FCSTD DOCUMENT  (FreeCAD 0.17R13541 (Git))
Label: lorenz
License: All rights reserved
LicenseURL: http://en.wikipedia.org/wiki/All_rights_reserved
objects: Part::Cut×431, Part::Cylinder×310, Part::Box×272, Part::Feature×196, Part::Chamfer×123, Part::MultiFuse×121, Part::Fuse×114, Part::Fillet×96, Part::Mirroring×71, Part::Sphere×27, Part::Sweep×27, Part::Cone×25, App::DocumentObjectGroup×23, Part::MultiCommon×18, Part::Circle×5, Part::Extrusion×4, Part::Helix×4, Sketcher::SketchObject×2
note: 1846 computed .brp shape members not serialized (recipe doc carries the construction recipe); baked Part::Feature solids carry a one-line shape summary decoded from their .brp

FEATURE [Part::Sphere] Sphere
  Angle1 = -90
  Angle2 = 90
  Angle3 = 360
  AttacherType = Attacher::AttachEngine3D
  Placement = pos=(0,0,6) rot=(0,0,1;0rad)
  Radius = 3
FEATURE [Part::Box] Box112015002017004007003  label="Cube089"
  AttacherType = Attacher::AttachEngine3D
  Height = 8
  Length = 56
  Placement = pos=(-5,-5,0) rot=(0,0,1;0rad)
  Width = 46
FEATURE [Part::Feature] Sphere001 .. Sphere005  x5 (patterned run collapsed; names and placements below)
  shape: bbox 6 x 6 x 6 mm, 1 faces (baked)
  placements: 5 in arithmetic series — first pos=(9,0,6.3) rot=(0,0,1;0rad), step (9,0,0.3), last pos=(45,0,7.5) rot=(0,0,1;0rad)
FEATURE [Part::Sphere] Sphere006
  Angle1 = -90
  Angle2 = 90
  Angle3 = 360
  AttacherType = Attacher::AttachEngine3D
  Placement = pos=(0,9,6) rot=(0,0,1;0rad)
  Radius = 3.1
FEATURE [Part::Feature] Sphere006001 .. Sphere006005  x5 (patterned run collapsed; names and placements below)
  shape: bbox 6.2 x 6.2 x 6.2 mm, 1 faces (baked)
  placements: 5 in arithmetic series — first pos=(9,9,6.3) rot=(0,0,1;0rad), step (9,0,0.3), last pos=(45,9,7.5) rot=(0,0,1;0rad)
FEATURE [Part::Sphere] Sphere006006
  Angle1 = -90
  Angle2 = 90
  Angle3 = 360
  AttacherType = Attacher::AttachEngine3D
  Placement = pos=(0,18,6) rot=(0,0,1;0rad)
  Radius = 3.2
FEATURE [Part::Feature] Sphere006006001 .. Sphere006006005  x5 (patterned run collapsed; names and placements below)
  shape: bbox 6.4 x 6.4 x 6.4 mm, 1 faces (baked)
  placements: 5 in arithmetic series — first pos=(9,18,6.3) rot=(0,0,1;0rad), step (9,0,0.3), last pos=(45,18,7.5) rot=(0,0,1;0rad)
FEATURE [Part::Sphere] Sphere006006006
  Angle1 = -90
  Angle2 = 90
  Angle3 = 360
  AttacherType = Attacher::AttachEngine3D
  Placement = pos=(0,27,6) rot=(0,0,1;0rad)
  Radius = 3.3
FEATURE [Part::Feature] Sphere006006006001 .. Sphere006006006005  x5 (patterned run collapsed; names and placements below)
  shape: bbox 6.6 x 6.6 x 6.6 mm, 1 faces (baked)
  placements: 5 in arithmetic series — first pos=(9,27,6.3) rot=(0,0,1;0rad), step (9,0,0.3), last pos=(45,27,7.5) rot=(0,0,1;0rad)
FEATURE [Part::Sphere] Sphere006006006006
  Angle1 = -90
  Angle2 = 90
  Angle3 = 360
  AttacherType = Attacher::AttachEngine3D
  Placement = pos=(0,36,6) rot=(0,0,1;0rad)
  Radius = 3.4
FEATURE [Part::Feature] Sphere006006006006001 .. Sphere006006006006005  x5 (patterned run collapsed; names and placements below)
  shape: bbox 6.8 x 6.8 x 6.8 mm, 1 faces (baked)
  placements: 5 in arithmetic series — first pos=(9,36,6.3) rot=(0,0,1;0rad), step (9,0,0.3), last pos=(45,36,7.5) rot=(0,0,1;0rad)
FEATURE [Part::Cut] Cut175
  Base = -> Box112015002017004007003
  Tool = -> Sphere
FEATURE [Part::Cut] Cut176
  Base = -> Cut175
  Tool = -> Sphere006006006006005
FEATURE [Part::Cut] Cut177
  Base = -> Cut176
  Tool = -> Sphere006006006006004
FEATURE [Part::Cut] Cut178
  Base = -> Cut177
  Tool = -> Sphere006006006006003
FEATURE [Part::Cut] Cut179
  Base = -> Cut178
  Tool = -> Sphere006006006006002
FEATURE [Part::Cut] Cut180
  Base = -> Cut179
  Tool = -> Sphere006006006006001
FEATURE [Part::Cut] Cut181
  Base = -> Cut180
  Tool = -> Sphere006006006006
FEATURE [Part::Cut] Cut182
  Base = -> Cut181
  Tool = -> Sphere006006006005
FEATURE [Part::Cut] Cut183
  Base = -> Cut182
  Tool = -> Sphere006006006004
FEATURE [Part::Cut] Cut184
  Base = -> Cut183
  Tool = -> Sphere006006006003
FEATURE [Part::Cut] Cut185
  Base = -> Cut184
  Tool = -> Sphere006006006002
FEATURE [Part::Cut] Cut186
  Base = -> Cut185
  Tool = -> Sphere006006006001
FEATURE [Part::Cut] Cut187
  Base = -> Cut186
  Tool = -> Sphere006006006
FEATURE [Part::Cut] Cut188
  Base = -> Cut187
  Tool = -> Sphere006006005
FEATURE [Part::Cut] Cut189
  Base = -> Cut188
  Tool = -> Sphere006006004
FEATURE [Part::Cut] Cut190
  Base = -> Cut189
  Tool = -> Sphere006006003
FEATURE [Part::Cut] Cut191
  Base = -> Cut190
  Tool = -> Sphere006006002
FEATURE [Part::Cut] Cut192
  Base = -> Cut191
  Tool = -> Sphere006006001
FEATURE [Part::Cut] Cut193
  Base = -> Cut192
  Tool = -> Sphere006006
FEATURE [Part::Cut] Cut194
  Base = -> Cut193
  Tool = -> Sphere006005
FEATURE [Part::Cut] Cut195
  Base = -> Cut194
  Tool = -> Sphere006004
FEATURE [Part::Cut] Cut196
  Base = -> Cut195
  Tool = -> Sphere006003
FEATURE [Part::Cut] Cut197
  Base = -> Cut196
  Tool = -> Sphere006002
FEATURE [Part::Cut] Cut198
  Base = -> Cut197
  Tool = -> Sphere006001
FEATURE [Part::Cut] Cut199
  Base = -> Cut198
  Tool = -> Sphere006
FEATURE [Part::Cut] Cut200
  Base = -> Cut199
  Tool = -> Sphere005
FEATURE [Part::Cut] Cut201
  Base = -> Cut200
  Tool = -> Sphere004
FEATURE [Part::Cut] Cut202
  Base = -> Cut201
  Tool = -> Sphere003
FEATURE [Part::Cut] Cut203
  Base = -> Cut202
  Tool = -> Sphere002
FEATURE [Part::Cut] Cut204
  Base = -> Cut203
  Tool = -> Sphere001
FEATURE [Part::Chamfer] Chamfer006012003  label="ball-socket-test"
  Base = -> Cut204
  Edges = 1 edges r=2: [Edge1]
FEATURE [Part::Box] Box112015002017004007004016  label="Cube099"
  AttacherType = Attacher::AttachEngine3D
  Height = 14
  Length = 4.4
  Placement = pos=(-2.2,-2,-4) rot=(0,0,1;0rad)
  Width = 4
FEATURE [Part::Chamfer] Chamfer006012018
  Base = -> Box112015002017004007004016
  Edges = 1 edges r=2: [Edge6]
FEATURE [Part::Chamfer] Chamfer006012019
  Base = -> Chamfer006012018
  Edges = 1 edges r=2: [Edge15]
  Placement = pos=(0,0,2) rot=(0,0,1;0rad)
FEATURE [Part::Chamfer] Chamfer003
  Base = -> Chamfer006012019
  Edges = 1 edges r=2: [Edge14]
FEATURE [Part::Chamfer] Chamfer006012020  label="PTFE-slot-002"
  Base = -> Chamfer003
  Edges = 1 edges r=2: [Edge16]
  Placement = pos=(0,-6.25,0) rot=(0,0,1;0rad)
FEATURE [Part::Feature] Fusion051010010012015014001  label="reactor-slot-1"
  Placement = pos=(5.41266,3.125,0) rot=(0,0,1;2.0944rad)
  shape: bbox 5.997 x 5.887 x 14 mm, 14 faces (baked)
FEATURE [Part::Feature] Fusion051010010012015014002  label="reactor-slot-2"
  Placement = pos=(-5.41266,3.125,0) rot=(0,0,1;4.18879rad)
  shape: bbox 5.997 x 5.887 x 14 mm, 14 faces (baked)
FEATURE [Part::Cylinder] Cylinder054029  label="M4-adjuster"
  Angle = 360
  AttacherType = Attacher::AttachEngine3D
  Height = 20
  Placement = pos=(0,-5,5) rot=(1,0,0;1.5708rad)
  Radius = 1.7
FEATURE [Part::Fuse] Fusion051010010012015014003  label="adjuster-slot"
  Base = -> Chamfer006012020
  Tool = -> Cylinder054029
FEATURE [Part::Cylinder] Cylinder054031  label="steel002"
  Angle = 360
  AttacherType = Attacher::AttachEngine3D
  Height = 200
  Placement = pos=(0,0,-100) rot=(0,0,1;0rad)
  Radius = 5
FEATURE [Part::Box] Box112015002017004007004017  label="Cube100"
  AttacherType = Attacher::AttachEngine3D
  Height = 16
  Length = 16
  Placement = pos=(0,-30,0) rot=(0,0,1;0rad)
  Width = 60
FEATURE [Part::Box] Box112015002017004007004018  label="Cube101"
  AttacherType = Attacher::AttachEngine3D
  Height = 20
  Length = 100
  Placement = pos=(-50,-50,-28) rot=(0,0,1;0rad)
  Width = 100
FEATURE [Part::Sphere] Sphere006006006006008
  Angle1 = -90
  Angle2 = 90
  Angle3 = 360
  AttacherType = Attacher::AttachEngine3D
  Placement = pos=(8,25,1.2) rot=(0,0,1;0rad)
  Radius = 3.05
FEATURE [Part::Sphere] Sphere006006006006009
  Angle1 = -90
  Angle2 = 90
  Angle3 = 360
  AttacherType = Attacher::AttachEngine3D
  Placement = pos=(8,-25,1.2) rot=(0,0,1;0rad)
  Radius = 3.05
FEATURE [Part::Cut] Cut253
  Base = -> Box112015002017004007004017
  Tool = -> Sphere006006006006008
FEATURE [Part::Cut] Cut254
  Base = -> Cut253
  Placement = pos=(-22,0,3) rot=(0,1,0;2.35619rad)
  Tool = -> Sphere006006006006009
FEATURE [Part::Cut] Cut255  label="socket-bar001"
  Base = -> Cut254
  Placement = pos=(22,0,-8) rot=(1,0,0;3.14159rad)
  Tool = -> Box112015002017004007004018
FEATURE [Part::Fuse] Fusion051010010012015014004
  Base = -> Fusion051010010012015014001
  Tool = -> Fusion051010010012015014002
FEATURE [Part::Fuse] Fusion051010010012015014005
  Base = -> Fusion051010010012015014003
  Tool = -> Fusion051010010012015014004
FEATURE [Part::Fuse] Fusion051010010012015014006  label="bearing-cavity-3a"
  Base = -> Cylinder054031
  Placement = pos=(9,-20,-4) rot=(0,1,0;3.14159rad)
  Tool = -> Fusion051010010012015014005
FEATURE [Part::Box] Box112015002017004007004019  label="Cube102"
  AttacherType = Attacher::AttachEngine3D
  Height = 14
  Length = 4.4
  Placement = pos=(-2.2,-2,-4) rot=(0,0,1;0rad)
  Width = 4
FEATURE [Part::Chamfer] Chamfer006012021
  Base = -> Box112015002017004007004019
  Edges = 1 edges r=2: [Edge6]
FEATURE [Part::Chamfer] Chamfer006012022
  Base = -> Chamfer006012021
  Edges = 1 edges r=2: [Edge15]
  Placement = pos=(0,0,2) rot=(0,0,1;0rad)
FEATURE [Part::Chamfer] Chamfer006012023
  Base = -> Chamfer006012022
  Edges = 1 edges r=2: [Edge14]
FEATURE [Part::Chamfer] Chamfer006012024  label="PTFE-slot-003"
  Base = -> Chamfer006012023
  Edges = 1 edges r=2: [Edge16]
  Placement = pos=(0,-6.25,0) rot=(0,0,1;0rad)
FEATURE [Part::Cylinder] Cylinder054032  label="M4-adjuster001"
  Angle = 360
  AttacherType = Attacher::AttachEngine3D
  Height = 20
  Placement = pos=(0,-5,5) rot=(1,0,0;1.5708rad)
  Radius = 1.7
FEATURE [Part::Fuse] Fusion051010010012015014007  label="adjuster-slot001"
  Base = -> Chamfer006012024
  Placement = pos=(9,15,0) rot=(0.57735,-0.57735,-0.57735;4.18879rad)
  Tool = -> Cylinder054032
FEATURE [Part::Feature] Fusion051010010012015014008  label="reactor-slot-003"
  Placement = pos=(2.75,15,-6.13174e-07) rot=(0.57735,0.57735,0.57735;4.18879rad)
  shape: bbox 4.5 x 14 x 4.4 mm, 14 faces (baked)
FEATURE [Part::Box] Box112015002017004007004020  label="Cube103"
  AttacherType = Attacher::AttachEngine3D
  Height = 200
  Length = 16
  Placement = pos=(14,12,-9) rot=(0,0,1;1.5708rad)
  Width = 10
FEATURE [Part::Fuse] Fusion051010010012015014013  label="bearing-cavity-3a001"
  Base = -> Cylinder054031
  Placement = pos=(9,-20,-44) rot=(0,1,0;3.14159rad)
  Tool = -> Fusion051010010012015014005
FEATURE [Part::Box] Box112015002017004007004021  label="Cube104"
  AttacherType = Attacher::AttachEngine3D
  Height = 60
  Length = 22
  Placement = pos=(-1,-30,-60) rot=(0,0,1;0rad)
  Width = 60
FEATURE [Part::Box] Box112015002017004007004022  label="Cube105"
  AttacherType = Attacher::AttachEngine3D
  Height = 60
  Length = 24
  Placement = pos=(-2,-10,-75) rot=(0,0,1;0rad)
  Width = 20
FEATURE [Part::Box] Box112015002017004007004023  label="Cube106"
  AttacherType = Attacher::AttachEngine3D
  Height = 60
  Length = 10
  Placement = pos=(4,-34,-60) rot=(0,0,1;0rad)
  Width = 10
FEATURE [Part::Cylinder] Cylinder054033  label="centreline"
  Angle = 360
  AttacherType = Attacher::AttachEngine3D
  Height = 500
  Placement = pos=(0,0,-350) rot=(0,0,1;0rad)
  Radius = 0.1
FEATURE [Part::Box] Box112015002017004007004024  label="wire-clamp-slot001"
  AttacherType = Attacher::AttachEngine3D
  Height = 30
  Length = 1
  Placement = pos=(-0.5,-6,-19) rot=(0,0,1;0rad)
  Width = 2
FEATURE [Part::Cylinder] Cylinder054035  label="wire-clamp-screw-hole-1"
  Angle = 360
  AttacherType = Attacher::AttachEngine3D
  Height = 10
  Placement = pos=(-9.5,-5,-4) rot=(0,1,0;1.5708rad)
  Radius = 1.7
FEATURE [Part::Cylinder] Cylinder054036  label="wire-clamp-screw-hole-2"
  Angle = 360
  AttacherType = Attacher::AttachEngine3D
  Height = 10
  Placement = pos=(-9.5,-5,-12) rot=(0,1,0;1.5708rad)
  Radius = 1.7
FEATURE [Part::Box] Box112015002017004007004025  label="Cube108"
  AttacherType = Attacher::AttachEngine3D
  Height = 15
  Length = 6
  Placement = pos=(-6.5,-9,-15) rot=(0,0,1;0rad)
  Width = 18
FEATURE [Part::Box] Box112015002017004007004026  label="wire-slot"
  AttacherType = Attacher::AttachEngine3D
  Height = 30
  Length = 8
  Placement = pos=(-4,5,-19) rot=(0,0,1;0rad)
  Width = 2
FEATURE [Part::Cylinder] Cylinder054037  label="6146 8mm Stainless Tube x 400mm"
  Angle = 360
  AttacherType = Attacher::AttachEngine3D
  Height = 395
  Placement = pos=(9,-20,-275) rot=(0,0,1;0rad)
  Radius = 4
FEATURE [Part::Cylinder] Cylinder054038  label="6146 8mm Stainless Tube x 400mm001"
  Angle = 360
  AttacherType = Attacher::AttachEngine3D
  Height = 395
  Placement = pos=(9,20,-275) rot=(0,0,1;0rad)
  Radius = 4
FEATURE [Part::Box] Box112015002017004007004027  label="Cube110"
  AttacherType = Attacher::AttachEngine3D
  Height = 42
  Length = 32
  Placement = pos=(-11,-30,-1) rot=(0,0,1;0rad)
  Width = 60
FEATURE [Part::Box] Box112015002017004007004028  label="Cube111"
  AttacherType = Attacher::AttachEngine3D
  Height = 35
  Length = 35
  Placement = pos=(-11,17.5,-299) rot=(0,0,1;3.14159rad)
  Width = 35
FEATURE [Part::Cylinder] Cylinder054039  label="drive"
  Angle = 360
  AttacherType = Attacher::AttachEngine3D
  Height = 22
  Placement = pos=(-11,0,-281.5) rot=(0.707107,0,0.707107;3.14159rad)
  Radius = 5
FEATURE [Part::Cylinder] Cylinder054040  label="boss"
  Angle = 360
  AttacherType = Attacher::AttachEngine3D
  Height = 2
  Placement = pos=(-11,0,-281.5) rot=(0.707107,0,0.707107;3.14159rad)
  Radius = 11
FEATURE [Part::Cylinder] Cylinder054041  label="M3-1"
  Angle = 360
  AttacherType = Attacher::AttachEngine3D
  Height = 50
  Placement = pos=(-11,-13,-268.5) rot=(0.707107,0,0.707107;3.14159rad)
  Radius = 1.7
FEATURE [Part::Cylinder] Cylinder054042  label="M3-2"
  Angle = 360
  AttacherType = Attacher::AttachEngine3D
  Height = 50
  Placement = pos=(-11,-13,-294.5) rot=(0.707107,0,0.707107;3.14159rad)
  Radius = 1.7
FEATURE [Part::Cylinder] Cylinder054043  label="M3-3"
  Angle = 360
  AttacherType = Attacher::AttachEngine3D
  Height = 50
  Placement = pos=(-11,13,-268.5) rot=(0.707107,0,0.707107;3.14159rad)
  Radius = 1.7
FEATURE [Part::Cylinder] Cylinder054044  label="M3-4"
  Angle = 360
  AttacherType = Attacher::AttachEngine3D
  Height = 50
  Placement = pos=(-11,13,-294.5) rot=(0.707107,0,0.707107;3.14159rad)
  Radius = 1.7
FEATURE [App::DocumentObjectGroup] Group005  label="130 NEMA-14"
  Group = -> [Box112015002017004007004028,Cylinder054039,Cylinder054040,Cylinder054041,Cylinder054042,Cylinder054043,Cylinder054044]
FEATURE [Part::Cylinder] Cylinder054045  label="boss001"
  Angle = 360
  AttacherType = Attacher::AttachEngine3D
  Height = 3
  Placement = pos=(-11,0,17.5) rot=(0,1,0;1.5708rad)
  Radius = 12
FEATURE [Part::Cut] Cut264
  Base = -> Box112015002017004007004027
  Tool = -> Cylinder054045
FEATURE [Part::Cylinder] Cylinder054046  label="M3-005"
  Angle = 360
  AttacherType = Attacher::AttachEngine3D
  Height = 50
  Placement = pos=(-12,13,30.5) rot=(0,1,0;1.5708rad)
  Radius = 1.7
FEATURE [Part::Cylinder] Cylinder054047  label="M3-006"
  Angle = 360
  AttacherType = Attacher::AttachEngine3D
  Height = 50
  Placement = pos=(-12,-13,4.5) rot=(0,1,0;1.5708rad)
  Radius = 1.7
FEATURE [Part::Cylinder] Cylinder054048  label="M3-007"
  Angle = 360
  AttacherType = Attacher::AttachEngine3D
  Height = 50
  Placement = pos=(-12,13,4.5) rot=(0,1,0;1.5708rad)
  Radius = 1.7
FEATURE [Part::Cylinder] Cylinder054049  label="M3-008"
  Angle = 360
  AttacherType = Attacher::AttachEngine3D
  Height = 50
  Placement = pos=(-12,-13,30.5) rot=(0,1,0;1.5708rad)
  Radius = 1.7
FEATURE [Part::Cut] Cut265
  Base = -> Cut264
  Tool = -> Cylinder054046
FEATURE [Part::Cut] Cut266
  Base = -> Cut265
  Tool = -> Cylinder054049
FEATURE [Part::Cut] Cut267
  Base = -> Cut266
  Tool = -> Cylinder054048
FEATURE [Part::Cut] Cut268
  Base = -> Cut267
  Tool = -> Cylinder054047
FEATURE [Part::Cylinder] Cylinder054050  label="drive001"
  Angle = 360
  AttacherType = Attacher::AttachEngine3D
  Height = 40
  Placement = pos=(-9,0,17.5) rot=(0,1,0;1.5708rad)
  Radius = 8
FEATURE [Part::Cut] Cut269
  Base = -> Cut268
  Tool = -> Cylinder054050
FEATURE [Part::Box] Box112015002017004007004029  label="Cube112"
  AttacherType = Attacher::AttachEngine3D
  Height = 50
  Length = 18
  Placement = pos=(-8,-10,9) rot=(0,0,1;0rad)
  Width = 20
FEATURE [Part::Cut] Cut270
  Base = -> Cut269
  Tool = -> Box112015002017004007004029
FEATURE [Part::Cylinder] Cylinder054051  label="grub-003"
  Angle = 360
  AttacherType = Attacher::AttachEngine3D
  Height = 30
  Placement = pos=(-28,26,32) rot=(1,0,0;1.5708rad)
  Radius = 1.7
FEATURE [Part::Box] Box112015002017004007004030  label="Cube113"
  AttacherType = Attacher::AttachEngine3D
  Height = 33
  Length = 5.3
  Placement = pos=(-30.65,6,29) rot=(0,0,1;0rad)
  Width = 2.5
FEATURE [Part::Fuse] Fusion051010010012015014017  label="nut-trap"
  Base = -> Cylinder054051
  Placement = pos=(43,5,5) rot=(0,0,1;0rad)
  Tool = -> Box112015002017004007004030
FEATURE [Part::Box] Box112015002017004007004031  label="Cube114"
  AttacherType = Attacher::AttachEngine3D
  Height = 50
  Length = 15
  Placement = pos=(10,19.25,13) rot=(0,0,1;0rad)
  Width = 1.5
FEATURE [Part::Fuse] Fusion051010010012015014018  label="rod-clamp"
  Base = -> Fusion051010010012015014017
  Tool = -> Box112015002017004007004031
FEATURE [Part::Cylinder] Cylinder054052  label="steel-004"
  Angle = 360
  AttacherType = Attacher::AttachEngine3D
  Height = 395
  Placement = pos=(9,20,-300) rot=(0,0,1;0rad)
  Radius = 3.95
FEATURE [Part::Fuse] Fusion051010010012015014019  label="rod-and-clamp"
  Base = -> Fusion051010010012015014018
  Tool = -> Cylinder054052
FEATURE [Part::Fuse] Fusion051010010012015014020  label="rod-and-clamp001"
  Base = -> Fusion051010010012015014018
  Tool = -> Cylinder054052
FEATURE [Part::Mirroring] Part__Mirroring005006  label="rod-and-clamp (Mirror #7)"
  Base = (0,0,0)
  Normal = (0,1,0)
  Source = -> Fusion051010010012015014019
FEATURE [Part::Cut] Cut271
  Base = -> Cut270
  Tool = -> Fusion051010010012015014020
FEATURE [Part::Cut] Cut272  label="base-block-b"
  Base = -> Cut271
  Placement = pos=(0,0,-299) rot=(0,0,1;0rad)
  Tool = -> Part__Mirroring005006
FEATURE [Part::Box] Box112015002017004007004032  label="Cube115"
  AttacherType = Attacher::AttachEngine3D
  Height = 15
  Length = 32
  Placement = pos=(-11,-30,26) rot=(0,0,1;0rad)
  Width = 60
FEATURE [Part::Cylinder] Cylinder054053  label="grub-004"
  Angle = 360
  AttacherType = Attacher::AttachEngine3D
  Height = 30
  Placement = pos=(-28,31,32) rot=(1,0,0;1.5708rad)
  Radius = 1.7
FEATURE [Part::Box] Box112015002017004007004034  label="Cube117"
  AttacherType = Attacher::AttachEngine3D
  Height = 33
  Length = 5.3
  Placement = pos=(-30.65,6,29) rot=(0,0,1;0rad)
  Width = 2.5
FEATURE [Part::Fuse] Fusion051010010012015014021  label="nut-trap001"
  Base = -> Cylinder054053
  Placement = pos=(43,7,5) rot=(0,0,1;0rad)
  Tool = -> Box112015002017004007004034
FEATURE [Part::Box] Box112015002017004007004035  label="Cube118"
  AttacherType = Attacher::AttachEngine3D
  Height = 50
  Length = 15
  Placement = pos=(10,19.25,-4) rot=(0,0,1;0rad)
  Width = 1.5
FEATURE [Part::Fuse] Fusion051010010012015014022  label="rod-clamp001"
  Base = -> Fusion051010010012015014021
  Tool = -> Box112015002017004007004035
FEATURE [Part::Cylinder] Cylinder054054  label="steel-005"
  Angle = 360
  AttacherType = Attacher::AttachEngine3D
  Height = 395
  Placement = pos=(9,20,-300) rot=(0,0,1;0rad)
  Radius = 3.9
FEATURE [Part::Fuse] Fusion051010010012015014023  label="rod-and-clamp002"
  Base = -> Fusion051010010012015014022
  Tool = -> Cylinder054054
FEATURE [Part::Fuse] Fusion051010010012015014024  label="rod-and-clamp003"
  Base = -> Fusion051010010012015014022
  Tool = -> Cylinder054054
FEATURE [Part::Mirroring] Part__Mirroring005007  label="rod-and-clamp (Mirror #7)001"
  Base = (0,0,0)
  Normal = (0,1,0)
  Source = -> Fusion051010010012015014023
FEATURE [Part::Cylinder] Cylinder054055  label="6145 V Bearing"
  Angle = 360
  AttacherType = Attacher::AttachEngine3D
  Height = 4
  Placement = pos=(-2,0,117) rot=(0,1,0;1.5708rad)
  Radius = 6
FEATURE [Part::Cone] Cone011
  Angle = 360
  AttacherType = Attacher::AttachEngine3D
  Height = 3
  Placement = pos=(0,0,2) rot=(0,0,1;0rad)
  Radius1 = 2.5
  Radius2 = 5.5
FEATURE [Part::Mirroring] Part__Mirroring005008  label="Cone011 (Mirror #9)"
  Base = (0,0,0)
  Normal = (0,0,1)
  Placement = pos=(0.1,0,38) rot=(0,1,0;1.5708rad)
  Source = -> Cone011
FEATURE [Part::Cone] Cone012
  Angle = 360
  AttacherType = Attacher::AttachEngine3D
  Height = 3
  Placement = pos=(1.9,0,38) rot=(0,1,0;1.5708rad)
  Radius1 = 2.5
  Radius2 = 5.5
FEATURE [Part::Box] Box112015002017004007004036  label="Cube119"
  AttacherType = Attacher::AttachEngine3D
  Height = 8
  Length = 60
  Placement = pos=(-4,-7,68) rot=(0,1,0;1.5708rad)
  Width = 14
FEATURE [Part::Box] Box112015002017004007004037  label="Cube120"
  AttacherType = Attacher::AttachEngine3D
  Height = 16
  Length = 10
  Placement = pos=(-8,-14,43) rot=(0,1,0;1.5708rad)
  Width = 28
FEATURE [Part::Cylinder] Cylinder054056  label="bearing-M3"
  Angle = 360
  AttacherType = Attacher::AttachEngine3D
  Height = 40
  Placement = pos=(-20,0,38) rot=(0,1,0;1.5708rad)
  Radius = 1.4
FEATURE [Part::Cylinder] Cylinder054057  label="Cylinder054099009114"
  Angle = 360
  AttacherType = Attacher::AttachEngine3D
  Height = 10
  Radius = 5
FEATURE [Part::Box] Box112015002017004007004038  label="Cube121"
  AttacherType = Attacher::AttachEngine3D
  Height = 12
  Length = 10
  Placement = pos=(-5,2.75,-1) rot=(0,0,1;0rad)
  Width = 10
FEATURE [Part::Feature] Box112015002017004007004038001
  Placement = pos=(-4.88157,-2.95513,-1) rot=(0,0,1;1.0472rad)
  shape: bbox 13.66 x 13.66 x 12 mm, 6 faces (baked)
FEATURE [Part::Feature] Box112015002017004007004038002
  Placement = pos=(0.11843,-5.70513,-1) rot=(0,0,1;2.0944rad)
  shape: bbox 13.66 x 13.66 x 12 mm, 6 faces (baked)
FEATURE [Part::Feature] Box112015002017004007004038003
  Placement = pos=(5,-2.75,-1) rot=(0,0,1;3.14159rad)
  shape: bbox 10 x 10 x 12 mm, 6 faces (baked)
FEATURE [Part::Feature] Box112015002017004007004038004
  Placement = pos=(4.88157,2.95513,-1) rot=(0,0,1;4.18879rad)
  shape: bbox 13.66 x 13.66 x 12 mm, 6 faces (baked)
FEATURE [Part::Feature] Box112015002017004007004038005
  Placement = pos=(-0.11843,5.70513,-1) rot=(0,0,-1;1.0472rad)
  shape: bbox 13.66 x 13.66 x 12 mm, 6 faces (baked)
FEATURE [Part::Cut] Cut273
  Base = -> Cylinder054057
  Tool = -> Box112015002017004007004038
FEATURE [Part::Cut] Cut274
  Base = -> Cut273
  Tool = -> Box112015002017004007004038005
FEATURE [Part::Cut] Cut275
  Base = -> Cut274
  Tool = -> Box112015002017004007004038004
FEATURE [Part::Cut] Cut276
  Base = -> Cut275
  Tool = -> Box112015002017004007004038003
FEATURE [Part::Cut] Cut277
  Base = -> Cut276
  Tool = -> Box112015002017004007004038002
FEATURE [Part::Cut] Cut278
  Base = -> Cut277
  Tool = -> Box112015002017004007004038001
FEATURE [Part::Cylinder] Cylinder054058  label="Cylinder054099009137012"
  Angle = 360
  AttacherType = Attacher::AttachEngine3D
  Height = 50
  Placement = pos=(0,0,-20) rot=(0,0,1;0rad)
  Radius = 1.7
FEATURE [Part::Fuse] Fusion051010010012015014025  label="M3-nut-hole"
  Base = -> Cut278
  Placement = pos=(0,-10.5,27) rot=(0,0,1;0rad)
  Tool = -> Cylinder054058
FEATURE [Part::Box] Box112015002017004007004038006  label="Cube122"
  AttacherType = Attacher::AttachEngine3D
  Height = 18
  Length = 10
  Placement = pos=(-9,-15,42) rot=(0,1,0;1.5708rad)
  Width = 30
FEATURE [Part::Box] Box112015002017004007004038007  label="Cube123"
  AttacherType = Attacher::AttachEngine3D
  Height = 8
  Length = 60
  Placement = pos=(-4,-7,68) rot=(0,1,0;1.5708rad)
  Width = 14
FEATURE [Part::Cylinder] Cylinder054059  label="Cylinder054099009137030"
  Angle = 360
  AttacherType = Attacher::AttachEngine3D
  Height = 20
  Placement = pos=(-10,11,32) rot=(0,1,0;1.5708rad)
  Radius = 2
FEATURE [Part::Fuse] Fusion051010010012015014027  label="bearing-cones"
  Base = -> Part__Mirroring005008
  Tool = -> Cone012
FEATURE [Part::Box] Box112015002017004007004038008  label="Cube124"
  AttacherType = Attacher::AttachEngine3D
  Height = 16
  Length = 10
  Placement = pos=(-8,-14,43) rot=(0,1,0;1.5708rad)
  Width = 28
FEATURE [Part::MultiCommon] Common010  label="bearing-cones-truncated"
  Shapes = -> [Box112015002017004007004038008,Fusion051010010012015014027]
FEATURE [Part::Box] Box112015002017004007004038009  label="Cube125"
  AttacherType = Attacher::AttachEngine3D
  Height = 15
  Length = 31
  Placement = pos=(-15.5,-17,-13) rot=(0,0,1;0rad)
  Width = 34
FEATURE [Part::Box] Box112015002017004007004038010  label="Cube126"
  AttacherType = Attacher::AttachEngine3D
  Height = 15
  Length = 31
  Placement = pos=(0.5,-35,-13) rot=(0,0,1;0rad)
  Width = 70
FEATURE [Part::Fuse] Fusion051010010012015014030
  Base = -> Box112015002017004007004038009
  Tool = -> Box112015002017004007004038010
FEATURE [Part::Cut] Cut294  label="ball-socket-tabs"
  Base = -> Cut255
  Tool = -> Fusion051010010012015014030
FEATURE [Part::Cylinder] Cylinder054060  label="Cylinder054100"
  Angle = 360
  AttacherType = Attacher::AttachEngine3D
  Height = 20
  Placement = pos=(-10,11,32) rot=(0,1,0;1.5708rad)
  Radius = 2.2
FEATURE [Part::Cylinder] Cylinder054061  label="Cylinder054101"
  Angle = 360
  AttacherType = Attacher::AttachEngine3D
  Height = 50
  Placement = pos=(0,-10.5,7) rot=(0,0,1;0rad)
  Radius = 1.3
FEATURE [Part::Box] Box112015002017004007004038011  label="Cube127"
  AttacherType = Attacher::AttachEngine3D
  Height = 20
  Length = 10
  Placement = pos=(18,-11,78) rot=(0,0,1;0rad)
  Width = 22
FEATURE [Part::Cylinder] Cylinder054062  label="Cylinder054102"
  Angle = 360
  AttacherType = Attacher::AttachEngine3D
  Height = 30
  Placement = pos=(11,4.75,86) rot=(0,1,0;1.5708rad)
  Radius = 1.1
FEATURE [Part::Cylinder] Cylinder054063  label="Cylinder054103"
  Angle = 360
  AttacherType = Attacher::AttachEngine3D
  Height = 30
  Placement = pos=(11,-4.75,86) rot=(0,1,0;1.5708rad)
  Radius = 1.1
FEATURE [Part::Fuse] Fusion051010010012015014032
  Base = -> Box112015002017004007004038011
  Tool = -> Cylinder054062
FEATURE [Part::Fuse] Fusion051010010012015014033  label="microswitch-cavity"
  Base = -> Cylinder054063
  Tool = -> Fusion051010010012015014032
FEATURE [Part::Chamfer] Chamfer006012025
  Base = -> Box112015002017004007004037
  Edges = 1 edges r=8: [Edge12]
FEATURE [Part::Chamfer] Chamfer006012026
  Base = -> Chamfer006012025
  Edges = 1 edges r=8: [Edge7]
FEATURE [Part::Cut] Cut298
  Base = -> Chamfer006012026
  Tool = -> Box112015002017004007004036
FEATURE [Part::Fuse] Fusion051010010012015014034
  Base = -> Common010
  Tool = -> Cut298
FEATURE [Part::Cut] Cut299
  Base = -> Fusion051010010012015014034
  Tool = -> Cylinder054056
FEATURE [Part::Cut] Cut300
  Base = -> Cut299
  Tool = -> Cylinder054060
FEATURE [Part::Cut] Cut301  label="6144 Wire Tensioner Block"
  Base = -> Cut300
  Placement = pos=(0,0,79) rot=(0,0,1;0rad)
  Tool = -> Cylinder054061
FEATURE [Part::Chamfer] Chamfer006012027
  Base = -> Box112015002017004007004038006
  Edges = 1 edges r=8: [Edge10]
FEATURE [Part::Chamfer] Chamfer006012028
  Base = -> Chamfer006012027
  Edges = 1 edges r=8: [Edge13]
FEATURE [Part::Cut] Cut302
  Base = -> Box112015002017004007004032
  Tool = -> Chamfer006012028
FEATURE [Part::Cut] Cut303
  Base = -> Cut302
  Tool = -> Box112015002017004007004038007
FEATURE [Part::Fuse] Fusion051010010012015014035
  Base = -> Cylinder054059
  Tool = -> Cut303
FEATURE [Part::Cut] Cut304
  Base = -> Fusion051010010012015014035
  Tool = -> Part__Mirroring005007
FEATURE [Part::Cut] Cut305
  Base = -> Cut304
  Placement = pos=(0,0,54) rot=(0,0,1;0rad)
  Tool = -> Fusion051010010012015014024
FEATURE [Part::Cut] Cut306  label="top-block-a"
  Base = -> Cut305
  Tool = -> Fusion051010010012015014033
FEATURE [Part::Box] Box112015002017004007004038026  label="crimp-hole-1"
  AttacherType = Attacher::AttachEngine3D
  Height = 2
  Length = 29
  Placement = pos=(-28,-27,-278.5) rot=(0,0,1;0rad)
  Width = 2
FEATURE [Part::Box] Box112015002017004007004038027  label="crimp-hole-2"
  AttacherType = Attacher::AttachEngine3D
  Height = 2
  Length = 29
  Placement = pos=(-27.8,-27,-283.58) rot=(0,0,1;0rad)
  Width = 2
FEATURE [Part::Cylinder] Cylinder054028  label="steel"
  Angle = 360
  AttacherType = Attacher::AttachEngine3D
  Height = 100
  Placement = pos=(0,0,-50) rot=(0,0,1;0rad)
  Radius = 4
FEATURE [Part::Circle] Circle
  Angle0 = 0
  Angle1 = 360
  AttacherType = Attacher::AttachEngine3D
  Placement = pos=(1,-26,-297.5) rot=(0,1,0;1.5708rad)
  Radius = 0.7
FEATURE [Part::Box] Box112015002017004007004038040  label="tiny-point-cube"
  AttacherType = Attacher::AttachEngine3D
  Height = 0.2
  Length = 0.2
  Placement = pos=(-46,-65.3,-296) rot=(0,0,1;0rad)
  Width = 0.2
FEATURE [Part::Feature] Shape
  shape: bbox 8.954 x 5.598 x 34.27 mm, 0 faces, 0 solids (baked)
FEATURE [Part::Feature] Shape001
  shape: bbox 11.02 x 51.23 x 37.09 mm, 0 faces, 0 solids (baked)
FEATURE [Part::Circle] Circle001
  Angle0 = 0
  Angle1 = 360
  AttacherType = Attacher::AttachEngine3D
  Placement = pos=(1,-26,-297.5) rot=(0,1,0;1.5708rad)
  Radius = 1.2
FEATURE [Part::Feature] Face
  Placement = pos=(0,0,20) rot=(0,0,1;0rad)
  shape: bbox 2e-07 x 2.603 x 2.778 mm, 1 faces, 0 solids (baked)
FEATURE [Part::Feature] Shape002
  shape: bbox 24.53 x 3.067 x 36 mm, 0 faces, 0 solids (baked)
FEATURE [Part::Circle] Circle002
  Angle0 = 0
  Angle1 = 360
  AttacherType = Attacher::AttachEngine3D
  Placement = pos=(-15,23,-294) rot=(0,1,0;1.5708rad)
  Radius = 2.5
FEATURE [Part::Feature] Face002
  shape: bbox 2e-07 x 7.388 x 7.38 mm, 1 faces, 0 solids (baked)
FEATURE [Part::Sweep] Sweep002
  Frenet = false
  Sections = -> [Face002]
  Solid = true
  Spine = -> Shape002 [Edge1]
  Transition = 1
FEATURE [Part::Mirroring] Part__Mirroring  label="Sweep002 (Mirror #5)"
  Base = (0,0,0)
  Normal = (0,1,0)
  Source = -> Sweep002
FEATURE [Part::Sweep] Sweep003
  Frenet = false
  Sections = -> [Face002]
  Solid = true
  Spine = -> Shape002 [Edge1]
  Transition = 1
FEATURE [Part::Cut] Cut338
  Base = -> Cut272
  Tool = -> Sweep003
FEATURE [Part::Cut] Cut339
  Base = -> Cut338
  Tool = -> Part__Mirroring
FEATURE [Part::Feature] Shape003
  shape: bbox 8.807 x 6.01 x 17.13 mm, 0 faces, 0 solids (baked)
FEATURE [Part::Sweep] Sweep
  Frenet = false
  Sections = -> [Face]
  Solid = true
  Spine = -> Shape003 [Edge1]
  Transition = 1
FEATURE [Part::Fuse] Fusion  label="wire-hole-1"
  Base = -> Box112015002017004007004038026
  Tool = -> Sweep
FEATURE [Part::Feature] Shape004
  shape: bbox 8.864 x 52.92 x 37.82 mm, 0 faces, 0 solids (baked)
FEATURE [Part::Feature] Shape005
  shape: bbox 9.107 x 52.63 x 38.07 mm, 0 faces, 0 solids (baked)
FEATURE [Part::Feature] Face003
  Placement = pos=(0,0,14.92) rot=(0,0,1;0rad)
  shape: bbox 2e-07 x 2.603 x 2.778 mm, 1 faces, 0 solids (baked)
FEATURE [Part::Sweep] Sweep005
  Frenet = false
  Sections = -> [Face003]
  Solid = true
  Spine = -> Shape005 [Edge1]
  Transition = 1
FEATURE [Part::Fuse] Fusion051010010012015014039  label="wire-hole-2"
  Base = -> Box112015002017004007004038027
  Tool = -> Sweep005
FEATURE [Part::Cut] Cut
  Base = -> Cut339
  Tool = -> Fusion
FEATURE [Part::Cut] Cut340  label="bottom-block-4"
  Base = -> Cut
  Tool = -> Fusion051010010012015014039
FEATURE [Part::Feature] Face001
  Placement = pos=(18,22,389) rot=(0,0,1;0rad)
  shape: bbox 2e-07 x 2.603 x 2.778 mm, 1 faces, 0 solids (baked)
FEATURE [Part::Feature] Shape006
  shape: bbox 18.54 x 23.52 x 8.185 mm, 0 faces, 0 solids (baked)
FEATURE [Part::Feature] Face004
  Placement = pos=(17,22,389) rot=(0,0,1;0rad)
  shape: bbox 2e-07 x 2.603 x 2.778 mm, 1 faces, 0 solids (baked)
FEATURE [Part::Feature] Shape007
  shape: bbox 18.54 x 23.52 x 8.185 mm, 0 faces, 0 solids (baked)
FEATURE [Part::Feature] Shape008
  shape: bbox 19.54 x 23.73 x 8.185 mm, 0 faces, 0 solids (baked)
FEATURE [Part::Sweep] Sweep006  label="top-wire-1"
  Frenet = false
  Sections = -> [Face001]
  Solid = true
  Spine = -> Shape008 [Edge1]
  Transition = 1
FEATURE [Part::Feature] Face005
  Placement = pos=(18,22,389) rot=(0,0,1;0rad)
  shape: bbox 2e-07 x 2.603 x 2.778 mm, 1 faces, 0 solids (baked)
FEATURE [Part::Feature] Shape009
  shape: bbox 19.54 x 23.73 x 8.185 mm, 0 faces, 0 solids (baked)
FEATURE [Part::Sweep] Sweep007
  Frenet = false
  Sections = -> [Face005]
  Solid = true
  Spine = -> Shape009 [Edge1]
  Transition = 1
FEATURE [Part::Mirroring] Part__Mirroring005009  label="top-wire-2"
  Base = (0,0,0)
  Normal = (0,1,0)
  Source = -> Sweep007
FEATURE [Part::Cut] Cut341
  Base = -> Cut306
  Tool = -> Sweep006
FEATURE [Part::Cut] Cut342  label="top-block-4"
  Base = -> Cut341
  Tool = -> Part__Mirroring005009
FEATURE [Part::Cylinder] Cylinder  label="mounting-hole-1"
  Angle = 360
  AttacherType = Attacher::AttachEngine3D
  Height = 100
  Placement = pos=(-40,0,-7) rot=(0,1,0;1.5708rad)
  Radius = 1.3
FEATURE [Part::Cylinder] Cylinder054064  label="mounting-hole-002"
  Angle = 360
  AttacherType = Attacher::AttachEngine3D
  Height = 100
  Placement = pos=(-40,-27,-19) rot=(0,1,0;1.5708rad)
  Radius = 1.3
FEATURE [Part::Cylinder] Cylinder054065  label="mounting-hole-003"
  Angle = 360
  AttacherType = Attacher::AttachEngine3D
  Height = 100
  Placement = pos=(-40,-27,-39) rot=(0,1,0;1.5708rad)
  Radius = 1.3
FEATURE [Part::Cylinder] Cylinder054066  label="mounting-hole-004"
  Angle = 360
  AttacherType = Attacher::AttachEngine3D
  Height = 100
  Placement = pos=(-40,27,-19) rot=(0,1,0;1.5708rad)
  Radius = 1.3
FEATURE [Part::Box] Box112015002017004007004038041  label="Cube128"
  AttacherType = Attacher::AttachEngine3D
  Height = 60
  Length = 24
  Placement = pos=(-2,-10,-85) rot=(0,0,1;0rad)
  Width = 60
FEATURE [Part::Box] Box  label="Cube"
  AttacherType = Attacher::AttachEngine3D
  Height = 100
  Length = 10
  Placement = pos=(4,15,-97) rot=(0,0,1;0rad)
  Width = 10
FEATURE [Part::Fuse] Fusion051010010012015014040  label="slots"
  Base = -> Fusion051010010012015014007
  Placement = pos=(0,0,-5) rot=(0,0,1;0rad)
  Tool = -> Fusion051010010012015014008
FEATURE [Part::Chamfer] Chamfer
  Base = -> Box112015002017004007004020
  Edges = 1 edges r=5: [Edge8]
FEATURE [Part::Chamfer] Chamfer006012029
  Base = -> Chamfer
  Edges = 1 edges r=5: [Edge15]
  Placement = pos=(0,0,-2) rot=(0,0,1;0rad)
FEATURE [Part::Fuse] Fusion051010010012015014041
  Base = -> Box
  Tool = -> Chamfer006012029
FEATURE [Part::Fuse] Fusion051010010012015014042  label="bearing-cavity-2"
  Base = -> Fusion051010010012015014040
  Tool = -> Fusion051010010012015014041
FEATURE [Part::Fuse] Fusion051010010012015014043
  Base = -> Box112015002017004007004021
  Tool = -> Box112015002017004007004023
FEATURE [Part::Fuse] Fusion051010010012015014044
  Base = -> Box112015002017004007004025
  Tool = -> Fusion051010010012015014043
FEATURE [Part::Cut] Cut343
  Base = -> Fusion051010010012015014044
  Tool = -> Box112015002017004007004022
FEATURE [Part::Cut] Cut344  label="slider-blank-1"
  Base = -> Cut343
  Tool = -> Box112015002017004007004038041
FEATURE [Part::Cut] Cut345
  Base = -> Cut344
  Tool = -> Fusion051010010012015014042
FEATURE [Part::Cut] Cut346
  Base = -> Cut345
  Tool = -> Fusion051010010012015014006
FEATURE [Part::Cut] Cut347
  Base = -> Cut346
  Tool = -> Fusion051010010012015014013
FEATURE [Part::Cut] Cut348
  Base = -> Cut347
  Tool = -> Cylinder054036
FEATURE [Part::Cut] Cut349
  Base = -> Cut348
  Tool = -> Cylinder054035
FEATURE [Part::Cut] Cut350
  Base = -> Cut349
  Tool = -> Box112015002017004007004024
FEATURE [Part::Cut] Cut351  label="slider-blank-2"
  Base = -> Cut350
  Tool = -> Box112015002017004007004026
FEATURE [Part::Box] Box112015002017004007004038042  label="Cube129"
  AttacherType = Attacher::AttachEngine3D
  Height = 39
  Length = 6
  Placement = pos=(-6.5,-30,-50) rot=(0,0,1;0rad)
  Width = 8
FEATURE [Part::Box] Box112015002017004007004038043  label="Cube130"
  AttacherType = Attacher::AttachEngine3D
  Height = 14
  Length = 6
  Placement = pos=(-6.5,22,-25) rot=(0,0,1;0rad)
  Width = 8
FEATURE [Part::Chamfer] Chamfer006012030
  Base = -> Box112015002017004007004038042
  Edges = 1 edges r=5.5: [Edge4]
FEATURE [Part::Chamfer] Chamfer006012031
  Base = -> Chamfer006012030
  Edges = 1 edges r=5.5: [Edge3]
  Placement = pos=(0,0,1) rot=(0,0,1;0rad)
FEATURE [Part::Chamfer] Chamfer006012032
  Base = -> Box112015002017004007004038043
  Edges = 1 edges r=5.5: [Edge2]
FEATURE [Part::Fuse] Fusion051010010012015014045
  Base = -> Cut351
  Tool = -> Chamfer006012031
FEATURE [Part::Fuse] Fusion051010010012015014046  label="slider-blank-3"
  Base = -> Chamfer006012032
  Tool = -> Fusion051010010012015014045
FEATURE [Part::Cut] Cut352
  Base = -> Fusion051010010012015014046
  Tool = -> Cylinder
FEATURE [Part::Cut] Cut353
  Base = -> Cut352
  Tool = -> Cylinder054066
FEATURE [Part::Cut] Cut354
  Base = -> Cut353
  Tool = -> Cylinder054065
FEATURE [Part::Cut] Cut355  label="6140 slider blank"
  Base = -> Cut354
  Tool = -> Cylinder054064
FEATURE [Part::Cylinder] Cylinder054067  label="mounting-hole-005"
  Angle = 360
  AttacherType = Attacher::AttachEngine3D
  Height = 100
  Placement = pos=(-40,0,-7) rot=(0,1,0;1.5708rad)
  Radius = 1.7
FEATURE [Part::Cylinder] Cylinder054068  label="mounting-hole-006"
  Angle = 360
  AttacherType = Attacher::AttachEngine3D
  Height = 100
  Placement = pos=(-40,-27,-19) rot=(0,1,0;1.5708rad)
  Radius = 1.7
FEATURE [Part::Cylinder] Cylinder054069  label="mounting-hole-007"
  Angle = 360
  AttacherType = Attacher::AttachEngine3D
  Height = 100
  Placement = pos=(-40,-27,-39) rot=(0,1,0;1.5708rad)
  Radius = 1.7
FEATURE [Part::Cylinder] Cylinder054070  label="mounting-hole-008"
  Angle = 360
  AttacherType = Attacher::AttachEngine3D
  Height = 100
  Placement = pos=(-40,27,-19) rot=(0,1,0;1.5708rad)
  Radius = 1.7
FEATURE [Part::Cylinder] Cylinder054071  label="steel-006"
  Angle = 360
  AttacherType = Attacher::AttachEngine3D
  Height = 16
  Placement = pos=(9,-20,-260) rot=(0,0,1;0rad)
  Radius = 2
FEATURE [Part::Chamfer] Chamfer006012033
  Base = -> Cylinder054071
  Edges = 1 edges r=1: [Edge3]
FEATURE [Part::Chamfer] Chamfer006012034
  Base = -> Chamfer006012033
  Edges = 1 edges r=1: [Edge3]
  Placement = pos=(0.3,-2.2,-15) rot=(0,0,1;0rad)
FEATURE [Part::Chamfer] Chamfer006012035
  Base = -> Chamfer006012033
  Edges = 1 edges r=1: [Edge3]
  Placement = pos=(0.3,-2.2,-15) rot=(0,0,1;0rad)
FEATURE [Part::Mirroring] Part__Mirroring005010  label="Chamfer006012034 (Mirror #6)"
  Base = (0,0,0)
  Normal = (0,1,0)
  Source = -> Chamfer006012034
FEATURE [Part::Cut] Cut356
  Base = -> Cut340
  Tool = -> Chamfer006012035
FEATURE [Part::Cut] Cut357  label="bottom-block-5"
  Base = -> Cut356
  Tool = -> Part__Mirroring005010
FEATURE [Part::Chamfer] Chamfer006012036
  Base = -> Chamfer006012033
  Edges = 1 edges r=1: [Edge3]
  Placement = pos=(-5.26328,-6.24905,337) rot=(0,0,1;0.349066rad)
FEATURE [Part::Chamfer] Chamfer006012037
  Base = -> Chamfer006012033
  Edges = 1 edges r=1: [Edge3]
  Placement = pos=(-5.26328,-6.24905,337) rot=(0,0,1;0.349066rad)
FEATURE [Part::Mirroring] Part__Mirroring005011  label="Chamfer006012036 (Mirror #7)"
  Base = (0,0,0)
  Normal = (0,1,0)
  Source = -> Chamfer006012036
FEATURE [Part::Cut] Cut358
  Base = -> Cut342
  Tool = -> Chamfer006012037
FEATURE [Part::Cut] Cut359  label="top-block-7"
  Base = -> Cut358
  Placement = pos=(0,0,25) rot=(0,0,1;0rad)
  Tool = -> Part__Mirroring005011
FEATURE [Part::Box] Box112015002017004007004038044  label="Cube131"
  AttacherType = Attacher::AttachEngine3D
  Height = 10
  Length = 8
  Placement = pos=(5,13.5,-285) rot=(0,0,1;0rad)
  Width = 4
FEATURE [Part::Chamfer] Chamfer006012038
  Base = -> Box112015002017004007004038044
  Edges = 1 edges r=3: [Edge11]
FEATURE [Part::Chamfer] Chamfer006012039
  Base = -> Box112015002017004007004038044
  Edges = 1 edges r=3: [Edge11]
FEATURE [Part::Mirroring] Part__Mirroring005012  label="Chamfer006012038 (Mirror #8)"
  Base = (0,0,0)
  Normal = (0,1,0)
  Source = -> Chamfer006012038
FEATURE [Part::Fuse] Fusion051010010012015014047
  Base = -> Cut357
  Tool = -> Chamfer006012039
FEATURE [Part::Fuse] Fusion051010010012015014048  label="bottom-block-006"
  Base = -> Part__Mirroring005012
  Tool = -> Fusion051010010012015014047
FEATURE [Part::Box] Box112015002017004007004038045  label="Cube132"
  AttacherType = Attacher::AttachEngine3D
  Height = 25
  Length = 5
  Placement = pos=(-11.5,-30,-25) rot=(0,0,1;0rad)
  Width = 60
FEATURE [Part::Cone] Cone  label="csink-1"
  Angle = 360
  AttacherType = Attacher::AttachEngine3D
  Height = 2.5
  Placement = pos=(-9,0,-7) rot=(0,-1,0;1.5708rad)
  Radius1 = 1.7
  Radius2 = 3
FEATURE [Part::Cone] Cone013  label="csink-2"
  Angle = 360
  AttacherType = Attacher::AttachEngine3D
  Height = 2.5
  Placement = pos=(-9,27,-19) rot=(0,-1,0;1.5708rad)
  Radius1 = 1.7
  Radius2 = 3
FEATURE [Part::Cone] Cone014  label="csink-3"
  Angle = 360
  AttacherType = Attacher::AttachEngine3D
  Height = 2.5
  Placement = pos=(-9,-27,-19) rot=(0,-1,0;1.5708rad)
  Radius1 = 1.7
  Radius2 = 3
FEATURE [Part::Cone] Cone015  label="csink-4"
  Angle = 360
  AttacherType = Attacher::AttachEngine3D
  Height = 2.5
  Placement = pos=(-9,-27,-39) rot=(0,-1,0;1.5708rad)
  Radius1 = 1.7
  Radius2 = 3
FEATURE [Part::Sphere] Sphere006006006006010  label="ball-r-32-a-change-radius-here"
  Angle1 = -90
  Angle2 = 90
  Angle3 = 360
  AttacherType = Attacher::AttachEngine3D
  Placement = pos=(-15,-20,-5) rot=(0,0,1;0rad)
  Radius = 3.2
FEATURE [Part::Box] Box112015002017004007004038046  label="Cube133"
  AttacherType = Attacher::AttachEngine3D
  Height = 50
  Length = 37
  Placement = pos=(-33.5,-32,-47) rot=(0,-1,0;0.785398rad)
  Width = 66
FEATURE [Part::Box] Box112015002017004007004038048  label="Cube135"
  AttacherType = Attacher::AttachEngine3D
  Height = 12
  Length = 12
  Placement = pos=(-23,-30,-12) rot=(0,0,1;0rad)
  Width = 60
FEATURE [Part::Cut] Cut360
  Base = -> Box112015002017004007004038048
  Tool = -> Box112015002017004007004038046
FEATURE [Part::Box] Box112015002017004007004038049  label="Cube136"
  AttacherType = Attacher::AttachEngine3D
  Height = 5
  Length = 4
  Placement = pos=(-21.2,-30,-5) rot=(0,0,1;0rad)
  Width = 20
FEATURE [Part::Cylinder] Cylinder054072  label="M2.5-1"
  Angle = 360
  AttacherType = Attacher::AttachEngine3D
  Height = 100
  Placement = pos=(-40,-26,-2.5) rot=(0,1,0;1.5708rad)
  Radius = 1.3
FEATURE [Part::Cylinder] Cylinder054073  label="M2.5-2"
  Angle = 360
  AttacherType = Attacher::AttachEngine3D
  Height = 100
  Placement = pos=(-40,-14,-2.5) rot=(0,1,0;1.5708rad)
  Radius = 1.3
FEATURE [Part::Cylinder] Cylinder054074  label="M2.5-tap-1"
  Angle = 360
  AttacherType = Attacher::AttachEngine3D
  Height = 100
  Placement = pos=(-40,-26,-2.5) rot=(0,1,0;1.5708rad)
  Radius = 1
FEATURE [Part::Cylinder] Cylinder054075  label="M2.5-tap-2"
  Angle = 360
  AttacherType = Attacher::AttachEngine3D
  Height = 100
  Placement = pos=(-40,-14,-2.5) rot=(0,1,0;1.5708rad)
  Radius = 1
FEATURE [Part::Mirroring] Part__Mirroring005013  label="ball-r-305 (Mirror #9)"
  Base = (0,0,0)
  Normal = (0,1,0)
  Placement = pos=(-6,0,0) rot=(0,0,1;0rad)
  Source = -> Sphere006006006006010
FEATURE [Part::Mirroring] Part__Mirroring005016  label="M2.5-tap-1 (Mirror #12)-xxx "
  Base = (0,0,0)
  Normal = (0,1,0)
  Placement = pos=(0,0,23) rot=(0,0,1;0rad)
  Source = -> Cylinder054074
FEATURE [Part::Mirroring] Part__Mirroring005017  label="M2.5-tap-2 (Mirror #13)-xxx"
  Base = (0,0,0)
  Normal = (0,1,0)
  Placement = pos=(0,0,23) rot=(0,0,1;0rad)
  Source = -> Cylinder054075
FEATURE [Part::Sphere] Sphere006006006006011  label="ball-r-32-b-change-radius-here"
  Angle1 = -90
  Angle2 = 90
  Angle3 = 360
  AttacherType = Attacher::AttachEngine3D
  Placement = pos=(-21,-20,-5) rot=(0,0,1;0rad)
  Radius = 3.2
FEATURE [Part::Cylinder] Cylinder054078  label="M2.5-tap-003-xxx"
  Angle = 360
  AttacherType = Attacher::AttachEngine3D
  Height = 100
  Placement = pos=(-40,-26,20.5) rot=(0,1,0;1.5708rad)
  Radius = 1
FEATURE [Part::Cylinder] Cylinder054079  label="M2.5-tap-004-xxx"
  Angle = 360
  AttacherType = Attacher::AttachEngine3D
  Height = 100
  Placement = pos=(-40,-14,20.5) rot=(0,1,0;1.5708rad)
  Radius = 1
FEATURE [Part::Cylinder] Cylinder054080  label="mounting-hole-009"
  Angle = 360
  AttacherType = Attacher::AttachEngine3D
  Height = 16
  Placement = pos=(-27,0,-7) rot=(0,1,0;1.5708rad)
  Radius = 3
FEATURE [Part::Fuse] Fusion051010010012015014049
  Base = -> Box112015002017004007004038045
  Tool = -> Cut360
FEATURE [Part::Cut] Cut361
  Base = -> Fusion051010010012015014049
  Tool = -> Cylinder054080
FEATURE [Part::Cylinder] Cylinder054081  label="mounting-hole-010"
  Angle = 360
  AttacherType = Attacher::AttachEngine3D
  Height = 100
  Placement = pos=(-40,0,-7) rot=(0,1,0;1.5708rad)
  Radius = 1.7
FEATURE [Part::Cylinder] Cylinder054082  label="mounting-hole-011"
  Angle = 360
  AttacherType = Attacher::AttachEngine3D
  Height = 100
  Placement = pos=(-40,-27,-19) rot=(0,1,0;1.5708rad)
  Radius = 1.7
FEATURE [Part::Cone] Cone016  label="csink-005"
  Angle = 360
  AttacherType = Attacher::AttachEngine3D
  Height = 2.5
  Placement = pos=(-9,-27,-19) rot=(0,-1,0;1.5708rad)
  Radius1 = 1.7
  Radius2 = 3
FEATURE [Part::Cylinder] Cylinder054083  label="mounting-hole-012"
  Angle = 360
  AttacherType = Attacher::AttachEngine3D
  Height = 100
  Placement = pos=(-40,27,-19) rot=(0,1,0;1.5708rad)
  Radius = 1.7
FEATURE [Part::Cone] Cone018  label="csink-007"
  Angle = 360
  AttacherType = Attacher::AttachEngine3D
  Height = 2.5
  Placement = pos=(-9,27,-19) rot=(0,-1,0;1.5708rad)
  Radius1 = 1.7
  Radius2 = 3
FEATURE [Part::Cone] Cone019  label="csink-008"
  Angle = 360
  AttacherType = Attacher::AttachEngine3D
  Height = 2.5
  Placement = pos=(-9,0,-7) rot=(0,-1,0;1.5708rad)
  Radius1 = 1.7
  Radius2 = 3
FEATURE [Part::Cut] Cut362
  Base = -> Cut361
  Tool = -> Cylinder054081
FEATURE [Part::Cut] Cut363
  Base = -> Cut362
  Tool = -> Cylinder054082
FEATURE [Part::Cut] Cut364
  Base = -> Cut363
  Tool = -> Cylinder054083
FEATURE [Part::Cut] Cut365
  Base = -> Cut364
  Tool = -> Cone016
FEATURE [Part::Cut] Cut366
  Base = -> Cut365
  Tool = -> Cone018
FEATURE [Part::Cut] Cut367
  Base = -> Cut366
  Tool = -> Cone019
FEATURE [Part::Sphere] Sphere006006006006012  label="ball-r-307"
  Angle1 = -90
  Angle2 = 90
  Angle3 = 360
  AttacherType = Attacher::AttachEngine3D
  Placement = pos=(-15,-20,-5) rot=(0,0,1;0rad)
  Radius = 3.05
FEATURE [Part::Cut] Cut368
  Base = -> Cut367
  Tool = -> Part__Mirroring005013
FEATURE [Part::Cut] Cut369
  Base = -> Cut368
  Tool = -> Sphere006006006006011
FEATURE [Part::Cut] Cut370
  Base = -> Cut369
  Tool = -> Part__Mirroring005016
FEATURE [Part::Cut] Cut371
  Base = -> Cut370
  Tool = -> Part__Mirroring005017
FEATURE [Part::Cut] Cut372
  Base = -> Cut371
  Tool = -> Cylinder054078
FEATURE [Part::Cut] Cut373  label="ball-socket-slider-b"
  Base = -> Cut372
  Tool = -> Cylinder054079
FEATURE [Part::Box] Box112015002017004007004038050  label="Cube137"
  AttacherType = Attacher::AttachEngine3D
  Height = 30
  Length = 100
  Placement = pos=(-100,0,-300) rot=(0,0,1;0rad)
  Width = 30
FEATURE [Part::Box] Box112015002017004007004038051  label="Cube138"
  AttacherType = Attacher::AttachEngine3D
  Height = 35
  Length = 103
  Placement = pos=(-101,-1,-301) rot=(1,0,0;0.785398rad)
  Width = 56
FEATURE [Part::Cut] Cut380
  Base = -> Box112015002017004007004038050
  Tool = -> Box112015002017004007004038051
FEATURE [Part::Box] Box112015002017004007004038052  label="Cube139"
  AttacherType = Attacher::AttachEngine3D
  Height = 30
  Length = 103
  Placement = pos=(-101,3,-275) rot=(0,0,1;0rad)
  Width = 30
FEATURE [Part::Box] Box112015002017004007004038053  label="Cube140"
  AttacherType = Attacher::AttachEngine3D
  Height = 30
  Length = 103
  Placement = pos=(-101,-25,-301) rot=(0,0,1;0rad)
  Width = 30
FEATURE [Part::Cut] Cut381
  Base = -> Cut380
  Tool = -> Box112015002017004007004038053
FEATURE [Part::Cut] Cut382
  Base = -> Cut381
  Placement = pos=(19,-45,0) rot=(0,0,1;0.523599rad)
  Tool = -> Box112015002017004007004038052
FEATURE [Part::Chamfer] Chamfer006012040
  Base = -> Cut382
  Edges = 1 edges r=20: [Edge9]
  Placement = pos=(0,0,1) rot=(0,0,1;0rad)
FEATURE [Part::Box] Box112015002017004007004038054  label="Cube141"
  AttacherType = Attacher::AttachEngine3D
  Height = 52
  Length = 32
  Placement = pos=(-11,-30,-308) rot=(0,0,1;0rad)
  Width = 60
FEATURE [Part::Cylinder] Cylinder054084  label="Cylinder"
  Angle = 360
  AttacherType = Attacher::AttachEngine3D
  Height = 50
  Placement = pos=(-6,-16,-286) rot=(1,0,0;1.5708rad)
  Radius = 1.3
FEATURE [Part::Cylinder] Cylinder054085  label="Cylinder054104"
  Angle = 360
  AttacherType = Attacher::AttachEngine3D
  Height = 50
  Placement = pos=(-6,-16,-296.5) rot=(1,0,0;1.5708rad)
  Radius = 1.3
FEATURE [Part::Cylinder] Cylinder054086  label="Cylinder054105"
  Angle = 360
  AttacherType = Attacher::AttachEngine3D
  Height = 50
  Placement = pos=(-6,-16,-286) rot=(1,0,0;1.5708rad)
  Radius = 1.7
FEATURE [Part::Cylinder] Cylinder054087  label="Cylinder054106"
  Angle = 360
  AttacherType = Attacher::AttachEngine3D
  Height = 50
  Placement = pos=(-6,-16,-296.5) rot=(1,0,0;1.5708rad)
  Radius = 1.7
FEATURE [Part::Cylinder] Cylinder054088  label="Cylinder054107"
  Angle = 360
  AttacherType = Attacher::AttachEngine3D
  Height = 50
  Placement = pos=(-6,-37,-286) rot=(1,0,0;1.5708rad)
  Radius = 3
FEATURE [Part::Cylinder] Cylinder054089  label="Cylinder054108"
  Angle = 360
  AttacherType = Attacher::AttachEngine3D
  Height = 50
  Placement = pos=(-6,-37,-296.5) rot=(1,0,0;1.5708rad)
  Radius = 3
FEATURE [Part::Cylinder] Cylinder054090  label="Cylinder054109"
  Angle = 360
  AttacherType = Attacher::AttachEngine3D
  Height = 50
  Placement = pos=(-6,-16,-286) rot=(1,0,0;1.5708rad)
  Radius = 1.3
FEATURE [Part::Cylinder] Cylinder054091  label="Cylinder054110"
  Angle = 360
  AttacherType = Attacher::AttachEngine3D
  Height = 50
  Placement = pos=(-6,-16,-296.5) rot=(1,0,0;1.5708rad)
  Radius = 1.3
FEATURE [Part::Mirroring] Part__Mirroring005019  label="Cylinder054101 (Mirror #15)"
  Base = (0,0,0)
  Normal = (0,1,0)
  Source = -> Cylinder054090
FEATURE [Part::Mirroring] Part__Mirroring005020  label="Cylinder054102 (Mirror #16)"
  Base = (0,0,0)
  Normal = (0,1,0)
  Source = -> Cylinder054091
FEATURE [Part::Cut] Cut388
  Base = -> Fusion051010010012015014048
  Tool = -> Cylinder054084
FEATURE [Part::Cut] Cut389
  Base = -> Cut388
  Tool = -> Cylinder054085
FEATURE [Part::Cut] Cut390
  Base = -> Cut389
  Tool = -> Part__Mirroring005019
FEATURE [Part::Cut] Cut391
  Base = -> Cut390
  Tool = -> Part__Mirroring005020
FEATURE [Part::Cylinder] Cylinder054092  label="Cylinder054111"
  Angle = 360
  AttacherType = Attacher::AttachEngine3D
  Height = 10
  Placement = pos=(11,0,-301) rot=(0,0,1;0rad)
  Radius = 1.3
FEATURE [Part::Cut] Cut392
  Base = -> Cut391
  Tool = -> Cylinder054092
FEATURE [Part::Cylinder] Cylinder054093  label="foot-mount"
  Angle = 360
  AttacherType = Attacher::AttachEngine3D
  Height = 10
  Placement = pos=(11,0,-301) rot=(0,0,1;0rad)
  Radius = 1.3
FEATURE [Part::Cylinder] Cylinder054094  label="top-mount-1"
  Angle = 360
  AttacherType = Attacher::AttachEngine3D
  Height = 10
  Placement = pos=(-1,20,-267) rot=(0,0,1;0rad)
  Radius = 1.3
FEATURE [Part::Cylinder] Cylinder054095  label="foot-mount002"
  Angle = 360
  AttacherType = Attacher::AttachEngine3D
  Height = 16
  Placement = pos=(-1,20,-267) rot=(0,0,1;0rad)
  Radius = 1.3
FEATURE [Part::Mirroring] Part__Mirroring005021  label="top-mount-2"
  Base = (0,0,0)
  Normal = (0,1,0)
  Source = -> Cylinder054095
FEATURE [App::DocumentObjectGroup] Group007  label="Mounting-Holes"
  Group = -> [Cylinder054067,Cylinder054068,Cylinder054069,Cylinder054070,Cone,Cone013,Cone014,Cone015,Cylinder054093,Cylinder054094,Part__Mirroring005021]
FEATURE [Part::Cylinder] Cylinder054096  label="top-mount-003"
  Angle = 360
  AttacherType = Attacher::AttachEngine3D
  Height = 16
  Placement = pos=(-1,20,-272) rot=(0,0,1;0rad)
  Radius = 1.3
FEATURE [Part::Mirroring] Part__Mirroring005022  label="top-mount-004"
  Base = (0,0,0)
  Normal = (0,1,0)
  Placement = pos=(0,0,-5) rot=(0,0,1;0rad)
  Source = -> Cylinder054095
FEATURE [Part::Cut] Cut393
  Base = -> Cut392
  Tool = -> Cylinder054096
FEATURE [Part::Cut] Cut394
  Base = -> Cut393
  Tool = -> Part__Mirroring005022
FEATURE [Part::Chamfer] Chamfer006012041
  Base = -> Cut394
  Edges = 1 edges r=1: [Edge4]
FEATURE [Part::Chamfer] Chamfer006012042  label="bottom-block-8"
  Base = -> Chamfer006012041
  Edges = 1 edges r=1: [Edge3]
FEATURE [Part::Box] Box112015002017004007004038055  label="Cube142"
  AttacherType = Attacher::AttachEngine3D
  Height = 17
  Length = 30
  Placement = pos=(-121,-38.5,-299) rot=(0,0,1;0rad)
  Width = 17
FEATURE [Part::Box] Box112015002017004007004038056  label="Cube143"
  AttacherType = Attacher::AttachEngine3D
  Height = 17
  Length = 34
  Placement = pos=(-122,-39.5,-300) rot=(1,0,0;0.785398rad)
  Width = 33
FEATURE [Part::Cut] Cut395
  Base = -> Box112015002017004007004038055
  Placement = pos=(1,0,0) rot=(0,0,1;0rad)
  Tool = -> Box112015002017004007004038056
FEATURE [Part::Box] Box112015002017004007004038057  label="Cube144"
  AttacherType = Attacher::AttachEngine3D
  Height = 17
  Length = 30
  Placement = pos=(-121,-38.7,-298.8) rot=(0,0,1;0rad)
  Width = 17
FEATURE [Part::Box] Box112015002017004007004038058  label="Cube145"
  AttacherType = Attacher::AttachEngine3D
  Height = 17
  Length = 34
  Placement = pos=(-122,-39.5,-300) rot=(1,0,0;0.785398rad)
  Width = 33
FEATURE [Part::Cut] Cut396
  Base = -> Box112015002017004007004038057
  Placement = pos=(0,0.1,-0.1) rot=(0,0,1;0rad)
  Tool = -> Box112015002017004007004038058
FEATURE [Part::Cylinder] Cylinder054097  label="Cylinder054112"
  Angle = 360
  AttacherType = Attacher::AttachEngine3D
  Height = 30
  Placement = pos=(-99,-24,-296) rot=(1,0,0;0.785398rad)
  Radius = 1.3
FEATURE [Part::Box] Box112015002017004007004038059  label="Cube146"
  AttacherType = Attacher::AttachEngine3D
  Height = 10
  Length = 8
  Placement = pos=(-100,-1.5,-300) rot=(1,0,0;0.785398rad)
  Width = 3
FEATURE [Part::Fillet] Fillet
  Base = -> Box112015002017004007004038059
  Edges = 1 edges r=1.4: [Edge3]
FEATURE [Part::Fillet] Fillet001
  Base = -> Fillet
  Edges = 1 edges r=1.4: [Edge3]
FEATURE [Part::Fillet] Fillet002
  Base = -> Fillet001
  Edges = 1 edges r=1.4: [Edge18]
FEATURE [Part::Fillet] Fillet003
  Base = -> Fillet002
  Edges = 1 edges r=1.4: [Edge15]
  Placement = pos=(-3,-28,7.3) rot=(0,0,1;0rad)
FEATURE [Part::Cylinder] Cylinder054098  label="Cylinder054113"
  Angle = 360
  AttacherType = Attacher::AttachEngine3D
  Height = 30
  Placement = pos=(-113,-24,-296) rot=(1,0,0;0.785398rad)
  Radius = 1.3
FEATURE [Part::Cut] Cut398
  Base = -> Cut396
  Tool = -> Cylinder054097
FEATURE [Part::Cut] Cut399  label="base-joiner-1"
  Base = -> Cut398
  Tool = -> Cylinder054098
FEATURE [Part::Cylinder] Cylinder054099  label="Cylinder054114"
  Angle = 360
  AttacherType = Attacher::AttachEngine3D
  Height = 10
  Placement = pos=(0,0,0) rot=(0,1,0;1.53589rad)
  Radius = 1.5
FEATURE [Part::Feature] Cylinder054099001
  Placement = pos=(0,0,0) rot=(-0.355767,0.858898,0.368408;1.68772rad)
  shape: bbox 9.189 x 9.189 x 3.347 mm, 3 faces (baked)
FEATURE [Part::Feature] Cylinder054099002
  Placement = pos=(0,0,0) rot=(-0.570514,0.570514,0.590785;2.07436rad)
  shape: bbox 3 x 10.1 x 3.347 mm, 3 faces (baked)
FEATURE [Part::Feature] Cylinder054099003
  Placement = pos=(0,0,0) rot=(-0.667573,0.276518,0.691292;2.58383rad)
  shape: bbox 9.189 x 9.189 x 3.347 mm, 3 faces (baked)
FEATURE [Part::Feature] Cylinder054099004
  Placement = pos=(0,0,0) rot=(-0.694658,0,0.71934;3.14159rad)
  shape: bbox 10.1 x 3 x 3.347 mm, 3 faces (baked)
FEATURE [Part::Feature] Cylinder054099005
  Placement = pos=(0,0,0) rot=(-0.667573,-0.276518,0.691292;3.69935rad)
  shape: bbox 9.189 x 9.189 x 3.347 mm, 3 faces (baked)
FEATURE [Part::Feature] Cylinder054099006
  Placement = pos=(0,0,0) rot=(0.570514,0.570514,-0.590785;2.07436rad)
  shape: bbox 3 x 10.1 x 3.347 mm, 3 faces (baked)
FEATURE [Part::Feature] Cylinder054099007
  Placement = pos=(0,0,0) rot=(0.355767,0.858898,-0.368408;1.68772rad)
  shape: bbox 9.189 x 9.189 x 3.347 mm, 3 faces (baked)
FEATURE [Part::Fuse] Fusion051010010012015014050
  Base = -> Cylinder054099
  Tool = -> Cylinder054099001
FEATURE [Part::Fuse] Fusion051010010012015014051
  Base = -> Cylinder054099007
  Tool = -> Fusion051010010012015014050
FEATURE [Part::Fuse] Fusion051010010012015014052
  Base = -> Cylinder054099006
  Tool = -> Fusion051010010012015014051
FEATURE [Part::Fuse] Fusion051010010012015014053
  Base = -> Cylinder054099005
  Tool = -> Fusion051010010012015014052
FEATURE [Part::Fuse] Fusion051010010012015014054
  Base = -> Cylinder054099004
  Tool = -> Fusion051010010012015014053
FEATURE [Part::Fuse] Fusion051010010012015014055
  Base = -> Cylinder054099003
  Tool = -> Fusion051010010012015014054
FEATURE [Part::Fuse] Fusion051010010012015014056  label="full-fan"
  Base = -> Cylinder054099002
  Tool = -> Fusion051010010012015014055
FEATURE [Part::Cylinder] Cylinder054099008  label="chop"
  Angle = 360
  AttacherType = Attacher::AttachEngine3D
  Height = 7
  Placement = pos=(0,0,-3) rot=(0,0,1;0rad)
  Radius = 9
FEATURE [Part::Cylinder] Cylinder054099009  label="Cylinder054099008"
  Angle = 360
  AttacherType = Attacher::AttachEngine3D
  Height = 10
  Placement = pos=(0,0,0) rot=(0,1,0;1.53589rad)
  Radius = 1.5
FEATURE [Part::Feature] Cylinder054099009001
  Placement = pos=(0,0,0) rot=(-0.2112,0.952661,0.218704;1.58438rad)
  shape: bbox 10.33 x 6.943 x 3.347 mm, 3 faces (baked)
FEATURE [Part::Feature] Cylinder054099009002
  Placement = pos=(0,0,0) rot=(-0.387166,0.83028,0.400922;1.7213rad)
  shape: bbox 8.723 x 9.586 x 3.347 mm, 3 faces (baked)
FEATURE [Part::Feature] Cylinder054099009003
  Placement = pos=(0,0,0) rot=(-0.514977,0.671131,0.533274;1.9269rad)
  shape: bbox 5.485 x 10.44 x 3.347 mm, 3 faces (baked)
FEATURE [Part::Feature] Cylinder054099009004
  Placement = pos=(0,0,0) rot=(-0.600148,0.503584,0.621471;2.18023rad)
  shape: bbox 4.69 x 10.37 x 3.347 mm, 3 faces (baked)
FEATURE [Part::Feature] Cylinder054099009005
  Placement = pos=(0,0,0) rot=(-0.653258,0.340065,0.676469;2.46442rad)
  shape: bbox 8.19 x 9.909 x 3.347 mm, 3 faces (baked)
FEATURE [Part::Cylinder] Cylinder054099009006
  Angle = 360
  AttacherType = Attacher::AttachEngine3D
  Height = 10
  Placement = pos=(0,0,0) rot=(0.650802,0.391041,-0.650802;2.39607rad)
  Radius = 1.5
FEATURE [Part::Fuse] Fusion051010010012015014057
  Base = -> Cylinder054099009
  Tool = -> Cylinder054099009001
FEATURE [Part::Fuse] Fusion051010010012015014058
  Base = -> Cylinder054099009006
  Tool = -> Fusion051010010012015014057
FEATURE [Part::Fuse] Fusion051010010012015014059
  Base = -> Cylinder054099009005
  Tool = -> Fusion051010010012015014058
FEATURE [Part::Fuse] Fusion051010010012015014060
  Base = -> Cylinder054099009004
  Tool = -> Fusion051010010012015014059
FEATURE [Part::Fuse] Fusion051010010012015014061
  Base = -> Cylinder054099009003
  Tool = -> Fusion051010010012015014060
FEATURE [Part::Fuse] Fusion051010010012015014062  label="half-fan"
  Base = -> Cylinder054099009002
  Tool = -> Fusion051010010012015014061
FEATURE [App::DocumentObjectGroup] Group009  label="Glue-trees"
  Group = -> [Cylinder054099008,Fusion051010010012015014062,Fusion051010010012015014056]
FEATURE [Part::Fuse] Fusion051010010012015014063  label="full-fan001"
  Base = -> Cylinder054099002
  Placement = pos=(-98,-30,-300) rot=(0,0,1;0rad)
  Tool = -> Fusion051010010012015014055
FEATURE [Part::Cylinder] Cylinder054099009007  label="chop001"
  Angle = 360
  AttacherType = Attacher::AttachEngine3D
  Height = 7
  Placement = pos=(-98,-30,-302) rot=(0,0,1;0rad)
  Radius = 7
FEATURE [Part::Fuse] Fusion051010010012015014064  label="half-fan001"
  Base = -> Cylinder054099009002
  Placement = pos=(-100,-22.8,-286) rot=(0.173624,0.696367,-0.696367;2.79778rad)
  Tool = -> Fusion051010010012015014061
FEATURE [Part::MultiCommon] Common
  Placement = pos=(0,0,2) rot=(0,0,1;0rad)
  Shapes = -> [Fusion051010010012015014063,Cylinder054099009007]
FEATURE [Part::Box] Box112015002017004007004038060  label="Cube147"
  AttacherType = Attacher::AttachEngine3D
  Height = 17
  Length = 34
  Placement = pos=(-122,-39.5,-301) rot=(1,0,0;0.785398rad)
  Width = 33
FEATURE [Part::Cut] Cut401
  Base = -> Common
  Tool = -> Box112015002017004007004038060
FEATURE [Part::Cone] Cone020  label="Cone"
  Angle = 360
  AttacherType = Attacher::AttachEngine3D
  Height = 5
  Placement = pos=(-100,-23,-281) rot=(0,0,1;0rad)
  Radius1 = 1
  Radius2 = 4
FEATURE [Part::Feature] Face006
  Placement = pos=(-1,0,0) rot=(0,0,1;0rad)
  shape: bbox 3.013 x 2.824 x 2e-07 mm, 1 faces, 0 solids (baked)
FEATURE [Part::Feature] Shape010
  shape: bbox 7.692 x 7.113 x 20 mm, 0 faces, 0 solids (baked)
FEATURE [Part::Cylinder] Cylinder054099009008  label="Cylinder054099009007"
  Angle = 360
  AttacherType = Attacher::AttachEngine3D
  Height = 8
  Placement = pos=(-100,-20,-300) rot=(0,1,0;1.5708rad)
  Radius = 1.3
FEATURE [Part::Chamfer] Chamfer006012043
  Base = -> Cylinder054099009008
  Edges = 1 edges r=1: [Edge3]
FEATURE [Part::Chamfer] Chamfer006012044
  Base = -> Chamfer006012043
  Edges = 1 edges r=1: [Edge3]
  Placement = pos=(-3,-2,17) rot=(0,0,1;0rad)
FEATURE [Part::Sweep] Sweep008
  Frenet = false
  Sections = -> [Face006]
  Solid = true
  Spine = -> Shape010 [Edge1]
  Transition = 1
FEATURE [Part::Fuse] Fusion051010010012015014065  label="glue-path"
  Base = -> Chamfer006012044
  Tool = -> Sweep008
FEATURE [Part::Fuse] Fusion051010010012015014066  label="glue-path001"
  Base = -> Chamfer006012044
  Tool = -> Sweep008
FEATURE [Part::Mirroring] Part__Mirroring005023  label="glue-path (Mirror #19)"
  Base = (-106,0,0)
  Normal = (1,0,0)
  Source = -> Fusion051010010012015014065
FEATURE [Part::Cut] Cut405
  Base = -> Cut399
  Tool = -> Fusion051010010012015014066
FEATURE [Part::Cut] Cut406  label="6132 base joiner"
  Base = -> Cut405
  Placement = pos=(0,0,0) rot=(0,0,1;0.523599rad)
  Tool = -> Part__Mirroring005023
FEATURE [Part::Box] Box112015002017004007004038061  label="Cube148"
  AttacherType = Attacher::AttachEngine3D
  Height = 15
  Length = 97
  Placement = pos=(-106,-39,105) rot=(0,0,1;0rad)
  Width = 20
FEATURE [Part::Chamfer] Chamfer006012045
  Base = -> Box112015002017004007004038061
  Edges = 1 edges r=13: [Edge9]
FEATURE [Part::Box] Box112015002017004007004038062  label="Cube149"
  AttacherType = Attacher::AttachEngine3D
  Height = 15
  Length = 30
  Placement = pos=(-120,-42,102) rot=(0,0,1;0rad)
  Width = 20
FEATURE [Part::Box] Box112015002017004007004038063  label="Cube150"
  AttacherType = Attacher::AttachEngine3D
  Height = 20
  Length = 35
  Placement = pos=(-123,-42,124) rot=(-1,0,0;0.785398rad)
  Width = 30
FEATURE [Part::MultiCommon] Common011
  Shapes = -> [Box112015002017004007004038062,Box112015002017004007004038063]
FEATURE [Part::Box] Box112015002017004007004038066  label="Cube153"
  AttacherType = Attacher::AttachEngine3D
  Height = 15
  Length = 34
  Placement = pos=(-123,-37,108) rot=(0,0,1;0rad)
  Width = 20
FEATURE [Part::MultiCommon] Common012
  Shapes = -> [Common011,Box112015002017004007004038066]
FEATURE [Part::Box] Box112015002017004007004038067  label="Cube154"
  AttacherType = Attacher::AttachEngine3D
  Height = 15
  Length = 30
  Placement = pos=(-120,-42.2,101.8) rot=(0,0,1;0rad)
  Width = 20
FEATURE [Part::Box] Box112015002017004007004038068  label="Cube155"
  AttacherType = Attacher::AttachEngine3D
  Height = 20
  Length = 35
  Placement = pos=(-123,-42,124) rot=(-1,0,0;0.785398rad)
  Width = 30
FEATURE [Part::MultiCommon] Common013
  Shapes = -> [Box112015002017004007004038067,Box112015002017004007004038068]
FEATURE [Part::Box] Box112015002017004007004038069  label="Cube156"
  AttacherType = Attacher::AttachEngine3D
  Height = 15
  Length = 34
  Placement = pos=(-123,-37,108) rot=(0,0,1;0rad)
  Width = 20
FEATURE [Part::MultiCommon] Common014
  Placement = pos=(-1,0,0) rot=(0,0,1;0rad)
  Shapes = -> [Common013,Box112015002017004007004038069]
FEATURE [Part::Cut] Cut407
  Base = -> Chamfer006012045
  Tool = -> Common012
FEATURE [Part::Box] Box112015002017004007004038070  label="Cube157"
  AttacherType = Attacher::AttachEngine3D
  Height = 10
  Length = 8
  Placement = pos=(-100,-31,119) rot=(0,0,1;0rad)
  Width = 3
FEATURE [Part::Fillet] Fillet004
  Base = -> Box112015002017004007004038070
  Edges = 1 edges r=1.4: [Edge1]
FEATURE [Part::Fillet] Fillet005
  Base = -> Fillet004
  Edges = 1 edges r=1.4: [Edge3]
FEATURE [Part::Fillet] Fillet006
  Base = -> Fillet005
  Edges = 1 edges r=1.4: [Edge18]
FEATURE [Part::Fillet] Fillet007
  Base = -> Fillet006
  Edges = 1 edges r=1.4: [Edge15]
  Placement = pos=(-3,2,-4) rot=(0,0,1;0rad)
FEATURE [Part::Cylinder] Cylinder054099009009  label="Cylinder054099009137092"
  Angle = 360
  AttacherType = Attacher::AttachEngine3D
  Height = 20
  Placement = pos=(-99,-27.5,103) rot=(0,0,1;0rad)
  Radius = 1.3
FEATURE [Part::Cut] Cut408
  Base = -> Cut407
  Tool = -> Fillet007
FEATURE [Part::Fuse] Fusion051010010012015014067  label="full-fan002"
  Base = -> Cylinder054099002
  Placement = pos=(-99,-28,112) rot=(-1,0,0;0.785398rad)
  Tool = -> Fusion051010010012015014055
FEATURE [Part::Cylinder] Cylinder054099009010  label="chop002"
  Angle = 360
  AttacherType = Attacher::AttachEngine3D
  Height = 7
  Placement = pos=(-99,-31.1213,109.879) rot=(-1,0,0;0.785398rad)
  Radius = 5
FEATURE [Part::Fuse] Fusion051010010012015014068  label="half-fan002"
  Base = -> Cylinder054099009002
  Placement = pos=(-97,-23,115) rot=(0.173624,0.696367,-0.696367;2.79777rad)
  Tool = -> Fusion051010010012015014061
FEATURE [Part::MultiCommon] Common015
  Placement = pos=(0,-0.2,0) rot=(0,0,1;0rad)
  Shapes = -> [Fusion051010010012015014067,Cylinder054099009010]
FEATURE [Part::Cylinder] Cylinder054099009011  label="Cylinder054099009137050"
  Angle = 360
  AttacherType = Attacher::AttachEngine3D
  Height = 10
  Placement = pos=(-97,-20,115) rot=(1,0,0;1.5708rad)
  Radius = 6
FEATURE [Part::MultiCommon] Common016
  Shapes = -> [Fusion051010010012015014068,Cylinder054099009011]
FEATURE [Part::Box] Box112015002017004007004038071  label="Cube158"
  AttacherType = Attacher::AttachEngine3D
  Height = 10
  Length = 10
  Placement = pos=(-103,-35,116) rot=(0,0,1;0rad)
  Width = 10
FEATURE [Part::Cut] Cut410
  Base = -> Common015
  Placement = pos=(3,0,0) rot=(0,0,1;0rad)
  Tool = -> Box112015002017004007004038071
FEATURE [Part::Cut] Cut411
  Base = -> Cut408
  Tool = -> Cut410
FEATURE [Part::Cut] Cut412
  Base = -> Cut411
  Placement = pos=(0,0,0) rot=(0,0,1;0.523599rad)
  Tool = -> Common016
FEATURE [Part::Circle] Circle004
  Angle0 = 0
  Angle1 = 360
  AttacherType = Attacher::AttachEngine3D
  Placement = pos=(-97,-23,117) rot=(0,0,1;0rad)
  Radius = 1.3
FEATURE [Part::Feature] Shape011
  shape: bbox 4.048 x 6 x 6 mm, 0 faces, 0 solids (baked)
FEATURE [Part::Feature] Face007
  Placement = pos=(41.4724,0,54.3631) rot=(0,-1,0;0.453786rad)
  shape: bbox 2.708 x 2.824 x 1.321 mm, 1 faces, 0 solids (baked)
FEATURE [Part::Feature] Shape012
  shape: bbox 4.241 x 6.5 x 7 mm, 0 faces, 0 solids (baked)
FEATURE [Part::Sweep] Sweep009
  Frenet = false
  Sections = -> [Face007]
  Solid = true
  Spine = -> Shape012 [Edge1]
  Transition = 1
FEATURE [Part::Fuse] Fusion051010010012015014069  label="top-wedge-holes"
  Base = -> Cylinder054099009009
  Tool = -> Sweep009
FEATURE [Part::Mirroring] Part__Mirroring005024  label="top-wedge-holes (Mirror #20)"
  Base = (-106,0,0)
  Normal = (1,0,0)
  Source = -> Fusion051010010012015014069
FEATURE [Part::Fuse] Fusion051010010012015014070  label="top-wedge-holes001"
  Base = -> Cylinder054099009009
  Tool = -> Sweep009
FEATURE [Part::Cut] Cut413
  Base = -> Common014
  Tool = -> Part__Mirroring005024
FEATURE [Part::Cut] Cut414  label="6136 top joiner"
  Base = -> Cut413
  Placement = pos=(0,0,0) rot=(0,0,1;0.523599rad)
  Tool = -> Fusion051010010012015014070
FEATURE [Part::Chamfer] Chamfer006012046
  Base = -> Cut412
  Edges = 1 edges r=15: [Edge10]
FEATURE [Part::Box] Box112015002017004007004038072  label="Cube159"
  AttacherType = Attacher::AttachEngine3D
  Height = 26
  Length = 22
  Placement = pos=(-11,-30,101) rot=(0,0,1;0rad)
  Width = 22
FEATURE [Part::Cut] Cut415
  Base = -> Chamfer006012046
  Tool = -> Box112015002017004007004038072
FEATURE [Part::Chamfer] Chamfer006012047
  Base = -> Cut359
  Edges = 1 edges r=1: [Edge1]
FEATURE [Part::Chamfer] Chamfer006012048
  Base = -> Chamfer006012047
  Edges = 1 edges r=1: [Edge3]
FEATURE [Part::Cylinder] Cylinder054099009012  label="Cylinder054099009137051"
  Angle = 360
  AttacherType = Attacher::AttachEngine3D
  Height = 50
  Placement = pos=(-6,-16,111) rot=(1,0,0;1.5708rad)
  Radius = 1.3
FEATURE [Part::Cylinder] Cylinder054099009013  label="Cylinder054099009120"
  Angle = 360
  AttacherType = Attacher::AttachEngine3D
  Height = 50
  Placement = pos=(-6,-19,111) rot=(1,0,0;1.5708rad)
  Radius = 1.7
FEATURE [Part::Cylinder] Cylinder054099009014  label="Cylinder054099009138"
  Angle = 360
  AttacherType = Attacher::AttachEngine3D
  Height = 50
  Placement = pos=(-6,-36,111) rot=(1,0,0;1.5708rad)
  Radius = 3
FEATURE [Part::Cylinder] Cylinder054099009015  label="Cylinder054099009122"
  Angle = 360
  AttacherType = Attacher::AttachEngine3D
  Height = 50
  Placement = pos=(-4,-16,111) rot=(1,0,0;1.5708rad)
  Radius = 1.3
FEATURE [Part::Mirroring] Part__Mirroring005025  label="Cylinder054099009020 (Mirror #21)"
  Base = (0,0,0)
  Normal = (0,1,0)
  Placement = pos=(-2,0,0) rot=(0,0,1;0rad)
  Source = -> Cylinder054099009015
FEATURE [Part::Cut] Cut416
  Base = -> Chamfer006012048
  Tool = -> Cylinder054099009012
FEATURE [Part::Cut] Cut417  label="6139 top block"
  Base = -> Cut416
  Tool = -> Part__Mirroring005025
FEATURE [Part::Cut] Cut418
  Base = -> Cut415
  Tool = -> Cylinder054099009013
FEATURE [Part::Cut] Cut419  label="top-arm-1"
  Base = -> Cut418
  Placement = pos=(0,0,0) rot=(0,0,-1;0.523599rad)
  Tool = -> Cylinder054099009014
FEATURE [Part::Chamfer] Chamfer006012049
  Base = -> Chamfer006012042
  Edges = 1 edges r=1: [Edge1]
FEATURE [Part::Box] Box112015002017004007004038073  label="Cube160"
  AttacherType = Attacher::AttachEngine3D
  Height = 20
  Length = 39
  Placement = pos=(-36,-25,-264) rot=(0,0,1;0rad)
  Width = 50
FEATURE [Part::Box] Box112015002017004007004038074  label="Cube161"
  AttacherType = Attacher::AttachEngine3D
  Height = 26
  Length = 39
  Placement = pos=(-8,-10,-267) rot=(0,0,1;0rad)
  Width = 20
FEATURE [Part::Cut] Cut420
  Base = -> Box112015002017004007004038073
  Tool = -> Box112015002017004007004038074
FEATURE [Part::Box] Box112015002017004007004038075  label="Cube162"
  AttacherType = Attacher::AttachEngine3D
  Height = 20
  Length = 39
  Placement = pos=(-11,-26,-278) rot=(0,0,1;0rad)
  Width = 53
FEATURE [Part::Cut] Cut421
  Base = -> Cut420
  Tool = -> Box112015002017004007004038075
FEATURE [Part::Cylinder] Cylinder054099009016  label="top-mount-005"
  Angle = 360
  AttacherType = Attacher::AttachEngine3D
  Height = 47
  Placement = pos=(-1,20,-267) rot=(0,0,1;0rad)
  Radius = 1.7
FEATURE [Part::Cylinder] Cylinder054099009017  label="top-mount-006"
  Angle = 360
  AttacherType = Attacher::AttachEngine3D
  Height = 47
  Placement = pos=(-1,20,-267) rot=(0,0,1;0rad)
  Radius = 1.7
FEATURE [Part::Mirroring] Part__Mirroring005026  label="top-mount-006 (Mirror #22)"
  Base = (0,0,0)
  Normal = (0,1,0)
  Source = -> Cylinder054099009017
FEATURE [Part::Cut] Cut422
  Base = -> Cut421
  Tool = -> Cylinder054099009016
FEATURE [Part::Cut] Cut423
  Base = -> Cut422
  Tool = -> Part__Mirroring005026
FEATURE [Part::Box] Box112015002017004007004038076  label="Cube163"
  AttacherType = Attacher::AttachEngine3D
  Height = 26
  Length = 39
  Placement = pos=(-15,-10,-258) rot=(0,0,1;0rad)
  Width = 20
FEATURE [Part::Box] Box112015002017004007004038077  label="Cube164"
  AttacherType = Attacher::AttachEngine3D
  Height = 32
  Length = 39
  Placement = pos=(-58,-35,-267) rot=(0,0,1;0rad)
  Width = 70
FEATURE [Part::Cut] Cut424
  Base = -> Cut423
  Tool = -> Box112015002017004007004038076
FEATURE [Part::Cut] Cut425
  Base = -> Cut424
  Tool = -> Box112015002017004007004038077
FEATURE [Part::Box] Box112015002017004007004038078  label="Cube165"
  AttacherType = Attacher::AttachEngine3D
  Height = 26
  Length = 63
  Placement = pos=(-38,17,-268) rot=(0,0,1;0.20944rad)
  Width = 20
FEATURE [Part::Box] Box112015002017004007004038079  label="Cube166"
  AttacherType = Attacher::AttachEngine3D
  Height = 26
  Length = 63
  Placement = pos=(-38,17,-268) rot=(0,0,1;0.20944rad)
  Width = 20
FEATURE [Part::Mirroring] Part__Mirroring005027  label="Cube166 (Mirror #23)"
  Base = (0,0,0)
  Normal = (0,1,0)
  Source = -> Box112015002017004007004038079
FEATURE [Part::Cut] Cut426
  Base = -> Cut425
  Tool = -> Box112015002017004007004038078
FEATURE [Part::Cut] Cut427
  Base = -> Cut426
  Tool = -> Part__Mirroring005027
FEATURE [Part::Cylinder] Cylinder054099009018  label="Cylinder054099009139"
  Angle = 360
  AttacherType = Attacher::AttachEngine3D
  Height = 21
  Placement = pos=(-23,4.1,-248) rot=(0,1,0;1.5708rad)
  Radius = 1.7
FEATURE [Part::Cylinder] Cylinder054099009019  label="1253 z-contact-1"
  Angle = 360
  AttacherType = Attacher::AttachEngine3D
  Height = 8
  Placement = pos=(-27,4.1,-247) rot=(0,1,0;1.5708rad)
  Radius = 2.4
FEATURE [Part::Cylinder] Cylinder054099009020  label="cylxxx"
  Angle = 360
  AttacherType = Attacher::AttachEngine3D
  Height = 8
  Placement = pos=(-27,4.1,-248) rot=(0,1,0;1.5708rad)
  Radius = 2.4
FEATURE [Part::Cylinder] Cylinder054099009021  label="Cylinder054099009140"
  Angle = 360
  AttacherType = Attacher::AttachEngine3D
  Height = 21
  Placement = pos=(-23,4.1,-248) rot=(0,1,0;1.5708rad)
  Radius = 1.7
FEATURE [Part::Mirroring] Part__Mirroring005028  label="1253 z-contact-2"
  Base = (0,0,0)
  Normal = (0,1,0)
  Placement = pos=(0,0,1) rot=(0,0,1;0rad)
  Source = -> Cylinder054099009020
FEATURE [Part::Mirroring] Part__Mirroring005029  label="Cylinder054099009026 (Mirror #25)"
  Base = (0,0,0)
  Normal = (0,1,0)
  Source = -> Cylinder054099009021
FEATURE [Part::Cut] Cut428
  Base = -> Cut427
  Tool = -> Cylinder054099009018
FEATURE [Part::Cut] Cut429  label="bed-mount-1"
  Base = -> Cut428
  Tool = -> Part__Mirroring005029
FEATURE [Part::Box] Box112015002017004007004038080  label="Cube167"
  AttacherType = Attacher::AttachEngine3D
  Height = 2.1
  Length = 2.1
  Placement = pos=(-48.3,-62.4808,-297.05) rot=(0,0,1;0.523599rad)
  Width = 12
FEATURE [Part::Box] Box112015002017004007004038081  label="Cube168"
  AttacherType = Attacher::AttachEngine3D
  Height = 2
  Length = 2
  Placement = pos=(-52.6193,-65.0208,-297) rot=(0,0,1;0.523599rad)
  Width = 12
FEATURE [Part::Feature] Face008
  Placement = pos=(0,0,0) rot=(0,0,1;0.523599rad)
  shape: bbox 1.983 x 1.145 x 2.399 mm, 1 faces, 0 solids (baked)
FEATURE [Part::Feature] Face009
  Placement = pos=(-4.39941,-2.54,0) rot=(0,0,1;0.523599rad)
  shape: bbox 1.983 x 1.145 x 2.399 mm, 1 faces, 0 solids (baked)
FEATURE [Part::Feature] Shape022
  shape: bbox 23.66 x 24.7 x 3.257 mm, 0 faces, 0 solids (baked)
FEATURE [Part::Circle] Circle006
  Angle0 = 0
  Angle1 = 360
  AttacherType = Attacher::AttachEngine3D
  Placement = pos=(-8,-8,-249) rot=(0.57735,-0.57735,-0.57735;4.18879rad)
  Radius = 1
FEATURE [Part::Feature] Face010
  shape: bbox 2.373 x 2e-07 x 2.456 mm, 1 faces, 0 solids (baked)
FEATURE [Part::Sweep] Sweep013
  Frenet = false
  Sections = -> [Face009]
  Solid = true
  Spine = -> Shape022 [Edge1]
  Transition = 1
FEATURE [Part::Fuse] Fusion051010010012015014072  label="crimped-base-arm-wire-1"
  Base = -> Box112015002017004007004038081
  Tool = -> Sweep013
FEATURE [Part::Feature] Shape023
  shape: bbox 39 x 33.3 x 15.82 mm, 0 faces, 0 solids (baked)
FEATURE [Part::Sweep] Sweep014
  Frenet = false
  Sections = -> [Face008]
  Solid = true
  Spine = -> Shape023 [Edge1]
  Transition = 1
FEATURE [Part::Fuse] Fusion051010010012015014073  label="crimped-base-arm-wire-2"
  Base = -> Box112015002017004007004038080
  Tool = -> Sweep014
FEATURE [Part::Feature] Shape024
  shape: bbox 39 x 33.3 x 15.82 mm, 0 faces, 0 solids (baked)
FEATURE [Part::Feature] Shape025
  shape: bbox 65.89 x 81 x 49.96 mm, 0 faces, 0 solids (baked)
FEATURE [Part::Feature] Face011
  shape: bbox 2.373 x 2e-07 x 2.456 mm, 1 faces, 0 solids (baked)
FEATURE [Part::Feature] Shape026
  shape: bbox 65.89 x 81 x 49.96 mm, 0 faces, 0 solids (baked)
FEATURE [Part::Feature] Face012
  shape: bbox 2.373 x 2e-07 x 2.456 mm, 1 faces, 0 solids (baked)
FEATURE [Part::Feature] Shape027
  shape: bbox 65.89 x 81 x 49.96 mm, 0 faces, 0 solids (baked)
FEATURE [Part::Feature] Face013
  shape: bbox 2.373 x 2e-07 x 2.456 mm, 1 faces, 0 solids (baked)
FEATURE [Part::Feature] Shape028
  shape: bbox 65.89 x 81 x 49.96 mm, 0 faces, 0 solids (baked)
FEATURE [Part::Feature] Face014
  shape: bbox 2.373 x 2e-07 x 2.456 mm, 1 faces, 0 solids (baked)
FEATURE [Part::Feature] Shape032
  shape: bbox 66.17 x 81 x 49.85 mm, 0 faces, 0 solids (baked)
FEATURE [Part::Sweep] Sweep019
  Frenet = false
  Sections = -> [Face010]
  Solid = true
  Spine = -> Shape032 [Edge1]
  Transition = 1
FEATURE [Part::Cut] Cut432
  Base = -> Chamfer006012049
  Tool = -> Sweep019
FEATURE [Part::Feature] Face015
  shape: bbox 2.373 x 2e-07 x 2.456 mm, 1 faces, 0 solids (baked)
FEATURE [Part::Feature] Shape033
  shape: bbox 66.17 x 81 x 49.85 mm, 0 faces, 0 solids (baked)
FEATURE [Part::Sweep] Sweep020
  Frenet = false
  Sections = -> [Face015]
  Solid = true
  Spine = -> Shape033 [Edge1]
  Transition = 1
FEATURE [Part::Feature] Face016
  shape: bbox 2.373 x 2e-07 x 2.456 mm, 1 faces, 0 solids (baked)
FEATURE [Part::Feature] Shape034
  shape: bbox 66.17 x 81 x 49.85 mm, 0 faces, 0 solids (baked)
FEATURE [Part::Sweep] Sweep021
  Frenet = false
  Sections = -> [Face016]
  Solid = true
  Spine = -> Shape034 [Edge1]
  Transition = 1
FEATURE [Part::Feature] Face017
  shape: bbox 2.373 x 2e-07 x 2.456 mm, 1 faces, 0 solids (baked)
FEATURE [Part::Feature] Shape035
  shape: bbox 66.17 x 81 x 49.85 mm, 0 faces, 0 solids (baked)
FEATURE [Part::Sweep] Sweep022
  Frenet = false
  Sections = -> [Face017]
  Solid = true
  Spine = -> Shape035 [Edge1]
  Transition = 1
FEATURE [Part::Feature] Face018
  shape: bbox 2.373 x 2e-07 x 2.456 mm, 1 faces, 0 solids (baked)
FEATURE [Part::Feature] Shape036
  shape: bbox 66.17 x 81 x 49.85 mm, 0 faces, 0 solids (baked)
FEATURE [Part::Sweep] Sweep023
  Frenet = false
  Sections = -> [Face018]
  Solid = true
  Spine = -> Shape036 [Edge1]
  Transition = 1
FEATURE [Part::Mirroring] Part__Mirroring005030  label="Sweep022 (Mirror #26)"
  Base = (0,0,0)
  Normal = (0,1,0)
  Source = -> Sweep022
FEATURE [Part::Mirroring] Part__Mirroring005031  label="Sweep023 (Mirror #27)"
  Base = (0,0,0)
  Normal = (0,1,0)
  Source = -> Sweep023
FEATURE [Part::Cut] Cut433  label="6138 bottom-block"
  Base = -> Cut432
  Tool = -> Part__Mirroring005030
FEATURE [Part::Cut] Cut434
  Base = -> Cut429
  Tool = -> Sweep020
FEATURE [Part::Cut] Cut435  label="6159 bed mount-xxx"
  Base = -> Cut434
  Tool = -> Part__Mirroring005031
FEATURE [Part::Fuse] Fusion051010010012015014074  label="half-fan-cone"
  Base = -> Fusion051010010012015014064
  Tool = -> Cone020
FEATURE [Part::Cylinder] Cylinder054099009022  label="Cylinder054099009141"
  Angle = 360
  AttacherType = Attacher::AttachEngine3D
  Height = 21
  Placement = pos=(-8,-32,-286) rot=(0,0,1;0rad)
  Radius = 5
FEATURE [Part::Chamfer] Chamfer006012050
  Base = -> Cylinder054099009022
  Edges = 1 edges r=2.7: [Edge1]
  Placement = pos=(0,0,-2) rot=(0,0,1;0rad)
FEATURE [Part::Fuse] Fusion051010010012015014075
  Base = -> Chamfer006012040
  Placement = pos=(0,0,-3) rot=(0,0,1;0rad)
  Tool = -> Chamfer006012050
FEATURE [Part::Cut] Cut436
  Base = -> Fusion051010010012015014075
  Tool = -> Box112015002017004007004038054
FEATURE [Part::Cut] Cut437
  Base = -> Cut436
  Tool = -> Cylinder054086
FEATURE [Part::Cut] Cut438
  Base = -> Cut437
  Tool = -> Cylinder054087
FEATURE [Part::Cut] Cut439
  Base = -> Cut438
  Tool = -> Cylinder054088
FEATURE [Part::Cut] Cut440
  Base = -> Cut439
  Placement = pos=(0,0,0) rot=(0,0,-1;0.523599rad)
  Tool = -> Cylinder054089
FEATURE [Part::Cut] Cut441
  Base = -> Cut440
  Tool = -> Cut395
FEATURE [Part::Cut] Cut442
  Base = -> Cut441
  Tool = -> Fillet003
FEATURE [Part::Cut] Cut443
  Base = -> Cut442
  Tool = -> Cut401
FEATURE [Part::Cut] Cut444
  Base = -> Cut443
  Placement = pos=(0,0,0) rot=(0,0,1;0.523599rad)
  Tool = -> Fusion051010010012015014074
FEATURE [Part::Cut] Cut445
  Base = -> Cut444
  Tool = -> Sweep021
FEATURE [Part::Cut] Cut446
  Base = -> Cut445
  Tool = -> Fusion051010010012015014073
FEATURE [Part::Cut] Cut447  label="base-arm-2"
  Base = -> Cut446
  Placement = pos=(0,0,0) rot=(0,0,-1;0.523599rad)
  Tool = -> Fusion051010010012015014072
FEATURE [Part::Cylinder] Cylinder054099009023  label="Cylinder054099009142"
  Angle = 360
  AttacherType = Attacher::AttachEngine3D
  Height = 20
  Placement = pos=(-50,-12,-280) rot=(0,0,1;0rad)
  Radius = 1.3
FEATURE [Part::Cylinder] Cylinder054099009024  label="Cylinder054099009143"
  Angle = 360
  AttacherType = Attacher::AttachEngine3D
  Height = 20
  Placement = pos=(-50,-1,-270) rot=(1,0,0;1.5708rad)
  Radius = 1.3
FEATURE [Part::Fuse] Fusion051010010012015014079
  Base = -> Cylinder054099009023
  Placement = pos=(-108,-10,-567) rot=(0,1,0;3.14159rad)
  Tool = -> Cylinder054099009024
FEATURE [Part::Fuse] Fusion051010010012015014080
  Base = -> Cylinder054099009023
  Placement = pos=(-133,-10,-567) rot=(0,1,0;3.14159rad)
  Tool = -> Cylinder054099009024
FEATURE [Part::Fuse] Fusion051010010012015014081
  Base = -> Cylinder054099009023
  Placement = pos=(-83,-10,-567) rot=(0,1,0;3.14159rad)
  Tool = -> Cylinder054099009024
FEATURE [Part::Cut] Cut448
  Base = -> Cut447
  Tool = -> Fusion051010010012015014079
FEATURE [Part::Cut] Cut449
  Base = -> Cut448
  Tool = -> Fusion051010010012015014080
FEATURE [Part::Cut] Cut450  label="6131 base arm R"
  Base = -> Cut449
  Placement = pos=(0,0,0) rot=(0,0,1;0.523599rad)
  Tool = -> Fusion051010010012015014081
FEATURE [Part::Cylinder] Cylinder054099009025  label="Cylinder054099009144"
  Angle = 360
  AttacherType = Attacher::AttachEngine3D
  Height = 20
  Placement = pos=(-33,-22,101) rot=(0,0,1;0rad)
  Radius = 1.3
FEATURE [Part::Cylinder] Cylinder054099009026  label="Cylinder054099009145"
  Angle = 360
  AttacherType = Attacher::AttachEngine3D
  Height = 20
  Placement = pos=(-33,-13,115) rot=(1,0,0;1.5708rad)
  Radius = 1.3
FEATURE [Part::Fuse] Fusion051010010012015014082
  Base = -> Cylinder054099009025
  Tool = -> Cylinder054099009026
FEATURE [Part::Fuse] Fusion051010010012015014083
  Base = -> Cylinder054099009025
  Placement = pos=(-50,0,0) rot=(0,0,1;0rad)
  Tool = -> Cylinder054099009026
FEATURE [Part::Fuse] Fusion051010010012015014084
  Base = -> Cylinder054099009025
  Placement = pos=(-25,0,0) rot=(0,0,1;0rad)
  Tool = -> Cylinder054099009026
FEATURE [Part::Cut] Cut451
  Base = -> Cut419
  Tool = -> Fusion051010010012015014082
FEATURE [Part::Cut] Cut452
  Base = -> Cut451
  Tool = -> Fusion051010010012015014084
FEATURE [Part::Cut] Cut453  label="6135 top arm R"
  Base = -> Cut452
  Placement = pos=(0,0,0) rot=(0,0,1;0.523599rad)
  Tool = -> Fusion051010010012015014083
FEATURE [Part::Cone] Cone021  label="Cone013"
  Angle = 360
  AttacherType = Attacher::AttachEngine3D
  Height = 30
  Placement = pos=(11,0,-330) rot=(0,0,1;0rad)
  Radius1 = 4
  Radius2 = 10
FEATURE [Part::Cylinder] Cylinder054099009027  label="Cylinder054099009146"
  Angle = 360
  AttacherType = Attacher::AttachEngine3D
  Height = 15
  Placement = pos=(11,0,-313) rot=(0,0,1;0rad)
  Radius = 1.7
FEATURE [Part::Cylinder] Cylinder054099009028  label="Cylinder054099009147"
  Angle = 360
  AttacherType = Attacher::AttachEngine3D
  Height = 35
  Placement = pos=(11,0,-340) rot=(0,0,1;0rad)
  Radius = 3
FEATURE [Part::Cut] Cut454
  Base = -> Cone021
  Tool = -> Cylinder054099009027
FEATURE [Part::Cut] Cut455  label="6141 foot"
  Base = -> Cut454
  Tool = -> Cylinder054099009028
FEATURE [Part::Cylinder] Cylinder054099009029  label="1262 Heated Bed"
  Angle = 360
  AttacherType = Attacher::AttachEngine3D
  Height = 3
  Placement = pos=(-130,0,-252) rot=(0,0,1;0rad)
  Radius = 82.5
FEATURE [Part::Feature] Part__Feature161  label="hot-end-base"
  Placement = pos=(-120,0,-130) rot=(0,0,1;3.66519rad)
  shape: bbox 64.05 x 65.4 x 25.8 mm, 468 faces (baked)
FEATURE [Part::Sphere] Sphere006006006006014  label="ball-r-3.x-c-change-radius-here"
  Angle1 = -90
  Angle2 = 90
  Angle3 = 360
  AttacherType = Attacher::AttachEngine3D
  Placement = pos=(-15,-20,-5) rot=(0,0,1;0rad)
  Radius = 3.3
FEATURE [Part::Box] Box112015002017004007004038082  label="Cube169"
  AttacherType = Attacher::AttachEngine3D
  Height = 50
  Length = 37
  Placement = pos=(-27.5,-32,-47) rot=(0,-1,0;0.785398rad)
  Width = 66
FEATURE [Part::Box] Box112015002017004007004038083  label="Cube170"
  AttacherType = Attacher::AttachEngine3D
  Height = 12
  Length = 6
  Placement = pos=(-17,-30,-12) rot=(0,0,1;0rad)
  Width = 60
FEATURE [Part::Cut] Cut456
  Base = -> Box112015002017004007004038083
  Placement = pos=(-110,0,-130) rot=(0,1,0;3.14159rad)
  Tool = -> Box112015002017004007004038082
FEATURE [Part::Mirroring] Part__Mirroring005032  label="ball-r-3.x-c"
  Base = (0,0,0)
  Normal = (0,1,0)
  Placement = pos=(-110,0,-130) rot=(0,1,0;3.14159rad)
  Source = -> Sphere006006006006014
FEATURE [Part::Sphere] Sphere006006006006015  label="ball-r-3.x-d-change-radius-here"
  Angle1 = -90
  Angle2 = 90
  Angle3 = 360
  AttacherType = Attacher::AttachEngine3D
  Placement = pos=(-95,-20,-125) rot=(0,1,0;3.14159rad)
  Radius = 3.3
FEATURE [Part::Feature] Cut456001
  Placement = pos=(-125,8.66025,-130) rot=(0.866025,-0.5,0;3.14159rad)
  shape: bbox 54.96 x 35.2 x 11.17 mm, 6 faces (baked)
FEATURE [Part::Feature] Cut456002
  Placement = pos=(-125,-8.66025,-130) rot=(0.866025,0.5,0;3.14159rad)
  shape: bbox 54.96 x 35.2 x 11.17 mm, 6 faces (baked)
FEATURE [Part::Cylinder] Cylinder054099009034  label="M2.5-tap-005"
  Angle = 360
  AttacherType = Attacher::AttachEngine3D
  Height = 100
  Placement = pos=(-40,-26,-2.5) rot=(0,1,0;1.5708rad)
  Radius = 1
FEATURE [Part::Cylinder] Cylinder054099009035  label="M2.5-tap-006"
  Angle = 360
  AttacherType = Attacher::AttachEngine3D
  Height = 100
  Placement = pos=(-40,-14,-2.5) rot=(0,1,0;1.5708rad)
  Radius = 1
FEATURE [Part::Mirroring] Part__Mirroring005036  label="M2.5-tap-1 (Mirror #12)001"
  Base = (0,0,0)
  Normal = (0,1,0)
  Placement = pos=(-59,0,-125) rot=(0,0,1;0rad)
  Source = -> Cylinder054099009034
FEATURE [Part::Mirroring] Part__Mirroring005037  label="M2.5-tap-2 (Mirror #13)001"
  Base = (0,0,0)
  Normal = (0,1,0)
  Placement = pos=(-59,0,-125) rot=(0,0,1;0rad)
  Source = -> Cylinder054099009035
FEATURE [Part::Cylinder] Cylinder054099009036  label="M2.5-tap-007"
  Angle = 360
  AttacherType = Attacher::AttachEngine3D
  Height = 100
  Placement = pos=(-99,-26,-127.5) rot=(0,1,0;1.5708rad)
  Radius = 1
FEATURE [Part::Cylinder] Cylinder054099009037  label="M2.5-tap-008"
  Angle = 360
  AttacherType = Attacher::AttachEngine3D
  Height = 100
  Placement = pos=(-99,-14,-127.5) rot=(0,1,0;1.5708rad)
  Radius = 1
FEATURE [Part::Fuse] Fusion051010010012015014085  label="balls-1"
  Base = -> Part__Mirroring005032
  Tool = -> Sphere006006006006015
FEATURE [Part::Fuse] Fusion051010010012015014086
  Base = -> Part__Mirroring005036
  Tool = -> Cylinder054099009037
FEATURE [Part::Fuse] Fusion051010010012015014087
  Base = -> Cylinder054099009036
  Tool = -> Fusion051010010012015014086
FEATURE [Part::Fuse] Fusion051010010012015014088  label="M2.5-taps"
  Base = -> Part__Mirroring005037
  Tool = -> Fusion051010010012015014087
FEATURE [Part::Feature] Fusion051010010012015014088001
  Placement = pos=(-180,103.923,0) rot=(0,0,1;2.0944rad)
  shape: bbox 96.77 x 113.6 x 2 mm, 12 faces, 4 solids (baked)
FEATURE [Part::Feature] Fusion051010010012015014088002
  Placement = pos=(-180,-103.923,0) rot=(0,0,1;4.18879rad)
  shape: bbox 96.77 x 113.6 x 2 mm, 12 faces, 4 solids (baked)
FEATURE [Part::Feature] Fusion051010010012015014085001  label="Fusion051010010012015014085001-xxx"
  Placement = pos=(820,103.923,0) rot=(0,0,1;2.0944rad)
  shape: bbox 40.74 x 26.1 x 6.1 mm, 2 faces, 2 solids (baked)
FEATURE [Part::Feature] Fusion051010010012015014085002  label="Fusion051010010012015014085002-xxx"
  Placement = pos=(820,-103.923,0) rot=(0,0,-1;2.0944rad)
  shape: bbox 40.74 x 26.1 x 6.1 mm, 2 faces, 2 solids (baked)
FEATURE [Part::Box] Box112015002017004007004038085  label="Cube172"
  AttacherType = Attacher::AttachEngine3D
  Height = 10
  Length = 100
  Placement = pos=(-175,-50,-120) rot=(0,0,1;0rad)
  Width = 100
FEATURE [Part::Fuse] Fusion051010010012015014088003
  Base = -> Cut456
  Tool = -> Cut456001
FEATURE [Part::Fuse] Fusion051010010012015014088004
  Base = -> Cut456002
  Tool = -> Fusion051010010012015014088003
FEATURE [Part::Cut] Cut456003
  Base = -> Fusion051010010012015014088004
  Tool = -> Box112015002017004007004038085
FEATURE [Part::Fuse] Fusion051010010012015014088005
  Base = -> Fusion051010010012015014088001
  Tool = -> Fusion051010010012015014088002
FEATURE [Part::Fuse] Fusion051010010012015014088006  label="M2.5-taps-1"
  Base = -> Fusion051010010012015014088
  Tool = -> Fusion051010010012015014088005
FEATURE [Part::Box] Box112015002017004007004038086  label="Cube173"
  AttacherType = Attacher::AttachEngine3D
  Height = 20
  Length = 20
  Placement = pos=(-98.7,-50,-131) rot=(0,0,1;0rad)
  Width = 100
FEATURE [Part::Feature] Box112015002017004007004038086001
  Placement = pos=(-87.3487,43.4463,-131) rot=(0,0,1;2.0944rad)
  shape: bbox 96.6 x 67.32 x 20 mm, 6 faces (baked)
FEATURE [Part::Feature] Box112015002017004007004038086002
  Placement = pos=(-173.951,6.55366,-131) rot=(0,0,1;4.18879rad)
  shape: bbox 96.6 x 67.32 x 20 mm, 6 faces (baked)
FEATURE [Part::Fuse] Fusion051010010012015014088007
  Base = -> Box112015002017004007004038086
  Tool = -> Box112015002017004007004038086001
FEATURE [Part::Fuse] Fusion051010010012015014088008
  Base = -> Box112015002017004007004038086002
  Tool = -> Fusion051010010012015014088007
FEATURE [Part::Cut] Cut456004
  Base = -> Part__Feature161
  Tool = -> Fusion051010010012015014088008
FEATURE [Part::Fuse] Fusion051010010012015014088009
  Base = -> Cut456003
  Tool = -> Cut456004
FEATURE [Part::Cut] Cut456005
  Base = -> Fusion051010010012015014088009
  Tool = -> Fusion051010010012015014088006
FEATURE [Part::Cut] Cut456006
  Base = -> Cut456005
  Tool = -> Fusion051010010012015014085002
FEATURE [Part::Cut] Cut456007
  Base = -> Cut456006
  Tool = -> Fusion051010010012015014085001
FEATURE [Part::Cut] Cut456008
  Base = -> Cut456007
  Tool = -> Fusion051010010012015014085
FEATURE [Part::Feature] Box112015002017004007004038086003002
  Placement = pos=(-173.951,6.55366,-117) rot=(0,0,1;4.18879rad)
  shape: bbox 96.6 x 67.32 x 20 mm, 6 faces (baked)
FEATURE [Part::Cut] Cut456009  label="hot-end-shell-a"
  Base = -> Cut456008
  Placement = pos=(120,0,0) rot=(0,0,1;0rad)
  Tool = -> Box112015002017004007004038086003002
FEATURE [Part::Cylinder] Cylinder054099009038  label="bed-121"
  Angle = 360
  AttacherType = Attacher::AttachEngine3D
  Height = 6
  Placement = pos=(-120,0,-259) rot=(0,0,1;0rad)
  Radius = 110
FEATURE [Part::Cylinder] Cylinder054099009039  label="bed-122"
  Angle = 360
  AttacherType = Attacher::AttachEngine3D
  Height = 27
  Placement = pos=(-120,0,-264) rot=(0,0,1;0rad)
  Radius = 60
FEATURE [Part::Cut] Cut456010
  Base = -> Cylinder054099009038
  Tool = -> Cylinder054099009039
FEATURE [Part::Cylinder] Cylinder054099009040  label="Cylinder054099009148"
  Angle = 360
  AttacherType = Attacher::AttachEngine3D
  Height = 30
  Placement = pos=(-25,0,-275) rot=(0,0,1;0rad)
  Radius = 1.7
FEATURE [Part::Sphere] Sphere006006006006018  label="651 M4 x 10mm button Head Screw"
  Angle1 = -90
  Angle2 = 90
  Angle3 = 360
  AttacherType = Attacher::AttachEngine3D
  Placement = pos=(-25,0,-253) rot=(0,0,1;0rad)
  Radius = 5
FEATURE [Part::Cylinder] Cylinder054099009042  label="Cylinder054099009149"
  Angle = 360
  AttacherType = Attacher::AttachEngine3D
  Height = 30
  Placement = pos=(-63.2084,-37.1204,-275) rot=(0,0,-1;0.507716rad)
  Radius = 1.7
FEATURE [Part::Box] Box112015002017004007004038086003003  label="Cube174"
  AttacherType = Attacher::AttachEngine3D
  Height = 20
  Length = 43
  Placement = pos=(-74.5743,36.7089,-266) rot=(0,0,1;0.610865rad)
  Width = 100
FEATURE [Part::Box] Box112015002017004007004038086003004  label="Cube175"
  AttacherType = Attacher::AttachEngine3D
  Height = 20
  Length = 43
  Placement = pos=(-67.5743,36.7089,-266) rot=(0,0,1;0.610865rad)
  Width = 100
FEATURE [Part::Mirroring] Part__Mirroring005038  label="Cube175 (Mirror #34)"
  Base = (0,0,0)
  Normal = (0,1,0)
  Placement = pos=(-7,0,0) rot=(0,0,1;0rad)
  Source = -> Box112015002017004007004038086003004
FEATURE [Part::Cut] Cut456011
  Base = -> Cut456010
  Tool = -> Box112015002017004007004038086003003
FEATURE [Part::Cut] Cut456012
  Base = -> Cut456011
  Tool = -> Part__Mirroring005038
FEATURE [Part::Box] Box112015002017004007004038086003005  label="Cube176"
  AttacherType = Attacher::AttachEngine3D
  Height = 30
  Length = 207
  Placement = pos=(-286,-111,-266) rot=(0,0,1;0rad)
  Width = 212
FEATURE [Part::Cut] Cut456013
  Base = -> Cut456012
  Tool = -> Box112015002017004007004038086003005
FEATURE [Part::Box] Box112015002017004007004038086003006  label="Cube177"
  AttacherType = Attacher::AttachEngine3D
  Height = 10
  Length = 50
  Placement = pos=(-61,-10,-261) rot=(0,0,1;0rad)
  Width = 20
FEATURE [Part::Box] Box112015002017004007004038086003007  label="Cube178"
  AttacherType = Attacher::AttachEngine3D
  Height = 20
  Length = 26
  Placement = pos=(-56.7263,-2.53841,-264) rot=(0,0,1;0.331613rad)
  Width = 56
FEATURE [Part::Box] Box112015002017004007004038086003008  label="Cube179"
  AttacherType = Attacher::AttachEngine3D
  Height = 20
  Length = 26
  Placement = pos=(-56.7263,-2.53841,-264) rot=(0,0,1;0.331613rad)
  Width = 56
FEATURE [Part::Mirroring] Part__Mirroring005039  label="Cube179 (Mirror #35)"
  Base = (0,0,0)
  Normal = (0,1,0)
  Source = -> Box112015002017004007004038086003008
FEATURE [Part::Fuse] Fusion051010010012015014088010
  Base = -> Box112015002017004007004038086003006
  Tool = -> Box112015002017004007004038086003007
FEATURE [Part::Fuse] Fusion051010010012015014088011
  Base = -> Part__Mirroring005039
  Tool = -> Fusion051010010012015014088010
FEATURE [Part::MultiCommon] Common017
  Shapes = -> [Cut456013,Fusion051010010012015014088011]
FEATURE [Part::Cylinder] Cylinder054099009043  label="Cylinder054099009150"
  Angle = 360
  AttacherType = Attacher::AttachEngine3D
  Height = 170
  Radius = 10
FEATURE [Part::Box] Box112015002017004007004038086003009  label="Cube180"
  AttacherType = Attacher::AttachEngine3D
  Height = 200
  Length = 10
  Placement = pos=(5,-12,-1) rot=(0,0,1;0rad)
  Width = 24
FEATURE [Part::Feature] Box112015002017004007004038086003009001
  Placement = pos=(7.8923,10.3301,-1) rot=(0,0,1;2.0944rad)
  shape: bbox 25.78 x 20.66 x 200 mm, 6 faces (baked)
FEATURE [Part::Feature] Box112015002017004007004038086003009002
  Placement = pos=(-12.8923,1.66987,-1) rot=(0,0,1;4.18879rad)
  shape: bbox 25.78 x 20.66 x 200 mm, 6 faces (baked)
FEATURE [Part::Box] Box112015002017004007004038086003009003  label="Cube181"
  AttacherType = Attacher::AttachEngine3D
  Height = 200
  Length = 10
  Placement = pos=(-17,-12,-1) rot=(0,0,1;0rad)
  Width = 24
FEATURE [Part::Feature] Box112015002017004007004038086003009003001
  Placement = pos=(18.8923,-8.72243,-1) rot=(0,0,1;2.0944rad)
  shape: bbox 25.78 x 20.66 x 200 mm, 6 faces (baked)
FEATURE [Part::Feature] Box112015002017004007004038086003009003002
  Placement = pos=(-1.8923,20.7224,-1) rot=(0,0,1;4.18879rad)
  shape: bbox 25.78 x 20.66 x 200 mm, 6 faces (baked)
FEATURE [Part::Cut] Cut456017
  Base = -> Cylinder054099009043
  Tool = -> Box112015002017004007004038086003009
FEATURE [Part::Cut] Cut456018
  Base = -> Cut456017
  Tool = -> Box112015002017004007004038086003009003002
FEATURE [Part::Cut] Cut456019
  Base = -> Cut456018
  Tool = -> Box112015002017004007004038086003009003001
FEATURE [Part::Cut] Cut456020
  Base = -> Cut456019
  Tool = -> Box112015002017004007004038086003009003
FEATURE [Part::Cut] Cut456021
  Base = -> Cut456020
  Tool = -> Box112015002017004007004038086003009002
FEATURE [Part::Cut] Cut456022
  Base = -> Cut456021
  Tool = -> Box112015002017004007004038086003009001
FEATURE [Part::Cylinder] Cylinder054099009044  label="Cylinder054099009151"
  Angle = 360
  AttacherType = Attacher::AttachEngine3D
  Height = 10
  Placement = pos=(0,0,-1) rot=(0,0,1;0rad)
  Radius = 1.7
FEATURE [Part::Box] Box112015002017004007004038086003009003003  label="Cube182-xxx"
  AttacherType = Attacher::AttachEngine3D
  Height = 10
  Length = 10
  Placement = pos=(50,-1.7,-1) rot=(0,0,1;0rad)
  Width = 3.4
FEATURE [Part::Fuse] Fusion051010010012015014088012
  Base = -> Cylinder054099009044
  Tool = -> Box112015002017004007004038086003009003003
FEATURE [Part::Cylinder] Cylinder054099009045  label="Cylinder054099009152"
  Angle = 360
  AttacherType = Attacher::AttachEngine3D
  Height = 30
  Radius = 2.75
FEATURE [Part::Box] Box112015002017004007004038086003009003004  label="Cube183-xxx"
  AttacherType = Attacher::AttachEngine3D
  Height = 5
  Length = 10
  Placement = pos=(50,-2.75,0) rot=(0,0,1;0rad)
  Width = 5.5
FEATURE [Part::Fuse] Fusion051010010012015014088013
  Base = -> Cylinder054099009045
  Placement = pos=(0,0,10) rot=(0,0,1;0rad)
  Tool = -> Box112015002017004007004038086003009003004
FEATURE [Part::Cylinder] Cylinder054099009046  label="Cylinder054099009153"
  Angle = 360
  AttacherType = Attacher::AttachEngine3D
  Height = 1
  Radius = 3.5
FEATURE [Part::Box] Box112015002017004007004038086003009003005  label="Cube184"
  AttacherType = Attacher::AttachEngine3D
  Height = 1
  Length = 10
  Placement = pos=(0,-3.5,0) rot=(0,0,1;0rad)
  Width = 7
FEATURE [Part::Fuse] Fusion051010010012015014088014
  Base = -> Cylinder054099009046
  Placement = pos=(0,0,9) rot=(0,0,1;0rad)
  Tool = -> Box112015002017004007004038086003009003005
FEATURE [Part::Fuse] Fusion051010010012015014088015
  Base = -> Fusion051010010012015014088012
  Tool = -> Fusion051010010012015014088013
FEATURE [Part::Fuse] Fusion051010010012015014088017
  Base = -> Fusion051010010012015014088014
  Placement = pos=(0,0,30) rot=(0,0,1;0rad)
  Tool = -> Fusion051010010012015014088015
FEATURE [Part::Box] Box112015002017004007004038086003009003006  label="Cube185"
  AttacherType = Attacher::AttachEngine3D
  Height = 114
  Length = 19
  Placement = pos=(-10,0,-20) rot=(0,0,1;0rad)
  Width = 10
FEATURE [Part::Box] Box112015002017004007004038086003009003007  label="Cube186"
  AttacherType = Attacher::AttachEngine3D
  Height = 114
  Length = 19
  Placement = pos=(-10,-10,20) rot=(0,0,1;0rad)
  Width = 10
FEATURE [Part::Cut] Cut456023
  Base = -> Cut456022
  Placement = pos=(0,0,-85) rot=(0,0,1;0rad)
  Tool = -> Fusion051010010012015014088017
FEATURE [Part::Cut] Cut456024
  Base = -> Cut456023
  Tool = -> Box112015002017004007004038086003009003007
FEATURE [Part::Cut] Cut456025
  Base = -> Cut456024
  Tool = -> Box112015002017004007004038086003009003006
FEATURE [Part::Box] Box112015002017004007004038086003009003008  label="Cube187"
  AttacherType = Attacher::AttachEngine3D
  Height = 10
  Length = 3.2
  Placement = pos=(-1.6,-12,5) rot=(0,0,1;0rad)
  Width = 20
FEATURE [Part::Box] Box112015002017004007004038086003009003009  label="Cube188"
  AttacherType = Attacher::AttachEngine3D
  Height = 16
  Length = 9
  Placement = pos=(-4,-7,2) rot=(0,0,1;0rad)
  Width = 6
FEATURE [Part::Fillet] Fillet016
  Base = -> Box112015002017004007004038086003009003008
  Edges = 1 edges r=1.5: [Edge2]
FEATURE [Part::Fillet] Fillet017
  Base = -> Fillet016
  Edges = 1 edges r=1.5: [Edge15]
FEATURE [Part::Fillet] Fillet018
  Base = -> Fillet017
  Edges = 1 edges r=1.5: [Edge16]
FEATURE [Part::Fillet] Fillet019
  Base = -> Fillet018
  Edges = 1 edges r=1.5: [Edge16]
FEATURE [Part::Fillet] Fillet020
  Base = -> Box112015002017004007004038086003009003009
  Edges = 1 edges r=2: [Edge4]
FEATURE [Part::Fillet] Fillet021
  Base = -> Fillet020
  Edges = 1 edges r=2: [Edge3]
FEATURE [Part::Fuse] Fusion051010010012015014088018
  Base = -> Cut456025
  Tool = -> Fillet021
FEATURE [Part::Cut] Cut456026
  Base = -> Fusion051010010012015014088018
  Tool = -> Fillet019
FEATURE [Part::Cylinder] Cylinder054099009047  label="Cylinder054099009154"
  Angle = 360
  AttacherType = Attacher::AttachEngine3D
  Height = 15
  Placement = pos=(0,1,-10) rot=(1,0,0;1.5708rad)
  Radius = 1.2
FEATURE [Part::Cut] Cut456027
  Base = -> Cut456026
  Tool = -> Cylinder054099009047
FEATURE [Part::Cylinder] Cylinder054099009048  label="Cylinder054099009155"
  Angle = 360
  AttacherType = Attacher::AttachEngine3D
  Height = 38
  Placement = pos=(3,1.8,-19) rot=(0,0,1;0rad)
  Radius = 2
FEATURE [Part::Cylinder] Cylinder054099009049  label="Cylinder054099009156"
  Angle = 360
  AttacherType = Attacher::AttachEngine3D
  Height = 38
  Placement = pos=(-4,1.8,-19) rot=(0,0,1;0rad)
  Radius = 2
FEATURE [Part::Cut] Cut456028
  Base = -> Cut456027
  Tool = -> Cylinder054099009048
FEATURE [Part::Cut] Cut456029
  Base = -> Cut456028
  Tool = -> Cylinder054099009049
FEATURE [Part::Cone] Cone022  label="Cone014"
  Angle = 360
  AttacherType = Attacher::AttachEngine3D
  Height = 6
  Placement = pos=(-2,0,0) rot=(0,-1,0;1.5708rad)
  Radius1 = 0
  Radius2 = 2
FEATURE [Part::Cut] Cut456030
  Base = -> Cut456029
  Tool = -> Cone022
FEATURE [Part::Cylinder] Cylinder054099009050  label="Cylinder054099009157"
  Angle = 360
  AttacherType = Attacher::AttachEngine3D
  Height = 7
  Placement = pos=(-4,1.8,0) rot=(0,1,0;1.5708rad)
  Radius = 2
FEATURE [Part::Cut] Cut456031  label="half-angle-arm-a"
  Base = -> Cut456030
  Tool = -> Cylinder054099009050
FEATURE [Part::Cylinder] Cylinder054099009051  label="Cylinder054099009158"
  Angle = 360
  AttacherType = Attacher::AttachEngine3D
  Height = 20
  Placement = pos=(0,0,-1) rot=(0,0,1;0rad)
  Radius = 2.75
FEATURE [Part::Box] Box112015002017004007004038086003009003010  label="Cube189"
  AttacherType = Attacher::AttachEngine3D
  Height = 20
  Length = 10
  Placement = pos=(0,-2.75,-1) rot=(0,0,1;0rad)
  Width = 5.5
FEATURE [Part::Fuse] Fusion051010010012015014088019  label="Fusion051010010012015014088019-xxx"
  Base = -> Cylinder054099009051
  Placement = pos=(-50,0,-41) rot=(0,1,0;0.314159rad)
  Tool = -> Box112015002017004007004038086003009003010
FEATURE [Part::Cylinder] Cylinder054099009052  label="wire-clamp-screw-hole-003"
  Angle = 360
  AttacherType = Attacher::AttachEngine3D
  Height = 30
  Placement = pos=(-23.5,-5,-12) rot=(0,1,0;1.5708rad)
  Radius = 2.5
FEATURE [Part::Cylinder] Cylinder054099009053  label="wire-clamp-screw-hole-004"
  Angle = 360
  AttacherType = Attacher::AttachEngine3D
  Height = 30
  Placement = pos=(-23.5,-5,-4) rot=(0,1,0;1.5708rad)
  Radius = 2.5
FEATURE [Part::Cut] Cut456033
  Base = -> Cut373
  Tool = -> Cylinder054099009052
FEATURE [Part::Cut] Cut456034  label="6142 Slider Ball Block"
  Base = -> Cut456033
  Tool = -> Cylinder054099009053
FEATURE [Part::Cut] Cut456035
  Base = -> Box112015002017004007004038049
  Tool = -> Sphere006006006006012
FEATURE [Part::Cut] Cut456036
  Base = -> Cut456035
  Tool = -> Cylinder054072
FEATURE [Part::Cut] Cut456037  label="6143 ball clamp"
  Base = -> Cut456036
  Placement = pos=(-6,0,0) rot=(0,0,1;0rad)
  Tool = -> Cylinder054073
FEATURE [Part::Cylinder] Cylinder054099009054  label="Cylinder054099009159"
  Angle = 360
  AttacherType = Attacher::AttachEngine3D
  Height = 10
  Placement = pos=(25.8,-20,-125) rot=(0,0,1;0rad)
  Radius = 2.5
FEATURE [Part::Cylinder] Cylinder054099009055  label="Cylinder054099009160"
  Angle = 360
  AttacherType = Attacher::AttachEngine3D
  Height = 10
  Placement = pos=(25.8,20,-125) rot=(0,0,1;0rad)
  Radius = 2.5
FEATURE [Part::Fuse] Fusion051010010012015014088020  label="ball-notches"
  Base = -> Cylinder054099009054
  Tool = -> Cylinder054099009055
FEATURE [Part::Feature] Fusion051010010012015014088020001
  Placement = pos=(0,0,0) rot=(0,0,1;2.0944rad)
  shape: bbox 39.64 x 25 x 10 mm, 6 faces, 2 solids (baked)
FEATURE [Part::Feature] Fusion051010010012015014088020002
  Placement = pos=(0,0,0) rot=(0,0,1;4.18879rad)
  shape: bbox 39.64 x 25 x 10 mm, 6 faces, 2 solids (baked)
FEATURE [Part::Fuse] Fusion051010010012015014088020003
  Base = -> Fusion051010010012015014088020
  Tool = -> Fusion051010010012015014088020001
FEATURE [Part::Fuse] Fusion051010010012015014088020004
  Base = -> Fusion051010010012015014088020002
  Tool = -> Fusion051010010012015014088020003
FEATURE [Part::Cut] Cut456038  label="hot-end-shell-aa"
  Base = -> Cut456009
  Placement = pos=(-120,0,0) rot=(0,0,1;0rad)
  Tool = -> Fusion051010010012015014088020004
FEATURE [Part::Box] Box112015002017004007004038086003009003011  label="Cube190"
  AttacherType = Attacher::AttachEngine3D
  Height = 40
  Length = 30
  Placement = pos=(-23,-21,-96) rot=(0,0,1;0rad)
  Width = 30
FEATURE [Part::Fillet] Fillet022
  Base = -> Common017
  Edges = 1 edges r=15: [Edge23]
FEATURE [Part::Fillet] Fillet023
  Base = -> Fillet022
  Edges = 1 edges r=15: [Edge34]
FEATURE [Part::Fillet] Fillet024
  Base = -> Fillet023
  Edges = 1 edges r=6: [Edge16]
FEATURE [Part::Fillet] Fillet025
  Base = -> Fillet024
  Edges = 1 edges r=6: [Edge35]
FEATURE [Part::Fillet] Fillet026
  Base = -> Fillet025
  Edges = 1 edges r=30: [Edge18]
FEATURE [Part::Fillet] Fillet027
  Base = -> Fillet026
  Edges = 1 edges r=30: [Edge28]
FEATURE [Part::Fillet] Fillet028
  Base = -> Fillet027
  Edges = 1 edges r=12: [Edge42]
FEATURE [Part::Fillet] Fillet029
  Base = -> Fillet028
  Edges = 1 edges r=12: [Edge35]
FEATURE [Part::Cylinder] Cylinder054099009056  label="bed-123"
  Angle = 360
  AttacherType = Attacher::AttachEngine3D
  Height = 10
  Placement = pos=(-130,0,-261) rot=(0,0,1;0rad)
  Radius = 110
FEATURE [Part::MultiCommon] Common018
  Shapes = -> [Fillet029,Cylinder054099009056]
FEATURE [Part::Fillet] Fillet030
  Base = -> Common018
  Edges = 1 edges r=6: [Edge24]
FEATURE [Part::Fillet] Fillet031
  Base = -> Fillet030
  Edges = 1 edges r=6: [Edge27]
FEATURE [Part::Cylinder] Cylinder054099009057  label="Cylinder054099009161"
  Angle = 360
  AttacherType = Attacher::AttachEngine3D
  Height = 30
  Placement = pos=(-46,29,-275) rot=(0,0,1;0.507891rad)
  Radius = 1.7
FEATURE [Part::Cylinder] Cylinder054099009058  label="Cylinder054099009162"
  Angle = 360
  AttacherType = Attacher::AttachEngine3D
  Height = 30
  Placement = pos=(-43,19,-275) rot=(0,0,1;0.507891rad)
  Radius = 1.7
FEATURE [Part::Cylinder] Cylinder054099009059  label="Cylinder054099009163"
  Angle = 360
  AttacherType = Attacher::AttachEngine3D
  Height = 30
  Placement = pos=(-37,0,-275) rot=(0,0,1;0rad)
  Radius = 1.7
FEATURE [Part::MultiFuse] Fusion051010010012015014088020005
  Shapes = -> [Cylinder054099009057,Cylinder054099009058]
FEATURE [Part::MultiFuse] Fusion051010010012015014088020006
  Shapes = -> [Cylinder054099009057,Cylinder054099009058]
FEATURE [Part::Mirroring] Part__Mirroring005040  label="Fusion051010010012015014088020006 (Mirror #30)"
  Base = (0,0,0)
  Normal = (0,1,0)
  Source = -> Fusion051010010012015014088020006
FEATURE [Part::MultiFuse] Fusion051010010012015014088020007
  Shapes = -> [Part__Mirroring005040,Fusion051010010012015014088020005]
FEATURE [Part::MultiFuse] Fusion051010010012015014088020008
  Shapes = -> [Cylinder054099009059,Fusion051010010012015014088020007]
FEATURE [Part::Box] Box112015002017004007004038086003009003012  label="Cube191"
  AttacherType = Attacher::AttachEngine3D
  Height = 15
  Length = 10
  Placement = pos=(-63.2084,-38.8204,-264) rot=(0,0,1;0rad)
  Width = 3.4
FEATURE [Part::Cylinder] Cylinder054099009060  label="Cylinder054099009164"
  Angle = 360
  AttacherType = Attacher::AttachEngine3D
  Height = 30
  Placement = pos=(-53.2084,-37.1204,-275) rot=(0,0,-1;0.507716rad)
  Radius = 1.7
FEATURE [Part::MultiFuse] Fusion051010010012015014088020009
  Shapes = -> [Cylinder054099009042,Box112015002017004007004038086003009003012]
FEATURE [Part::MultiFuse] Fusion051010010012015014088020010
  Shapes = -> [Fusion051010010012015014088020009,Cylinder054099009060]
FEATURE [Part::MultiFuse] Fusion051010010012015014088020011
  Shapes = -> [Fusion051010010012015014088020009,Cylinder054099009060]
FEATURE [Part::Mirroring] Part__Mirroring005041  label="Fusion051010010012015014088020011 (Mirror #31)"
  Base = (0,0,0)
  Normal = (0,1,0)
  Source = -> Fusion051010010012015014088020011
FEATURE [Part::MultiFuse] Fusion051010010012015014088020012
  Shapes = -> [Fusion051010010012015014088020010,Part__Mirroring005041]
FEATURE [Part::MultiFuse] Fusion051010010012015014088020013
  Shapes = -> [Fusion051010010012015014088020012,Cylinder054099009040]
FEATURE [Part::MultiFuse] Fusion051010010012015014088020014
  Shapes = -> [Fusion051010010012015014088020013,Fusion051010010012015014088020008]
FEATURE [Part::Cut] Cut456040  label="6160 lasercut-mdf-support"
  Base = -> Fillet031
  Placement = pos=(0,0,1) rot=(0,0,1;0rad)
  Tool = -> Fusion051010010012015014088020014
FEATURE [Part::Feature] Cut456040_cs  label="lasercut-mdf-support-profile"
  Placement = pos=(0,0,1) rot=(0,0,1;0rad)
  shape: bbox 49.94 x 91.93 x 1e-05 mm, 0 faces, 0 solids (baked)
FEATURE [Part::Cut] Cut456041
  Base = -> Cut456031
  Tool = -> Box112015002017004007004038086003009003011
FEATURE [Part::Cut] Cut456042
  Base = -> Cut456041
  Tool = -> Fusion051010010012015014088019
FEATURE [Part::Cylinder] Cylinder054099009061  label="Cylinder054099009165"
  Angle = 360
  AttacherType = Attacher::AttachEngine3D
  Height = 10
  Placement = pos=(0,0,-56) rot=(0,0,1;0rad)
  Radius = 1.7
FEATURE [Part::Box] Box112015002017004007004038086003009003013  label="Cube192-xxx"
  AttacherType = Attacher::AttachEngine3D
  Height = 10
  Length = 10
  Placement = pos=(50,-1.7,-56) rot=(0,0,1;0rad)
  Width = 3.4
FEATURE [Part::Fuse] Fusion051010010012015014088020015
  Base = -> Cylinder054099009061
  Placement = pos=(0,0,-5) rot=(0,0,1;0rad)
  Tool = -> Box112015002017004007004038086003009003013
FEATURE [Part::Cone] Cone023  label="Cone015"
  Angle = 360
  AttacherType = Attacher::AttachEngine3D
  Height = 2.5
  Placement = pos=(0,0,-58.5) rot=(0,0,1;0rad)
  Radius1 = 3.5
  Radius2 = 5
FEATURE [Part::Cut] Cut456043
  Base = -> Cone023
  Tool = -> Fusion051010010012015014088020015
FEATURE [Part::MultiFuse] Fusion051010010012015014088020016
  Shapes = -> [Cut456042,Cut456043]
FEATURE [Part::Feature] Part__Feature127  label="1247.1 Nozzle Duct"
  Placement = pos=(-120,1e-12,-161.305) rot=(0.965926,0.258819,0;3.14159rad)
  shape: bbox 46.33 x 39.88 x 11.66 mm, 173 faces (baked)
FEATURE [Part::Feature] Part__Feature121  label="1223 Effector Plate (MDF)"
  Placement = pos=(-120,0,-146.695) rot=(0.965926,0.258819,0;3.14159rad)
  shape: bbox 57.24 x 64.19 x 3 mm, 97 faces (baked)
FEATURE [Part::Feature] Part__Feature121_cs  label="lasercut-mdf-hot-end-holder-profile"
  shape: bbox 57.24 x 64.19 x 2e-07 mm, 0 faces, 0 solids (baked)
FEATURE [Part::Box] Box112015002017004007004038086003009003014  label="Cube193"
  AttacherType = Attacher::AttachEngine3D
  Height = 12
  Length = 10
  Placement = pos=(-23,-30,-12) rot=(0,0,1;0rad)
  Width = 58
FEATURE [Part::Chamfer] Chamfer006012052
  Base = -> Box112015002017004007004038086003009003014
  Edges = 1 edges r=7: [Edge4]
  Placement = pos=(0,102,0) rot=(0,1,0;1.5708rad)
FEATURE [Part::Sphere] Sphere006006006006019  label="ball-r-3"
  Angle1 = -90
  Angle2 = 90
  Angle3 = 360
  AttacherType = Attacher::AttachEngine3D
  Placement = pos=(-5,77,21) rot=(0,1,0;1.5708rad)
  Radius = 3
FEATURE [Part::Sphere] Sphere006006006006020  label="ball-r-305-z"
  Angle1 = -90
  Angle2 = 90
  Angle3 = 360
  AttacherType = Attacher::AttachEngine3D
  Placement = pos=(-5,85,21) rot=(0,1,0;1.5708rad)
  Radius = 3.05
FEATURE [Part::Sphere] Sphere006006006006021  label="ball-r-31"
  Angle1 = -90
  Angle2 = 90
  Angle3 = 360
  AttacherType = Attacher::AttachEngine3D
  Placement = pos=(-5,93,21) rot=(0,1,0;1.5708rad)
  Radius = 3.1
FEATURE [Part::Sphere] Sphere006006006006022  label="ball-r-315"
  Angle1 = -90
  Angle2 = 90
  Angle3 = 360
  AttacherType = Attacher::AttachEngine3D
  Placement = pos=(-5,101,21) rot=(0,1,0;1.5708rad)
  Radius = 3.15
FEATURE [Part::Sphere] Sphere006006006006023  label="ball-r-32"
  Angle1 = -90
  Angle2 = 90
  Angle3 = 360
  AttacherType = Attacher::AttachEngine3D
  Placement = pos=(-5,109,21) rot=(0,1,0;1.5708rad)
  Radius = 3.2
FEATURE [Part::Cut] Cut456044
  Base = -> Chamfer006012052
  Tool = -> Sphere006006006006019
FEATURE [Part::Cut] Cut456045
  Base = -> Cut456044
  Tool = -> Sphere006006006006020
FEATURE [Part::Cut] Cut456046
  Base = -> Cut456045
  Tool = -> Sphere006006006006021
FEATURE [Part::Cut] Cut456047
  Base = -> Cut456046
  Tool = -> Sphere006006006006022
FEATURE [Part::Cut] Cut456048  label="ball-radius-test-piece-a"
  Base = -> Cut456047
  Tool = -> Sphere006006006006023
FEATURE [Part::Sphere] Sphere006006006006024  label="ball-r-325"
  Angle1 = -90
  Angle2 = 90
  Angle3 = 360
  AttacherType = Attacher::AttachEngine3D
  Placement = pos=(-5,117,21) rot=(0,1,0;1.5708rad)
  Radius = 3.25
FEATURE [Part::Sphere] Sphere006006006006025  label="ball-r-33"
  Angle1 = -90
  Angle2 = 90
  Angle3 = 360
  AttacherType = Attacher::AttachEngine3D
  Placement = pos=(-5,125,21) rot=(0,1,0;1.5708rad)
  Radius = 3.3
FEATURE [Part::Cut] Cut456049
  Base = -> Cut456048
  Tool = -> Sphere006006006006024
FEATURE [Part::Cut] Cut456050  label="ball-radius-test-piece"
  Base = -> Cut456049
  Tool = -> Sphere006006006006025
FEATURE [Part::Box] Box112015002017004007004038086003009003015  label="duet-a"
  AttacherType = Attacher::AttachEngine3D
  Height = 18
  Length = 100
  Width = 123
FEATURE [Part::Cylinder] Cylinder054099009062  label="Cylinder054099009166"
  Angle = 360
  AttacherType = Attacher::AttachEngine3D
  Height = 30
  Placement = pos=(4,4,0) rot=(0,0,1;0rad)
  Radius = 1.7
FEATURE [Part::Cylinder] Cylinder054099009063  label="Cylinder054099009167"
  Angle = 360
  AttacherType = Attacher::AttachEngine3D
  Height = 30
  Placement = pos=(4,119,0) rot=(0,0,1;0rad)
  Radius = 1.7
FEATURE [Part::Cylinder] Cylinder054099009064  label="Cylinder054099009168"
  Angle = 360
  AttacherType = Attacher::AttachEngine3D
  Height = 30
  Placement = pos=(96,4,0) rot=(0,0,1;0rad)
  Radius = 1.7
FEATURE [Part::Cylinder] Cylinder054099009065  label="Cylinder054099009169"
  Angle = 360
  AttacherType = Attacher::AttachEngine3D
  Height = 30
  Placement = pos=(96,119,0) rot=(0,0,1;0rad)
  Radius = 1.7
FEATURE [Part::MultiFuse] Fusion051010010012015014088020017  label="duet-and-screws-a"
  Shapes = -> [Cylinder054099009065,Cylinder054099009063,Cylinder054099009062,Cylinder054099009064,Box112015002017004007004038086003009003015]
FEATURE [Part::Box] Box112015002017004007004038086003009003016  label="Cube194"
  AttacherType = Attacher::AttachEngine3D
  Height = 10
  Length = 110
  Placement = pos=(-5,64.5,9) rot=(0,0,1;0rad)
  Width = 1
FEATURE [Part::Box] Box112015002017004007004038086003009003017  label="Cube195"
  AttacherType = Attacher::AttachEngine3D
  Height = 10
  Length = 1
  Placement = pos=(49.5,-5,9) rot=(0,0,1;0rad)
  Width = 133
FEATURE [Part::MultiFuse] Fusion051010010012015014088020018
  Shapes = -> [Box112015002017004007004038086003009003016,Box112015002017004007004038086003009003017]
FEATURE [Part::Cut] Cut456051  label="394 Duet"
  Base = -> Fusion051010010012015014088020017
  Placement = pos=(-70.2987,-90.239,-326) rot=(0,0,1;0.523599rad)
  Tool = -> Fusion051010010012015014088020018
FEATURE [Part::Box] Box112015002017004007004038086003009003018  label="Cube196"
  AttacherType = Attacher::AttachEngine3D
  Height = 5
  Length = 39
  Placement = pos=(-65,-43,-307) rot=(0,0,1;0rad)
  Width = 25
FEATURE [Part::Cylinder] Cylinder054099009066  label="pcb-post"
  Angle = 360
  AttacherType = Attacher::AttachEngine3D
  Height = 17
  Placement = pos=(-60,-39,-322) rot=(0,0,1;0rad)
  Radius = 4
FEATURE [Part::Cylinder] Cylinder054099009067  label="pcb-m4-hole"
  Angle = 360
  AttacherType = Attacher::AttachEngine3D
  Height = 17
  Placement = pos=(-60,-39,-323) rot=(0,0,1;0rad)
  Radius = 1.8
FEATURE [Part::Cylinder] Cylinder054099009068  label="Cylinder054099009170"
  Angle = 360
  AttacherType = Attacher::AttachEngine3D
  Height = 17
  Placement = pos=(-60,-22,-315) rot=(0,0,1;0rad)
  Radius = 1.7
FEATURE [Part::Cylinder] Cylinder054099009069  label="Cylinder054099009171"
  Angle = 360
  AttacherType = Attacher::AttachEngine3D
  Height = 17
  Placement = pos=(-31,-22,-315) rot=(0,0,1;0rad)
  Radius = 1.7
FEATURE [Part::Box] Box112015002017004007004038086003009003019  label="Cube197"
  AttacherType = Attacher::AttachEngine3D
  Height = 18
  Length = 22
  Placement = pos=(-58,-41.5,-322) rot=(0,0,1;0rad)
  Width = 5
FEATURE [Part::Box] Box112015002017004007004038086003009003020  label="Cube198"
  AttacherType = Attacher::AttachEngine3D
  Height = 13
  Length = 15
  Placement = pos=(-58,-41.5,-316) rot=(0,0,1;0rad)
  Width = 11
FEATURE [Part::Cone] Cone026  label="Cone018"
  Angle = 360
  AttacherType = Attacher::AttachEngine3D
  Height = 10
  Placement = pos=(-49,-37,-311) rot=(1,0,0;1.5708rad)
  Radius1 = 1.1
  Radius2 = 3
FEATURE [Part::Cylinder] Cylinder054099009070  label="Cylinder054099009172"
  Angle = 360
  AttacherType = Attacher::AttachEngine3D
  Height = 10
  Placement = pos=(-49,-25,-311) rot=(1,0,0;1.5708rad)
  Radius = 2.1
FEATURE [Part::Cylinder] Cylinder054099009071  label="Cylinder054099009173"
  Angle = 360
  AttacherType = Attacher::AttachEngine3D
  Height = 10
  Placement = pos=(-49,-29,-311) rot=(1,0,0;1.5708rad)
  Radius = 1.1
FEATURE [Part::MultiFuse] Fusion051010010012015014088020020
  Shapes = -> [Cone026,Cylinder054099009070,Cylinder054099009071]
FEATURE [Part::Fillet] Fillet035
  Base = -> Fusion051010010012015014088020020
  Edges = 1 edges r=20: [Edge3]
FEATURE [Part::Cut] Cut456057  label="filament-guide-in"
  Base = -> Box112015002017004007004038086003009003020
  Tool = -> Fillet035
FEATURE [Part::Cylinder] Cylinder054099009072  label="Cylinder054099009174"
  Angle = 360
  AttacherType = Attacher::AttachEngine3D
  Height = 10
  Placement = pos=(-47,-29.5,-314) rot=(1,0,0;1.5708rad)
  Radius = 6
FEATURE [Part::Cylinder] Cylinder054099009073  label="Cylinder054099009175"
  Angle = 360
  AttacherType = Attacher::AttachEngine3D
  Height = 10
  Placement = pos=(-47,-33,-314) rot=(1,0,0;1.5708rad)
  Radius = 4.2
FEATURE [Part::MultiFuse] Fusion051010010012015014088020022
  Shapes = -> [Cylinder054099009073,Cylinder054099009072]
FEATURE [Part::Cut] Cut456058  label="power-input"
  Base = -> Box112015002017004007004038086003009003019
  Tool = -> Fusion051010010012015014088020022
FEATURE [Part::Cylinder] Cylinder054099009074  label="Cylinder054099009176"
  Angle = 360
  AttacherType = Attacher::AttachEngine3D
  Height = 17
  Placement = pos=(-35,-22,-315) rot=(0,0,1;0rad)
  Radius = 1.7
FEATURE [Part::Cylinder] Cylinder054099009075  label="Cylinder054099009177"
  Angle = 360
  AttacherType = Attacher::AttachEngine3D
  Height = 17
  Placement = pos=(-56,-22,-315) rot=(0,0,1;0rad)
  Radius = 1.7
FEATURE [Part::Box] Box112015002017004007004038086003009003021  label="Cube199"
  AttacherType = Attacher::AttachEngine3D
  Height = 10
  Length = 4
  Placement = pos=(-60,-23.7,-310) rot=(0,0,1;0rad)
  Width = 3.4
FEATURE [Part::Box] Box112015002017004007004038086003009003022  label="Cube200"
  AttacherType = Attacher::AttachEngine3D
  Height = 10
  Length = 4
  Placement = pos=(-35,-23.7,-310) rot=(0,0,1;0rad)
  Width = 3.4
FEATURE [Part::MultiFuse] Fusion051010010012015014088020023  label="pcb-brac-screw-slot-a"
  Shapes = -> [Box112015002017004007004038086003009003022,Cylinder054099009074,Cylinder054099009069]
FEATURE [Part::MultiFuse] Fusion051010010012015014088020024  label="pcb-brac-screw-slot-b"
  Shapes = -> [Box112015002017004007004038086003009003021,Cylinder054099009075,Cylinder054099009068]
FEATURE [Part::Cut] Cut456059
  Base = -> Box112015002017004007004038086003009003018
  Tool = -> Fusion051010010012015014088020023
FEATURE [Part::Cut] Cut456060
  Base = -> Cut456059
  Tool = -> Fusion051010010012015014088020024
FEATURE [Part::Chamfer] Chamfer006012053
  Base = -> Cut456060
  Edges = 5 edges r=2: [Edge28,Edge29,Edge30,Edge31,Edge32]
FEATURE [Part::Chamfer] Chamfer006012054
  Base = -> Chamfer006012053
  Edges = 5 edges r=2: [Edge10,Edge11,Edge12,Edge13,Edge14]
FEATURE [Part::MultiFuse] Fusion051010010012015014088020025
  Shapes = -> [Chamfer006012054,Cylinder054099009066]
FEATURE [Part::Cut] Cut456061
  Base = -> Fusion051010010012015014088020025
  Tool = -> Cylinder054099009067
FEATURE [Part::Fillet] Fillet036  label="pcb-bracket-blank"
  Base = -> Cut456061
  Edges = 3 edges r=2: [Edge23,Edge25,Edge28]
FEATURE [Part::Fillet] Fillet037  label="pcb-bracket-blank001"
  Base = -> Cut456061
  Edges = 3 edges r=2: [Edge23,Edge25,Edge28]
FEATURE [Part::MultiFuse] Fusion051010010012015014088020026
  Shapes = -> [Cut456058,Fillet037]
FEATURE [Part::MultiFuse] Fusion051010010012015014088020027
  Shapes = -> [Fillet036,Cut456057]
FEATURE [Part::Mirroring] Part__Mirroring005042  label="Fusion051010010012015014088020027 (Mirror #32)"
  Base = (-106,0,0)
  Normal = (1,0,0)
  Source = -> Fusion051010010012015014088020027
FEATURE [Part::Chamfer] Chamfer006012055
  Base = -> Part__Mirroring005042
  Edges = 1 edges r=15: [Edge46]
FEATURE [Part::Chamfer] Chamfer006012056
  Base = -> Fusion051010010012015014088020026
  Edges = 1 edges r=6: [Edge49]
FEATURE [Part::Fillet] Fillet038
  Base = -> Chamfer006012055
  Edges = 2 edges r=4: [Edge27,Edge29]
FEATURE [Part::Fillet] Fillet039
  Base = -> Chamfer006012056
  Edges = 2 edges r=4: [Edge26,Edge28]
FEATURE [Part::Chamfer] Chamfer006012057
  Base = -> Fillet039
  Edges = 1 edges r=8: [Edge75]
FEATURE [Part::Fillet] Fillet040
  Base = -> Chamfer006012057
  Edges = 2 edges r=10: [Edge3,Edge16]
FEATURE [Part::Fillet] Fillet041
  Base = -> Fillet038
  Edges = 2 edges r=5: [Edge69,Edge74]
FEATURE [Part::Fillet] Fillet042
  Base = -> Fillet041
  Edges = 2 edges r=2: [Edge41,Edge45]
FEATURE [Part::Chamfer] Chamfer006012058  label="6155 pcb bracket filament guide"
  Base = -> Fillet042
  Edges = 1 edges r=0.7: [Edge100]
FEATURE [Part::Chamfer] Chamfer006012059  label="6156 pcb bracket power input"
  Base = -> Fillet040
  Edges = 1 edges r=0.7: [Edge55]
FEATURE [Part::Cut] Cut456062  label="base-arm001"
  Base = -> Cut449
  Placement = pos=(0,0,0) rot=(0,0,1;0.523599rad)
  Tool = -> Fusion051010010012015014081
FEATURE [Part::Mirroring] Part__Mirroring005043  label="6130 base arm L"
  Base = (0,0,0)
  Normal = (0,1,0)
  Placement = pos=(-184.5,106.521,0) rot=(0,0,1;2.0944rad)
  Source = -> Cut456062
FEATURE [Part::Box] Box112015002017004007004038086003009003023  label="Cube201"
  AttacherType = Attacher::AttachEngine3D
  Height = 5
  Length = 52
  Placement = pos=(-75,-27,-307) rot=(0,0,1;0rad)
  Width = 46
FEATURE [Part::Cylinder] Cylinder054099009076  label="pcb-post001"
  Angle = 360
  AttacherType = Attacher::AttachEngine3D
  Height = 17
  Placement = pos=(-60,-63,-322) rot=(0,0,1;0rad)
  Radius = 4
FEATURE [Part::Cylinder] Cylinder054099009077  label="pcb-m4-hole001"
  Angle = 360
  AttacherType = Attacher::AttachEngine3D
  Height = 17
  Placement = pos=(-10,76,-323) rot=(0,0,1;0rad)
  Radius = 1.8
FEATURE [Part::Cylinder] Cylinder054099009078  label="Cylinder054099009178"
  Angle = 360
  AttacherType = Attacher::AttachEngine3D
  Height = 17
  Placement = pos=(-60,-22,-315) rot=(0,0,1;0rad)
  Radius = 1.7
FEATURE [Part::Cylinder] Cylinder054099009079  label="Cylinder054099009179"
  Angle = 360
  AttacherType = Attacher::AttachEngine3D
  Height = 17
  Placement = pos=(-31,-22,-315) rot=(0,0,1;0rad)
  Radius = 1.7
FEATURE [Part::Cylinder] Cylinder054099009080  label="Cylinder054099009180"
  Angle = 360
  AttacherType = Attacher::AttachEngine3D
  Height = 17
  Placement = pos=(-35,-22,-315) rot=(0,0,1;0rad)
  Radius = 1.7
FEATURE [Part::Cylinder] Cylinder054099009081  label="Cylinder054099009181"
  Angle = 360
  AttacherType = Attacher::AttachEngine3D
  Height = 17
  Placement = pos=(-56,-22,-315) rot=(0,0,1;0rad)
  Radius = 1.7
FEATURE [Part::Box] Box112015002017004007004038086003009003024  label="Cube202"
  AttacherType = Attacher::AttachEngine3D
  Height = 10
  Length = 4
  Placement = pos=(-60,-23.7,-310) rot=(0,0,1;0rad)
  Width = 3.4
FEATURE [Part::Box] Box112015002017004007004038086003009003025  label="Cube203"
  AttacherType = Attacher::AttachEngine3D
  Height = 10
  Length = 4
  Placement = pos=(-35,-23.7,-310) rot=(0,0,1;0rad)
  Width = 3.4
FEATURE [Part::MultiFuse] Fusion051010010012015014088020028  label="pcb-brac-screw-slot-a001"
  Shapes = -> [Box112015002017004007004038086003009003025,Cylinder054099009080,Cylinder054099009079]
FEATURE [Part::MultiFuse] Fusion051010010012015014088020029  label="pcb-brac-screw-slot-b001"
  Shapes = -> [Box112015002017004007004038086003009003024,Cylinder054099009081,Cylinder054099009078]
FEATURE [Part::Cut] Cut456063
  Base = -> Box112015002017004007004038086003009003023
  Tool = -> Fusion051010010012015014088020028
FEATURE [Part::Cut] Cut456064
  Base = -> Cut456063
  Tool = -> Fusion051010010012015014088020029
FEATURE [Part::Chamfer] Chamfer006012060
  Base = -> Cut456064
  Edges = 5 edges r=2: [Edge28,Edge29,Edge30,Edge31,Edge32]
FEATURE [Part::Chamfer] Chamfer006012061
  Base = -> Chamfer006012060
  Edges = 5 edges r=2: [Edge10,Edge11,Edge12,Edge13,Edge14]
FEATURE [Part::MultiFuse] Fusion051010010012015014088020030
  Shapes = -> [Chamfer006012061,Cylinder054099009076]
FEATURE [Part::Cut] Cut456065
  Base = -> Fusion051010010012015014088020030
  Tool = -> Cylinder054099009077
FEATURE [Part::Fillet] Fillet043  label="pcb-bracket-blank002"
  Base = -> Cut456065
  Edges = 3 edges r=2: [Edge23,Edge25,Edge28]
FEATURE [Part::Mirroring] Part__Mirroring005044  label="Cube201 (Mirror #34)"
  Base = (0,0,0)
  Normal = (0,1,0)
  Source = -> Box112015002017004007004038086003009003023
FEATURE [Part::Mirroring] Part__Mirroring005047  label="Cylinder054099009130 (Mirror #37)"
  Base = (0,0,0)
  Normal = (0,1,0)
  Source = -> Cylinder054099009078
FEATURE [Part::Mirroring] Part__Mirroring005048  label="Cylinder054099009131 (Mirror #38)"
  Base = (0,0,0)
  Normal = (0,1,0)
  Source = -> Cylinder054099009079
FEATURE [Part::Mirroring] Part__Mirroring005049  label="Cylinder054099009132 (Mirror #39)"
  Base = (0,0,0)
  Normal = (0,1,0)
  Source = -> Cylinder054099009080
FEATURE [Part::Mirroring] Part__Mirroring005050  label="Cylinder054099009133 (Mirror #40)"
  Base = (0,0,0)
  Normal = (0,1,0)
  Source = -> Cylinder054099009081
FEATURE [Part::Mirroring] Part__Mirroring005051  label="Cube202 (Mirror #41)"
  Base = (0,0,0)
  Normal = (0,1,0)
  Source = -> Box112015002017004007004038086003009003024
FEATURE [Part::Mirroring] Part__Mirroring005052  label="Cube203 (Mirror #42)"
  Base = (0,0,0)
  Normal = (0,1,0)
  Source = -> Box112015002017004007004038086003009003025
FEATURE [Part::MultiFuse] Fusion051010010012015014088020031
  Shapes = -> [Part__Mirroring005047,Part__Mirroring005050,Part__Mirroring005051]
FEATURE [Part::MultiFuse] Fusion051010010012015014088020032
  Shapes = -> [Part__Mirroring005048,Part__Mirroring005049,Part__Mirroring005052]
FEATURE [Part::Cut] Cut456066
  Base = -> Part__Mirroring005044
  Tool = -> Fusion051010010012015014088020031
FEATURE [Part::Cut] Cut456067
  Base = -> Cut456066
  Tool = -> Fusion051010010012015014088020032
FEATURE [Part::Chamfer] Chamfer006012062
  Base = -> Cut456067
  Edges = 5 edges r=2: [Edge23,Edge24,Edge25,Edge26,Edge27]
FEATURE [Part::Cut] Cut456070  label="6131 base arm R001"
  Base = -> Cut449
  Placement = pos=(-184.5,-108.253,0) rot=(0,0,-1;1.5708rad)
  Tool = -> Fusion051010010012015014081
FEATURE [Part::Box] Box112015002017004007004038086003009003026  label="Cube204"
  AttacherType = Attacher::AttachEngine3D
  Height = 29
  Length = 61
  Placement = pos=(-114,-17,-302) rot=(0,0,1;0rad)
  Width = 54
FEATURE [Part::Chamfer] Chamfer006012067
  Base = -> Box112015002017004007004038086003009003026
  Edges = 1 edges r=14: [Edge12]
FEATURE [Part::Box] Box112015002017004007004038086003009003027  label="Cube205"
  AttacherType = Attacher::AttachEngine3D
  Height = 29
  Length = 76
  Placement = pos=(-122,18.3,-306) rot=(0,0,1;0rad)
  Width = 25
FEATURE [Part::Chamfer] Chamfer006012068
  Base = -> Box112015002017004007004038086003009003027
  Edges = 1 edges r=19.6: [Edge12]
FEATURE [Part::Cut] Cut456071
  Base = -> Chamfer006012067
  Tool = -> Chamfer006012068
FEATURE [Part::Box] Box112015002017004007004038086003009003028  label="Cube206"
  AttacherType = Attacher::AttachEngine3D
  Height = 34
  Length = 91
  Placement = pos=(-96,-75,-304) rot=(0,0,1;0.523599rad)
  Width = 54
FEATURE [Part::Cut] Cut456072
  Base = -> Cut456071
  Tool = -> Box112015002017004007004038086003009003028
FEATURE [Part::Box] Box112015002017004007004038086003009003029  label="Cube207"
  AttacherType = Attacher::AttachEngine3D
  Height = 29
  Length = 66
  Placement = pos=(-117,-38,-312) rot=(0,0,1;0rad)
  Width = 54
FEATURE [Part::Cut] Cut456073
  Base = -> Cut456072
  Tool = -> Box112015002017004007004038086003009003029
FEATURE [Part::Box] Box112015002017004007004038086003009003030  label="Cube208"
  AttacherType = Attacher::AttachEngine3D
  Height = 29
  Length = 66
  Placement = pos=(-117,-38,-278) rot=(0,0,1;0rad)
  Width = 54
FEATURE [Part::Chamfer] Chamfer006012069
  Base = -> Box112015002017004007004038086003009003030
  Edges = 1 edges r=10: [Edge11]
  Placement = pos=(0,6,0) rot=(0,0,1;0rad)
FEATURE [Part::Cut] Cut456074
  Base = -> Cut456073
  Tool = -> Chamfer006012069
FEATURE [Part::Chamfer] Chamfer006012070
  Base = -> Cut456074
  Edges = 1 edges r=12: [Edge22]
FEATURE [Part::Box] Box112015002017004007004038086003009003031  label="Cube209"
  AttacherType = Attacher::AttachEngine3D
  Height = 29
  Length = 66
  Placement = pos=(-104.5,-64,-312) rot=(0,0,1;0.523599rad)
  Width = 54
FEATURE [Part::Cut] Cut456075
  Base = -> Chamfer006012070
  Tool = -> Box112015002017004007004038086003009003031
FEATURE [Part::Cylinder] Cylinder054099009083  label="Cylinder054099009183"
  Angle = 360
  AttacherType = Attacher::AttachEngine3D
  Height = 50
  Placement = pos=(-74.45,7.95,-319) rot=(0,0,1;0rad)
  Radius = 2.2
FEATURE [Part::Cylinder] Cylinder054099009084  label="Cylinder054099009184"
  Angle = 360
  AttacherType = Attacher::AttachEngine3D
  Height = 50
  Placement = pos=(-104.75,-9.55,-319) rot=(0,0,1;0rad)
  Radius = 2.2
FEATURE [Part::Cut] Cut456076
  Base = -> Cut456075
  Tool = -> Cylinder054099009083
FEATURE [Part::Cut] Cut456077
  Base = -> Cut456076
  Tool = -> Cylinder054099009084
FEATURE [Part::Cylinder] Cylinder054099009085  label="Cylinder054099009185"
  Angle = 360
  AttacherType = Attacher::AttachEngine3D
  Height = 10
  Placement = pos=(-83,23,-297) rot=(1,0,0;1.5708rad)
  Radius = 1.7
FEATURE [Part::Cylinder] Cylinder054099009086  label="Cylinder054099009186"
  Angle = 360
  AttacherType = Attacher::AttachEngine3D
  Height = 10
  Placement = pos=(-58,24,-297) rot=(1,0,0;1.5708rad)
  Radius = 1.7
FEATURE [Part::Cylinder] Cylinder054099009087  label="Cylinder054099009187"
  Angle = 360
  AttacherType = Attacher::AttachEngine3D
  Height = 10
  Placement = pos=(-83,16,-297) rot=(1,0,0;1.5708rad)
  Radius = 4
FEATURE [Part::Cylinder] Cylinder054099009088  label="Cylinder054099009188"
  Angle = 360
  AttacherType = Attacher::AttachEngine3D
  Height = 10
  Placement = pos=(-58,16,-297) rot=(1,0,0;1.5708rad)
  Radius = 4
FEATURE [Part::Cut] Cut456078
  Base = -> Cut456077
  Tool = -> Cylinder054099009085
FEATURE [Part::Cut] Cut456079
  Base = -> Cut456078
  Tool = -> Cylinder054099009086
FEATURE [Part::Cut] Cut456080
  Base = -> Cut456079
  Tool = -> Cylinder054099009088
FEATURE [Part::Cut] Cut456081
  Base = -> Cut456080
  Tool = -> Cylinder054099009087
FEATURE [Part::Cylinder] Cylinder054099009089  label="Cylinder054099009189"
  Angle = 360
  AttacherType = Attacher::AttachEngine3D
  Height = 10
  Placement = pos=(-102,31,-289) rot=(-1,0,0;0.785398rad)
  Radius = 1.7
FEATURE [Part::Cylinder] Cylinder054099009090  label="Cylinder054099009190"
  Angle = 360
  AttacherType = Attacher::AttachEngine3D
  Height = 10
  Placement = pos=(-96,31,-289) rot=(-1,0,0;0.785398rad)
  Radius = 1.7
FEATURE [Part::Box] Box112015002017004007004038086003009003032  label="Cube210"
  AttacherType = Attacher::AttachEngine3D
  Height = 10
  Length = 6
  Placement = pos=(-102,30,-287.6) rot=(-1,0,0;0.785398rad)
  Width = 3.4
FEATURE [Part::MultiFuse] Fusion051010010012015014088020034
  Shapes = -> [Box112015002017004007004038086003009003032,Cylinder054099009090,Cylinder054099009089]
FEATURE [Part::Cut] Cut456082
  Base = -> Cut456081
  Tool = -> Fusion051010010012015014088020034
FEATURE [Part::Box] Box112015002017004007004038086003009003033  label="Cube211"
  AttacherType = Attacher::AttachEngine3D
  Height = 32
  Length = 80
  Placement = pos=(-120,48,-300) rot=(0,0,-1;0.401426rad)
  Width = 40
FEATURE [Part::Cut] Cut456083
  Base = -> Cut456082
  Tool = -> Box112015002017004007004038086003009003033
FEATURE [Part::Fillet] Fillet046  label="6173 Extruder Drive Bracket"
  Base = -> Cut456083
  Edges = 1 edges r=10: [Edge47]
  Placement = pos=(-106.521,184.5,0) rot=(0,0,1;1.0472rad)
FEATURE [App::DocumentObjectGroup] Group016  label="Wire Tensioner"
  Group = -> [Cylinder054055,Cut301]
FEATURE [Part::Sphere] Sphere006006006006026  label="ball-r-3.x-e-change-radius-here"
  Angle1 = -90
  Angle2 = 90
  Angle3 = 360
  AttacherType = Attacher::AttachEngine3D
  Placement = pos=(-15,-20,-5) rot=(0,0,1;0rad)
  Radius = 3.3
FEATURE [Part::Mirroring] Part__Mirroring005054  label="ball-r-3.x-e"
  Base = (0,0,0)
  Normal = (0,1,0)
  Placement = pos=(-110,0,-130) rot=(0,1,0;3.14159rad)
  Source = -> Sphere006006006006026
FEATURE [Part::Sphere] Sphere006006006006027  label="ball-r-3.x-f-change-radius-here"
  Angle1 = -90
  Angle2 = 90
  Angle3 = 360
  AttacherType = Attacher::AttachEngine3D
  Placement = pos=(-95,-20,-125) rot=(0,1,0;3.14159rad)
  Radius = 3.3
FEATURE [Part::Fuse] Fusion051010010012015014088020035  label="balls-2"
  Base = -> Part__Mirroring005054
  Placement = pos=(-180,103.923,0) rot=(0,0,1;2.0944rad)
  Tool = -> Sphere006006006006027
FEATURE [Part::Sphere] Sphere006006006006028  label="ball-r-3.x-g-change-radius-here"
  Angle1 = -90
  Angle2 = 90
  Angle3 = 360
  AttacherType = Attacher::AttachEngine3D
  Placement = pos=(-15,-20,-5) rot=(0,0,1;0rad)
  Radius = 3.3
FEATURE [Part::Mirroring] Part__Mirroring005055  label="ball-r-3.x-g"
  Base = (0,0,0)
  Normal = (0,1,0)
  Placement = pos=(-110,0,-130) rot=(0,1,0;3.14159rad)
  Source = -> Sphere006006006006028
FEATURE [Part::Sphere] Sphere006006006006029  label="ball-r-3.x-h-change-radius-here"
  Angle1 = -90
  Angle2 = 90
  Angle3 = 360
  AttacherType = Attacher::AttachEngine3D
  Placement = pos=(-95,-20,-125) rot=(0,1,0;3.14159rad)
  Radius = 3.3
FEATURE [Part::Fuse] Fusion051010010012015014088020036  label="balls-3"
  Base = -> Part__Mirroring005055
  Placement = pos=(-180,-103.923,0) rot=(0,0,-1;2.0944rad)
  Tool = -> Sphere006006006006029
FEATURE [Part::Cut] Cut456084
  Base = -> Cut456038
  Tool = -> Fusion051010010012015014088020035
FEATURE [Part::Cut] Cut456085  label="6175 Hot End Shell"
  Base = -> Cut456084
  Tool = -> Fusion051010010012015014088020036
FEATURE [Part::Feature] Part__Feature001  label="279 623 Bearing"
  Placement = pos=(9.07675,1.10653,19.1765) rot=(0,0,-1;0.854815rad)
  shape: bbox 10 x 10 x 4 mm, 22 faces (baked)
FEATURE [Part::Feature] Part__Feature162  label="1308 Upper Lever (Printed)"
  Placement = pos=(10.0613,-0.0251403,11.4765) rot=(0,0,1;0rad)
  shape: bbox 28.5 x 62 x 5 mm, 26 faces (baked)
FEATURE [Part::Feature] Part__Feature163  label="1309 Lower Lever"
  Placement = pos=(10.0613,-0.0251403,22.9765) rot=(0,0,1;0rad)
  shape: bbox 39.69 x 36.58 x 16.55 mm, 81 faces (baked)
FEATURE [Part::Feature] Part__Feature004  label="1193 M4 Nut"
  Placement = pos=(14.872,22.0306,18.4765) rot=(0.654654,-0.377964,0.654654;3.86433rad)
  shape: bbox 3.2 x 7 x 8.083 mm, 26 faces (baked)
FEATURE [Part::Feature] Part__Feature164  label="650 M4 x 35mm Button head screw "
  Placement = pos=(49.872,22.0306,18.4765) rot=(0.684919,0.248542,0.684919;2.65438rad)
  shape: bbox 37.2 x 8.193 x 8.193 mm, 18 faces (baked)
FEATURE [Part::Feature] Part__Feature006  label="1185 M4 Washer"
  Placement = pos=(24.2613,22.0306,18.4765) rot=(0.339065,0.877536,0.339065;1.70106rad)
  shape: bbox 0.8 x 9 x 9 mm, 6 faces (baked)
FEATURE [Part::Feature] Part__Feature007  label="212 M3 Washer"
  Placement = pos=(10.0613,-0.0251403,16.1765) rot=(0,0,-1;0.75451rad)
  shape: bbox 7 x 7 x 0.5 mm, 6 faces (baked)
FEATURE [Part::Feature] Part__Feature008  label="257 M3 x 12mm Cap Screw"
  Placement = pos=(10.0613,-0.0251403,30.9765) rot=(0,0,1;0.491522rad)
  shape: bbox 5.7 x 5.7 x 15 mm, 16 faces (baked)
FEATURE [Part::Feature] Part__Feature010  label="212 M3 Washer001"
  Placement = pos=(0.0612844,0.0305878,25.8765) rot=(0,0,-1;0.874671rad)
  shape: bbox 7 x 7 x 0.5 mm, 6 faces (baked)
FEATURE [Part::Feature] Part__Feature011  label="212M3 Washer002"
  Placement = pos=(10.0613,-0.0251403,20.6765) rot=(0,0,-1;0.75451rad)
  shape: bbox 7 x 7 x 0.5 mm, 6 faces (baked)
FEATURE [Part::Feature] Part__Feature012  label="448 Hobbed Insert"
  Placement = pos=(0.0612844,0.0305878,21.8765) rot=(1,0,0;3.14159rad)
  shape: bbox 8.761 x 8.744 x 6.4 mm, 204 faces (baked)
FEATURE [Part::Feature] Part__Feature013  label="423 MR93ZZ Bearing"
  Placement = pos=(0.0612844,0.0305878,12.9765) rot=(0.998561,-0.053634,0;3.14159rad)
  shape: bbox 9 x 9 x 4 mm, 22 faces (baked)
FEATURE [Part::Feature] Part__Feature014  label="423 MR93ZZ Bearing001"
  Placement = pos=(0.0612844,0.0305878,23.3765) rot=(0.296391,0.955067,0;3.14159rad)
  shape: bbox 9 x 9 x 4 mm, 22 faces (baked)
FEATURE [Part::Feature] Part__Feature015  label="113 M3 x 25mm Hex Screw"
  Placement = pos=(0.0612844,0.0305878,7.57647) rot=(-0.06344,0.997986,0;3.14159rad)
  shape: bbox 6.3 x 5.858 x 27.5 mm, 19 faces (baked)
FEATURE [Part::Feature] Part__Feature016  label="204 M3 Nylock Nut"
  Placement = pos=(0.0612844,0.0305878,26.3765) rot=(0,0,1;0.184869rad)
  shape: bbox 6.243 x 5.99 x 4 mm, 28 faces (baked)
FEATURE [Part::Feature] Part__Feature017  label="1310_ISO - RH Helical gear 1M 17T 45HA 20PA 12FW ---17A75H50L0.8N"
  Placement = pos=(-0.129787,7.22389,44) rot=(0.464719,0.753705,-0.464719;1.84986rad)
  shape: bbox 18 x 18 x 13.32 mm, 178 faces (baked)
FEATURE [Part::Feature] Part__Feature018  label="1311 Large Gear"
  Placement = pos=(0.0612844,0.0305878,4.97647) rot=(0.706394,0.044904,0.706394;3.23134rad)
  shape: bbox 37.39 x 37.38 x 6 mm, 421 faces (baked)
FEATURE [Part::Feature] Part__Feature019  label="1306"
  Placement = pos=(-0.129787,7.22389,26.0235) rot=(0,0,-1;1.5708rad)
  shape: bbox 70.89 x 54.16 x 21.5 mm, 245 faces (baked)
FEATURE [Part::Feature] Part__Feature020  label="257 M3 x 12mm Cap Screw001"
  Placement = pos=(10.0613,8.97486,30.9765) rot=(0,0,1;3.17375rad)
  shape: bbox 5.7 x 5.7 x 15 mm, 16 faces (baked)
FEATURE [Part::Feature] Part__Feature021  label="257 M3 x 12mm Cap Screw002"
  Placement = pos=(30.0613,13.9749,30.9765) rot=(0,0,1;3.7378rad)
  shape: bbox 5.7 x 5.7 x 15 mm, 16 faces (baked)
FEATURE [Part::Feature] Part__Feature026  label="212M3 Washer003"
  Placement = pos=(0.0612844,0.0305878,10.9765) rot=(0,0,-1;0.75451rad)
  shape: bbox 7 x 7 x 0.5 mm, 6 faces (baked)
FEATURE [Part::Cylinder] Cylinder015
  Angle = 360
  AttacherType = Attacher::AttachEngine3D
  Height = 19
  Radius = 14
FEATURE [Part::Box] Box012  label="Cube012"
  AttacherType = Attacher::AttachEngine3D
  Height = 16.5
  Length = 10
  Placement = pos=(5.5,-7.25,2.5) rot=(0,0,1;0rad)
  Width = 14.5
FEATURE [Part::Box] Box013  label="Cube013"
  AttacherType = Attacher::AttachEngine3D
  Height = 0.8
  Length = 7
  Placement = pos=(-3.5,-21,18.2) rot=(0,0,1;0rad)
  Width = 42
FEATURE [Part::Cylinder] Cylinder016  label="mounting-hole-013"
  Angle = 360
  AttacherType = Attacher::AttachEngine3D
  Height = 20
  Placement = pos=(0,17.5,14) rot=(0,0,1;0rad)
  Radius = 2
FEATURE [Part::Cylinder] Cylinder017  label="mounting-hole-014"
  Angle = 360
  AttacherType = Attacher::AttachEngine3D
  Height = 20
  Placement = pos=(0,-17.5,14) rot=(0,0,1;0rad)
  Radius = 2
FEATURE [Part::Fillet] Fillet012
  Base = -> Box013
  Edges = 1 edges r=3: [Edge5]
FEATURE [Part::Fillet] Fillet013
  Base = -> Fillet012
  Edges = 1 edges r=3: [Edge15]
FEATURE [Part::Fillet] Fillet014
  Base = -> Fillet013
  Edges = 1 edges r=3: [Edge14]
FEATURE [Part::Fillet] Fillet015
  Base = -> Fillet014
  Edges = 1 edges r=3: [Edge16]
FEATURE [Part::Cylinder] Cylinder018  label="motor-shaft-cylinder003"
  Angle = 360
  AttacherType = Attacher::AttachEngine3D
  Height = 28
  Placement = pos=(-8,0,1) rot=(0,0,1;0rad)
  Radius = 2.7
FEATURE [Part::Cylinder] Cylinder019  label="shaft-boss003"
  Angle = 360
  AttacherType = Attacher::AttachEngine3D
  Height = 19.5
  Placement = pos=(-8,0,1) rot=(0,0,1;0rad)
  Radius = 4.5
FEATURE [Part::Box] Box014  label="Cube014"
  AttacherType = Attacher::AttachEngine3D
  Height = 10
  Length = 10
  Placement = pos=(-6.4,-5,22.5) rot=(0,0,1;0rad)
  Width = 10
FEATURE [Part::Box] Box015  label="Cube015"
  AttacherType = Attacher::AttachEngine3D
  Height = 10
  Length = 10
  Placement = pos=(-19.6,-5,22.5) rot=(0,0,1;0rad)
  Width = 10
FEATURE [Part::Cut] Cut012
  Base = -> Cylinder018
  Tool = -> Box015
FEATURE [Part::Cut] Cut013  label="motor-shaft003"
  Base = -> Cut012
  Tool = -> Box014
FEATURE [Part::MultiFuse] Fusion012
  Shapes = -> [Cylinder015,Box012]
FEATURE [Part::MultiFuse] Fusion013
  Shapes = -> [Fusion012,Fillet015]
FEATURE [Part::MultiFuse] Fusion014
  Shapes = -> [Fusion013,Cylinder019]
FEATURE [Part::Cut] Cut014
  Base = -> Fusion014
  Tool = -> Cylinder016
FEATURE [Part::Cut] Cut015  label="motor-body003"
  Base = -> Cut014
  Tool = -> Cylinder017
FEATURE [Part::MultiFuse] Fusion015  label="28BYJ-48-motor003"
  Placement = pos=(7.9,7,7) rot=(0,0,1;0rad)
  Shapes = -> [Cut013,Cut015]
FEATURE [Part::Mirroring] Part__Mirroring005056  label="6170 28BYJ48 Motor"
  Base = (0,0,0)
  Normal = (0,0,1)
  Placement = pos=(-7.49527,-8.28826,30) rot=(0,0,1;2.67035rad)
  Source = -> Fusion015
FEATURE [Part::Box] Box016  label="Cube016"
  AttacherType = Attacher::AttachEngine3D
  Height = 70
  Length = 70
  Placement = pos=(-66,-27,0) rot=(0,0,1;0rad)
  Width = 70
FEATURE [Part::Cut] Cut016
  Base = -> Part__Feature019
  Tool = -> Box016
FEATURE [Part::Box] Box017  label="Cube017"
  AttacherType = Attacher::AttachEngine3D
  Height = 24
  Length = 18
  Placement = pos=(2,-13.8,26) rot=(0,0,1;0rad)
  Width = 42
FEATURE [Part::Box] Box018  label="Cube018"
  AttacherType = Attacher::AttachEngine3D
  Height = 10
  Length = 10
  Placement = pos=(14,-18,40.5) rot=(0,0,1;0rad)
  Width = 10
FEATURE [Part::Box] Box019  label="Cube019"
  AttacherType = Attacher::AttachEngine3D
  Height = 10
  Length = 10
  Placement = pos=(14,20,40.5) rot=(0,0,1;0rad)
  Width = 10
FEATURE [Part::MultiFuse] Fusion016
  Shapes = -> [Box018,Box019]
FEATURE [Part::Cut] Cut017
  Base = -> Cut016
  Tool = -> Fusion016
FEATURE [Part::MultiFuse] Fusion017
  Shapes = -> [Box017,Cut017]
FEATURE [Part::Cylinder] Cylinder020  label="Cylinder016"
  Angle = 360
  AttacherType = Attacher::AttachEngine3D
  Height = 15
  Placement = pos=(25,7.3,40.5) rot=(0,0,1;0rad)
  Radius = 20
FEATURE [Part::Cylinder] Cylinder021  label="Cylinder017"
  Angle = 360
  AttacherType = Attacher::AttachEngine3D
  Height = 22
  Placement = pos=(0,7.3,37.5) rot=(0,0,1;0rad)
  Radius = 10.5
FEATURE [Part::MultiFuse] Fusion018
  Shapes = -> [Cylinder020,Cylinder021]
FEATURE [Part::Cut] Cut018
  Base = -> Fusion017
  Tool = -> Fusion018
FEATURE [Part::Cylinder] Cylinder022  label="Cylinder018"
  Angle = 360
  AttacherType = Attacher::AttachEngine3D
  Height = 10
  Placement = pos=(0,7,30.7) rot=(0,0,1;0rad)
  Radius = 13
FEATURE [Part::Cut] Cut019
  Base = -> Part__Feature017
  Tool = -> Cylinder022
FEATURE [Part::Cylinder] Cylinder023  label="Cylinder019"
  Angle = 360
  AttacherType = Attacher::AttachEngine3D
  Height = 6.7
  Placement = pos=(-0.15,7.2,40.7) rot=(0,0,1;0rad)
  Radius = 6
FEATURE [Part::MultiFuse] Fusion019
  Shapes = -> [Cut019,Cylinder023]
FEATURE [Part::Cut] Cut020  label="motor-shaft004"
  Base = -> Cut012
  Tool = -> Box014
FEATURE [Part::Mirroring] Part__Mirroring001  label="motor-shaft004 (Mirror #2)"
  Base = (0,0,0)
  Normal = (0,0,1)
  Placement = pos=(7.9,7.2,69) rot=(0,0,1;0rad)
  Source = -> Cut020
FEATURE [Part::Cut] Cut021  label="6171 Drive Gear"
  Base = -> Fusion019
  Placement = pos=(-8.79107,7.25448,-60) rot=(0,0,1;3.14159rad)
  Tool = -> Part__Mirroring001
FEATURE [Part::Cylinder] Cylinder024  label="Cylinder020"
  Angle = 360
  AttacherType = Attacher::AttachEngine3D
  Height = 40
  Placement = pos=(5,-10.5,14) rot=(0,0,1;0rad)
  Radius = 2.1
FEATURE [Part::Cylinder] Cylinder025  label="Cylinder021"
  Angle = 360
  AttacherType = Attacher::AttachEngine3D
  Height = 40
  Placement = pos=(10,-10.5,14) rot=(0,0,1;0rad)
  Radius = 2.1
FEATURE [Part::Box] Box020  label="Cube020"
  AttacherType = Attacher::AttachEngine3D
  Height = 44
  Length = 5
  Placement = pos=(5,-12.6,11) rot=(0,0,1;0rad)
  Width = 4.2
FEATURE [Part::MultiFuse] Fusion020  label="m4-slot"
  Placement = pos=(0.5,35,0) rot=(0,0,1;0rad)
  Shapes = -> [Cylinder024,Cylinder025,Box020]
FEATURE [Part::MultiFuse] Fusion021  label="m4-slot001"
  Placement = pos=(0.5,0,0) rot=(0,0,1;0rad)
  Shapes = -> [Cylinder024,Cylinder025,Box020]
FEATURE [Part::Cut] Cut022
  Base = -> Cut018
  Tool = -> Fusion020
FEATURE [Part::Cut] Cut023  label="blank-body"
  Base = -> Cut022
  Tool = -> Fusion021
FEATURE [Part::Chamfer] Chamfer006012071
  Base = -> Cut023
  Edges = 3 edges r=0.5: [Edge7,Edge44,Edge45]
FEATURE [Part::Chamfer] Chamfer001
  Base = -> Chamfer006012071
  Edges = 5 edges r=0.5: [Edge76,Edge77,Edge78,Edge79,Edge80]
FEATURE [Part::Chamfer] Chamfer002
  Base = -> Chamfer001
  Edges = 5 edges r=0.5: [Edge10,Edge11,Edge12,Edge13,Edge14]
FEATURE [Part::Fillet] Fillet047
  Base = -> Chamfer002
  Edges = 1 edges r=2: [Edge205]
FEATURE [Part::Chamfer] Chamfer006012072
  Base = -> Fillet047
  Edges = 1 edges r=1: [Edge5]
FEATURE [Part::Cylinder] Cylinder054099009091  label="Cylinder054099009191"
  Angle = 360
  AttacherType = Attacher::AttachEngine3D
  Height = 10
  Placement = pos=(0,0,0) rot=(0,1,0;1.53589rad)
  Radius = 1.5
FEATURE [Part::Feature] Cylinder054099009092  label="Cylinder054099009192"
  Placement = pos=(0,0,0) rot=(-0.355767,0.858898,0.368408;1.68772rad)
  shape: bbox 9.189 x 9.189 x 3.347 mm, 3 faces (baked)
FEATURE [Part::Feature] Cylinder054099009093  label="Cylinder054099009193"
  Placement = pos=(0,0,0) rot=(-0.570514,0.570514,0.590785;2.07436rad)
  shape: bbox 3 x 10.1 x 3.347 mm, 3 faces (baked)
FEATURE [Part::Feature] Cylinder054099009094  label="Cylinder054099009194"
  Placement = pos=(0,0,0) rot=(-0.667573,0.276518,0.691292;2.58383rad)
  shape: bbox 9.189 x 9.189 x 3.347 mm, 3 faces (baked)
FEATURE [Part::Feature] Cylinder054099009095  label="Cylinder054099009195"
  Placement = pos=(0,0,0) rot=(-0.694658,0,0.71934;3.14159rad)
  shape: bbox 10.1 x 3 x 3.347 mm, 3 faces (baked)
FEATURE [Part::Feature] Cylinder054099009096  label="Cylinder054099009196"
  Placement = pos=(0,0,0) rot=(-0.667573,-0.276518,0.691292;3.69935rad)
  shape: bbox 9.189 x 9.189 x 3.347 mm, 3 faces (baked)
FEATURE [Part::Feature] Cylinder054099009097  label="Cylinder054099009197"
  Placement = pos=(0,0,0) rot=(0.570514,0.570514,-0.590785;2.07436rad)
  shape: bbox 3 x 10.1 x 3.347 mm, 3 faces (baked)
FEATURE [Part::Feature] Cylinder054099009098  label="Cylinder054099009198"
  Placement = pos=(0,0,0) rot=(0.355767,0.858898,-0.368408;1.68772rad)
  shape: bbox 9.189 x 9.189 x 3.347 mm, 3 faces (baked)
FEATURE [Part::Fuse] Fusion051010010012015014088020037
  Base = -> Cylinder054099009091
  Tool = -> Cylinder054099009092
FEATURE [Part::Fuse] Fusion051010010012015014088020038
  Base = -> Cylinder054099009098
  Tool = -> Fusion051010010012015014088020037
FEATURE [Part::Fuse] Fusion051010010012015014088020039
  Base = -> Cylinder054099009097
  Tool = -> Fusion051010010012015014088020038
FEATURE [Part::Fuse] Fusion051010010012015014088020040
  Base = -> Cylinder054099009096
  Tool = -> Fusion051010010012015014088020039
FEATURE [Part::Fuse] Fusion051010010012015014088020041
  Base = -> Cylinder054099009095
  Tool = -> Fusion051010010012015014088020040
FEATURE [Part::Fuse] Fusion051010010012015014088020042
  Base = -> Cylinder054099009094
  Tool = -> Fusion051010010012015014088020041
FEATURE [Part::Cylinder] Cylinder054099009099  label="Cylinder054099009199"
  Angle = 360
  AttacherType = Attacher::AttachEngine3D
  Height = 10
  Placement = pos=(0,0,0) rot=(0,1,0;1.53589rad)
  Radius = 1.5
FEATURE [Part::Feature] Cylinder054099009100  label="Cylinder054099009200"
  Placement = pos=(0,0,0) rot=(-0.2112,0.952661,0.218704;1.58438rad)
  shape: bbox 10.33 x 6.943 x 3.347 mm, 3 faces (baked)
FEATURE [Part::Feature] Cylinder054099009101  label="Cylinder054099009201"
  Placement = pos=(0,0,0) rot=(-0.387166,0.83028,0.400922;1.7213rad)
  shape: bbox 8.723 x 9.586 x 3.347 mm, 3 faces (baked)
FEATURE [Part::Feature] Cylinder054099009102  label="Cylinder054099009202"
  Placement = pos=(0,0,0) rot=(-0.514977,0.671131,0.533274;1.9269rad)
  shape: bbox 5.485 x 10.44 x 3.347 mm, 3 faces (baked)
FEATURE [Part::Feature] Cylinder054099009103  label="Cylinder054099009203"
  Placement = pos=(0,0,0) rot=(-0.600148,0.503584,0.621471;2.18023rad)
  shape: bbox 4.69 x 10.37 x 3.347 mm, 3 faces (baked)
FEATURE [Part::Feature] Cylinder054099009104  label="Cylinder054099009204"
  Placement = pos=(0,0,0) rot=(-0.653258,0.340065,0.676469;2.46442rad)
  shape: bbox 8.19 x 9.909 x 3.347 mm, 3 faces (baked)
FEATURE [Part::Cylinder] Cylinder054099009105  label="Cylinder054099009205"
  Angle = 360
  AttacherType = Attacher::AttachEngine3D
  Height = 10
  Placement = pos=(0,0,0) rot=(0.650802,0.391041,-0.650802;2.39607rad)
  Radius = 1.5
FEATURE [Part::Fuse] Fusion051010010012015014088020043
  Base = -> Cylinder054099009099
  Tool = -> Cylinder054099009100
FEATURE [Part::Fuse] Fusion051010010012015014088020044
  Base = -> Cylinder054099009105
  Tool = -> Fusion051010010012015014088020043
FEATURE [Part::Fuse] Fusion051010010012015014088020045
  Base = -> Cylinder054099009104
  Tool = -> Fusion051010010012015014088020044
FEATURE [Part::Fuse] Fusion051010010012015014088020046
  Base = -> Cylinder054099009103
  Tool = -> Fusion051010010012015014088020045
FEATURE [Part::Fuse] Fusion051010010012015014088020047
  Base = -> Cylinder054099009102
  Tool = -> Fusion051010010012015014088020046
FEATURE [Part::Box] Box112015002017004007004038086003009003034  label="Cube212"
  AttacherType = Attacher::AttachEngine3D
  Height = 15
  Length = 97
  Placement = pos=(-106,-39,105) rot=(0,0,1;0rad)
  Width = 20
FEATURE [Part::Chamfer] Chamfer006012074
  Base = -> Box112015002017004007004038086003009003034
  Edges = 1 edges r=13: [Edge9]
FEATURE [Part::Box] Box112015002017004007004038086003009003035  label="Cube213"
  AttacherType = Attacher::AttachEngine3D
  Height = 15
  Length = 30
  Placement = pos=(-120,-42,102) rot=(0,0,1;0rad)
  Width = 20
FEATURE [Part::Box] Box112015002017004007004038086003009003036  label="Cube214"
  AttacherType = Attacher::AttachEngine3D
  Height = 20
  Length = 35
  Placement = pos=(-123,-42,124) rot=(-1,0,0;0.785398rad)
  Width = 30
FEATURE [Part::MultiCommon] Common019
  Shapes = -> [Box112015002017004007004038086003009003035,Box112015002017004007004038086003009003036]
FEATURE [Part::Box] Box112015002017004007004038086003009003037  label="Cube215"
  AttacherType = Attacher::AttachEngine3D
  Height = 15
  Length = 34
  Placement = pos=(-123,-37,108) rot=(0,0,1;0rad)
  Width = 20
FEATURE [Part::MultiCommon] Common020
  Shapes = -> [Common019,Box112015002017004007004038086003009003037]
FEATURE [Part::Cut] Cut456086
  Base = -> Chamfer006012074
  Tool = -> Common020
FEATURE [Part::Box] Box112015002017004007004038086003009003038  label="Cube216"
  AttacherType = Attacher::AttachEngine3D
  Height = 10
  Length = 8
  Placement = pos=(-100,-31,119) rot=(0,0,1;0rad)
  Width = 3
FEATURE [Part::Fillet] Fillet048
  Base = -> Box112015002017004007004038086003009003038
  Edges = 1 edges r=1.4: [Edge1]
FEATURE [Part::Fillet] Fillet049
  Base = -> Fillet048
  Edges = 1 edges r=1.4: [Edge3]
FEATURE [Part::Fillet] Fillet050
  Base = -> Fillet049
  Edges = 1 edges r=1.4: [Edge18]
FEATURE [Part::Fillet] Fillet051
  Base = -> Fillet050
  Edges = 1 edges r=1.4: [Edge15]
  Placement = pos=(-3,2,-4) rot=(0,0,1;0rad)
FEATURE [Part::Cut] Cut456087
  Base = -> Cut456086
  Tool = -> Fillet051
FEATURE [Part::Fuse] Fusion051010010012015014088020048  label="full-fan003"
  Base = -> Cylinder054099009093
  Placement = pos=(-99,-28,112) rot=(-1,0,0;0.785398rad)
  Tool = -> Fusion051010010012015014088020042
FEATURE [Part::Cylinder] Cylinder054099009106  label="chop003"
  Angle = 360
  AttacherType = Attacher::AttachEngine3D
  Height = 7
  Placement = pos=(-99,-31.1213,109.879) rot=(-1,0,0;0.785398rad)
  Radius = 5
FEATURE [Part::Fuse] Fusion051010010012015014088020049  label="half-fan003"
  Base = -> Cylinder054099009101
  Placement = pos=(-97,-23,115) rot=(0.173624,0.696367,-0.696367;2.79777rad)
  Tool = -> Fusion051010010012015014088020047
FEATURE [Part::MultiCommon] Common021
  Placement = pos=(0,-0.2,0) rot=(0,0,1;0rad)
  Shapes = -> [Fusion051010010012015014088020048,Cylinder054099009106]
FEATURE [Part::Cylinder] Cylinder054099009107  label="Cylinder054099009206"
  Angle = 360
  AttacherType = Attacher::AttachEngine3D
  Height = 10
  Placement = pos=(-97,-20,115) rot=(1,0,0;1.5708rad)
  Radius = 6
FEATURE [Part::MultiCommon] Common022
  Shapes = -> [Fusion051010010012015014088020049,Cylinder054099009107]
FEATURE [Part::Box] Box112015002017004007004038086003009003039  label="Cube217"
  AttacherType = Attacher::AttachEngine3D
  Height = 10
  Length = 10
  Placement = pos=(-103,-35,116) rot=(0,0,1;0rad)
  Width = 10
FEATURE [Part::Cut] Cut456088
  Base = -> Common021
  Placement = pos=(3,0,0) rot=(0,0,1;0rad)
  Tool = -> Box112015002017004007004038086003009003039
FEATURE [Part::Cut] Cut456089
  Base = -> Cut456087
  Tool = -> Cut456088
FEATURE [Part::Cut] Cut456090
  Base = -> Cut456089
  Placement = pos=(0,0,0) rot=(0,0,1;0.523599rad)
  Tool = -> Common022
FEATURE [Part::Chamfer] Chamfer006012075
  Base = -> Cut456090
  Edges = 1 edges r=15: [Edge10]
FEATURE [Part::Box] Box112015002017004007004038086003009003040  label="Cube218"
  AttacherType = Attacher::AttachEngine3D
  Height = 26
  Length = 22
  Placement = pos=(-11,-30,101) rot=(0,0,1;0rad)
  Width = 22
FEATURE [Part::Cut] Cut456091
  Base = -> Chamfer006012075
  Tool = -> Box112015002017004007004038086003009003040
FEATURE [Part::Cylinder] Cylinder054099009108  label="Cylinder054099009207"
  Angle = 360
  AttacherType = Attacher::AttachEngine3D
  Height = 50
  Placement = pos=(-6,-19,111) rot=(1,0,0;1.5708rad)
  Radius = 1.7
FEATURE [Part::Cylinder] Cylinder054099009109  label="Cylinder054099009208"
  Angle = 360
  AttacherType = Attacher::AttachEngine3D
  Height = 50
  Placement = pos=(-6,-36,111) rot=(1,0,0;1.5708rad)
  Radius = 3
FEATURE [Part::Cut] Cut456092
  Base = -> Cut456091
  Tool = -> Cylinder054099009108
FEATURE [Part::Cut] Cut456093  label="top-arm-002"
  Base = -> Cut456092
  Placement = pos=(0,0,0) rot=(0,0,-1;0.523599rad)
  Tool = -> Cylinder054099009109
FEATURE [Part::Cylinder] Cylinder054099009110  label="Cylinder054099009209"
  Angle = 360
  AttacherType = Attacher::AttachEngine3D
  Height = 20
  Placement = pos=(-33,-22,101) rot=(0,0,1;0rad)
  Radius = 1.3
FEATURE [Part::Cylinder] Cylinder054099009111  label="Cylinder054099009210"
  Angle = 360
  AttacherType = Attacher::AttachEngine3D
  Height = 20
  Placement = pos=(-33,-13,115) rot=(1,0,0;1.5708rad)
  Radius = 1.3
FEATURE [Part::Fuse] Fusion051010010012015014088020050
  Base = -> Cylinder054099009110
  Tool = -> Cylinder054099009111
FEATURE [Part::Fuse] Fusion051010010012015014088020051
  Base = -> Cylinder054099009110
  Placement = pos=(-50,0,0) rot=(0,0,1;0rad)
  Tool = -> Cylinder054099009111
FEATURE [Part::Fuse] Fusion051010010012015014088020052
  Base = -> Cylinder054099009110
  Placement = pos=(-25,0,0) rot=(0,0,1;0rad)
  Tool = -> Cylinder054099009111
FEATURE [Part::Cut] Cut456094
  Base = -> Cut456093
  Tool = -> Fusion051010010012015014088020050
FEATURE [Part::Cut] Cut456095
  Base = -> Cut456094
  Tool = -> Fusion051010010012015014088020052
FEATURE [Part::Cut] Cut456096  label="6135 top arm R001"
  Base = -> Cut456095
  Placement = pos=(0,0,0) rot=(0,0,1;0.523599rad)
  Tool = -> Fusion051010010012015014088020051
FEATURE [Part::Mirroring] Part__Mirroring005057  label="6134 top arm L"
  Base = (0,0,0)
  Normal = (0,1,0)
  Source = -> Cut456096
FEATURE [App::DocumentObjectGroup] Group019  label="6133 Top Link"
  Group = -> [Cut453,Cut414,Cut456096,Part__Mirroring005057]
FEATURE [App::DocumentObjectGroup] Group020  label="6163 Bed Mounts"
  Group = -> [Cylinder054099009019,Part__Mirroring005028,Sphere006006006006018,Cut456040,Cut456040_cs]
FEATURE [App::DocumentObjectGroup] Group021  label="6174 Old Hot End"
  Group = -> [Part__Feature127,Part__Feature121,Part__Feature121_cs,Cut456085]
FEATURE [Part::Cone] Cone027  label="Cone019"
  Angle = 360
  AttacherType = Attacher::AttachEngine3D
  Height = 20
  Placement = pos=(0,0,-39) rot=(0,0,1;0rad)
  Radius1 = 2.75
  Radius2 = 4
FEATURE [Part::Box] Box112015002017004007004038086003009003041  label="Cube219"
  AttacherType = Attacher::AttachEngine3D
  Height = 34
  Length = 14
  Placement = pos=(-7,-10,-52) rot=(0,0,1;0rad)
  Width = 10
FEATURE [Part::Cut] Cut456097
  Base = -> Cone027
  Tool = -> Box112015002017004007004038086003009003041
FEATURE [Part::Cut] Cut456098
  Base = -> Fusion051010010012015014088020016
  Tool = -> Cut456097
FEATURE [Part::Chamfer] Chamfer006012076  label="6153.1-Angled-half-arm"
  Base = -> Cut456098
  Edges = 3 edges r=1: [Edge133,Edge134,Edge162]
  Placement = pos=(-71,0,0) rot=(0,0,1;0rad)
FEATURE [Part::Cone] Cone028  label="Cone020"
  Angle = 360
  AttacherType = Attacher::AttachEngine3D
  Height = 4
  Placement = pos=(-21,18,-5) rot=(1,0,0;1.5708rad)
  Radius1 = 3
  Radius2 = 5
FEATURE [Part::Box] Box112015002017004007004038086003009003042  label="Cube220"
  AttacherType = Attacher::AttachEngine3D
  Height = 10
  Length = 19.5
  Placement = pos=(-26,25,-10) rot=(0,0,1;0rad)
  Width = 5
FEATURE [Part::Cylinder] Cylinder054099009112  label="Cylinder054099009211"
  Angle = 360
  AttacherType = Attacher::AttachEngine3D
  Height = 31
  Placement = pos=(-14,35,-5) rot=(1,0,0;1.5708rad)
  Radius = 1.4
FEATURE [Part::Cylinder] Cylinder054099009113  label="Cylinder054099009212"
  Angle = 360
  AttacherType = Attacher::AttachEngine3D
  Height = 31
  Placement = pos=(-14,35,-5) rot=(1,0,0;1.5708rad)
  Radius = 1.7
FEATURE [Part::Sphere] Sphere006006006006030  label="ball-r-32-b-change-radius-here001"
  Angle1 = -90
  Angle2 = 90
  Angle3 = 360
  AttacherType = Attacher::AttachEngine3D
  Placement = pos=(-21,20,-5) rot=(0,0,1;0rad)
  Radius = 3.2
FEATURE [Part::Box] Box112015002017004007004038086003009003043  label="Cube221"
  AttacherType = Attacher::AttachEngine3D
  Height = 18
  Length = 19.5
  Placement = pos=(-31,14,-13) rot=(0,0,1;0rad)
  Width = 20
FEATURE [Part::Box] Box112015002017004007004038086003009003045  label="Cube223"
  AttacherType = Attacher::AttachEngine3D
  Height = 14
  Length = 19.5
  Placement = pos=(-25,24,-11) rot=(0,0,1;0rad)
  Width = 8
FEATURE [Part::MultiFuse] Fusion051010010012015014088020053
  Shapes = -> [Box112015002017004007004038086003009003045,Box112015002017004007004038086003009003043]
FEATURE [Part::MultiFuse] Fusion051010010012015014088020054
  Shapes = -> [Fusion051010010012015014088020053,Cylinder054099009112]
FEATURE [Part::Box] Box112015002017004007004038086003009003046  label="Cube224"
  AttacherType = Attacher::AttachEngine3D
  Height = 17
  Length = 3
  Placement = pos=(-17,6,-14) rot=(0,0,1;0.785398rad)
  Width = 3
FEATURE [Part::Fillet] Fillet053
  Base = -> Box112015002017004007004038086003009003046
  Edges = 1 edges r=1: [Edge7]
  Placement = pos=(9,15.2,2) rot=(0,0,1;0rad)
FEATURE [Part::Cut] Cut456100  label="cone-cutout-l001"
  Base = -> Fusion051010010012015014088020054
  Tool = -> Fillet053
FEATURE [Part::Cut] Cut456101
  Base = -> Box112015002017004007004038086003009003042
  Tool = -> Cylinder054099009113
FEATURE [Part::Cut] Cut456102
  Base = -> Cone028
  Tool = -> Sphere006006006006030
FEATURE [Part::Cut] Cut456103
  Base = -> Cone028
  Tool = -> Sphere006006006006030
FEATURE [Part::Mirroring] Part__Mirroring005060  label="Cut456103 (Mirror #49)"
  Base = (0,20,0)
  Normal = (0,1,0)
  Source = -> Cut456103
FEATURE [Part::MultiFuse] Fusion051010010012015014088020056  label="ball-clamp-a"
  Shapes = -> [Part__Mirroring005060,Cut456101]
FEATURE [Part::Box] Box112015002017004007004038086003009003047  label="Cube225"
  AttacherType = Attacher::AttachEngine3D
  Height = 10
  Length = 19.5
  Placement = pos=(-26,9,-10) rot=(0,0,1;0rad)
  Width = 5
FEATURE [Part::Cut] Cut456104  label="cone-cutout-r"
  Base = -> Fusion051010010012015014088020054
  Tool = -> Fillet053
FEATURE [Part::MultiFuse] Fusion051010010012015014088020057
  Shapes = -> [Cut456034,Box112015002017004007004038086003009003047]
FEATURE [Part::Cut] Cut456106
  Base = -> Cone028
  Tool = -> Sphere006006006006030
FEATURE [Part::Mirroring] Part__Mirroring005061  label="Cut456106 (Mirror #49)"
  Base = (0,0,0)
  Normal = (0,1,0)
  Source = -> Cut456106
FEATURE [Part::Box] Box112015002017004007004038086003009003048  label="Cube226"
  AttacherType = Attacher::AttachEngine3D
  Height = 10
  Length = 19.5
  Placement = pos=(-26,9,-10) rot=(0,0,1;0rad)
  Width = 5
FEATURE [Part::Mirroring] Part__Mirroring005062  label="Cube226 (Mirror #50)"
  Base = (0,0,0)
  Normal = (0,1,0)
  Source = -> Box112015002017004007004038086003009003048
FEATURE [Part::MultiFuse] Fusion051010010012015014088020058
  Shapes = -> [Fusion051010010012015014088020057,Part__Mirroring005062]
FEATURE [Part::Cut] Cut456107
  Base = -> Fusion051010010012015014088020058
  Tool = -> Cut456104
FEATURE [Part::Mirroring] Part__Mirroring005063  label="cone-cutout-l001 (Mirror #51)"
  Base = (0,0,0)
  Normal = (0,1,0)
  Source = -> Cut456100
FEATURE [Part::Cut] Cut456108
  Base = -> Cut456107
  Tool = -> Part__Mirroring005063
FEATURE [Part::MultiFuse] Fusion051010010012015014088020059
  Shapes = -> [Cut456108,Part__Mirroring005061,Cut456102]
FEATURE [Part::Fillet] Fillet054
  Base = -> Fusion051010010012015014088020059
  Edges = 2 edges r=2: [Edge29,Edge127]
FEATURE [Part::Fillet] Fillet055  label="6142.1-slider-ball-block"
  Base = -> Fillet054
  Edges = 2 edges r=3: [Edge19,Edge75]
FEATURE [Part::Fillet] Fillet056
  Base = -> Fusion051010010012015014088020056
  Edges = 1 edges r=3: [Edge10]
FEATURE [Part::Fillet] Fillet057  label="6143.1-ball-clamp"
  Base = -> Fillet056
  Edges = 1 edges r=2: [Edge15]
FEATURE [Part::Box] Box112015002017004007004038086003009003049  label="Cube227"
  AttacherType = Attacher::AttachEngine3D
  Height = 30
  Length = 5
  Placement = pos=(-11.5,-30,-30) rot=(0,0,1;0rad)
  Width = 60
FEATURE [Part::Sphere] Sphere006006006006031  label="ball-r-32-a-change-radius-here001"
  Angle1 = -90
  Angle2 = 90
  Angle3 = 360
  AttacherType = Attacher::AttachEngine3D
  Placement = pos=(-15,-20,-5) rot=(0,0,1;0rad)
  Radius = 3.2
FEATURE [Part::Mirroring] Part__Mirroring005064  label="ball-r-305 (Mirror #9)001"
  Base = (0,0,0)
  Normal = (0,1,0)
  Placement = pos=(-6,0,-16) rot=(0,0,1;0rad)
  Source = -> Sphere006006006006031
FEATURE [Part::Sphere] Sphere006006006006032  label="ball-r-32-b-change-radius-here002"
  Angle1 = -90
  Angle2 = 90
  Angle3 = 360
  AttacherType = Attacher::AttachEngine3D
  Placement = pos=(-21,-20,-21) rot=(0,0,1;0rad)
  Radius = 3.2
FEATURE [Part::Cylinder] Cylinder054099009115  label="mounting-hole-016"
  Angle = 360
  AttacherType = Attacher::AttachEngine3D
  Height = 100
  Placement = pos=(-40,0,-7) rot=(0,1,0;1.5708rad)
  Radius = 1.7
FEATURE [Part::Cylinder] Cylinder054099009116  label="mounting-hole-017"
  Angle = 360
  AttacherType = Attacher::AttachEngine3D
  Height = 100
  Placement = pos=(-40,-27,-19) rot=(0,1,0;1.5708rad)
  Radius = 1.7
FEATURE [Part::Cone] Cone029  label="csink-009"
  Angle = 360
  AttacherType = Attacher::AttachEngine3D
  Height = 2.5
  Placement = pos=(-9,-27,-19) rot=(0,-1,0;1.5708rad)
  Radius1 = 1.7
  Radius2 = 3
FEATURE [Part::Cylinder] Cylinder054099009117  label="mounting-hole-018"
  Angle = 360
  AttacherType = Attacher::AttachEngine3D
  Height = 100
  Placement = pos=(-40,27,-19) rot=(0,1,0;1.5708rad)
  Radius = 1.7
FEATURE [Part::Cone] Cone030  label="csink-010"
  Angle = 360
  AttacherType = Attacher::AttachEngine3D
  Height = 2.5
  Placement = pos=(-9,27,-19) rot=(0,-1,0;1.5708rad)
  Radius1 = 1.7
  Radius2 = 3
FEATURE [Part::Cone] Cone031  label="csink-011"
  Angle = 360
  AttacherType = Attacher::AttachEngine3D
  Height = 2.5
  Placement = pos=(-9,0,-7) rot=(0,-1,0;1.5708rad)
  Radius1 = 1.7
  Radius2 = 3
FEATURE [Part::Cylinder] Cylinder054099009118  label="wire-clamp-screw-hole-005"
  Angle = 360
  AttacherType = Attacher::AttachEngine3D
  Height = 30
  Placement = pos=(-23.5,-5,-12) rot=(0,1,0;1.5708rad)
  Radius = 2.5
FEATURE [Part::Cylinder] Cylinder054099009119  label="wire-clamp-screw-hole-006"
  Angle = 360
  AttacherType = Attacher::AttachEngine3D
  Height = 30
  Placement = pos=(-23.5,-5,-4) rot=(0,1,0;1.5708rad)
  Radius = 2.5
FEATURE [Part::Cylinder] Cylinder054099009121  label="ball-slider-clamp-hole"
  Angle = 360
  AttacherType = Attacher::AttachEngine3D
  Height = 100
  Placement = pos=(-40,0,-21) rot=(0,1,0;1.5708rad)
  Radius = 1.4
FEATURE [Part::Box] Box112015002017004007004038086003009003057  label="Cube235"
  AttacherType = Attacher::AttachEngine3D
  Height = 2
  Length = 2
  Placement = pos=(-13.5,-15,-28.2) rot=(0,0,1;0rad)
  Width = 30
FEATURE [Part::Box] Box112015002017004007004038086003009003058  label="Cube236"
  AttacherType = Attacher::AttachEngine3D
  Height = 2
  Length = 2
  Placement = pos=(-13.5,-15,-15.8) rot=(0,0,1;0rad)
  Width = 30
FEATURE [Part::Chamfer] Chamfer006012080  label="sliderail-2"
  Base = -> Box112015002017004007004038086003009003058
  Edges = 1 edges r=1: [Edge2]
FEATURE [Part::Chamfer] Chamfer006012081  label="sliderail-1"
  Base = -> Box112015002017004007004038086003009003057
  Edges = 1 edges r=1: [Edge4]
FEATURE [Part::Cylinder] Cylinder054099009123  label="Cylinder054099009213"
  Angle = 360
  AttacherType = Attacher::AttachEngine3D
  Height = 40
  Placement = pos=(-21,20,-21) rot=(1,0,0;1.5708rad)
  Radius = 1.7
FEATURE [Part::Box] Box112015002017004007004038086003009003063  label="Cube241"
  AttacherType = Attacher::AttachEngine3D
  Height = 10
  Length = 14
  Placement = pos=(-25.5,-11,-26) rot=(0,0,1;0rad)
  Width = 20
FEATURE [Part::Box] Box112015002017004007004038086003009003064  label="Cube242"
  AttacherType = Attacher::AttachEngine3D
  Height = 13
  Length = 16
  Placement = pos=(-33,-15,-28) rot=(0,0,1;0rad)
  Width = 20
FEATURE [Part::Cut] Cut456119
  Base = -> Box112015002017004007004038086003009003063
  Tool = -> Box112015002017004007004038086003009003064
FEATURE [Part::Box] Box112015002017004007004038086003009003065  label="Cube243"
  AttacherType = Attacher::AttachEngine3D
  Height = 13
  Length = 16
  Placement = pos=(-25,-15,-22.7) rot=(0,0,1;0rad)
  Width = 20
FEATURE [Part::Cut] Cut456120
  Base = -> Cut456119
  Tool = -> Box112015002017004007004038086003009003065
FEATURE [Part::Box] Box112015002017004007004038086003009003066  label="Cube244"
  AttacherType = Attacher::AttachEngine3D
  Height = 10
  Length = 10
  Placement = pos=(-17.2,-14,-19.5) rot=(0,0,1;0rad)
  Width = 32
FEATURE [Part::Cut] Cut456121
  Base = -> Cut456120
  Tool = -> Box112015002017004007004038086003009003066
FEATURE [Part::Cut] Cut456122
  Base = -> Cut456121
  Tool = -> Cylinder054099009123
FEATURE [Part::Fillet] Fillet060
  Base = -> Cut456122
  Edges = 1 edges r=1.7: [Edge37]
FEATURE [Part::Chamfer] Chamfer006012085  label="ball-slider-1"
  Base = -> Fillet060
  Edges = 2 edges r=2: [Edge9,Edge10]
FEATURE [Part::Cylinder] Cylinder054099009124  label="Cylinder054099009214"
  Angle = 360
  AttacherType = Attacher::AttachEngine3D
  Height = 40
  Placement = pos=(-21,20,-21) rot=(1,0,0;1.5708rad)
  Radius = 1.7
FEATURE [Part::Box] Box112015002017004007004038086003009003067  label="Cube245"
  AttacherType = Attacher::AttachEngine3D
  Height = 10
  Length = 14
  Placement = pos=(-25.5,-11,-26) rot=(0,0,1;0rad)
  Width = 20
FEATURE [Part::Box] Box112015002017004007004038086003009003068  label="Cube246"
  AttacherType = Attacher::AttachEngine3D
  Height = 13
  Length = 16
  Placement = pos=(-33,-15,-28) rot=(0,0,1;0rad)
  Width = 20
FEATURE [Part::Cut] Cut456123
  Base = -> Box112015002017004007004038086003009003067
  Tool = -> Box112015002017004007004038086003009003068
FEATURE [Part::Box] Box112015002017004007004038086003009003069  label="Cube247"
  AttacherType = Attacher::AttachEngine3D
  Height = 13
  Length = 16
  Placement = pos=(-25,-15,-22.7) rot=(0,0,1;0rad)
  Width = 20
FEATURE [Part::Cut] Cut456124
  Base = -> Cut456123
  Tool = -> Box112015002017004007004038086003009003069
FEATURE [Part::Box] Box112015002017004007004038086003009003070  label="Cube248"
  AttacherType = Attacher::AttachEngine3D
  Height = 10
  Length = 10
  Placement = pos=(-17.2,-14,-19.5) rot=(0,0,1;0rad)
  Width = 32
FEATURE [Part::Cut] Cut456125
  Base = -> Cut456124
  Tool = -> Box112015002017004007004038086003009003070
FEATURE [Part::Cut] Cut456126
  Base = -> Cut456125
  Tool = -> Cylinder054099009124
FEATURE [Part::Fillet] Fillet061
  Base = -> Cut456126
  Edges = 1 edges r=1.7: [Edge37]
FEATURE [Part::Chamfer] Chamfer006012086  label="ball-slider-2"
  Base = -> Fillet061
  Edges = 2 edges r=2: [Edge9,Edge10]
  Placement = pos=(0,0,-42) rot=(1,0,0;3.14159rad)
FEATURE [App::DocumentObjectGroup] Group022  label="ball-slider-master"
  Group = -> [Cylinder054099009121,Chamfer006012080,Chamfer006012081,Chamfer006012085,Chamfer006012086]
FEATURE [Part::Cut] Cut456127
  Base = -> Box112015002017004007004038086003009003049
  Tool = -> Cylinder054099009115
FEATURE [Part::Cut] Cut456128
  Base = -> Cut456127
  Tool = -> Cylinder054099009116
FEATURE [Part::Cut] Cut456129
  Base = -> Cut456128
  Tool = -> Cylinder054099009117
FEATURE [Part::Box] Box112015002017004007004038086003009003071  label="Cube249"
  AttacherType = Attacher::AttachEngine3D
  Height = 2
  Length = 2
  Placement = pos=(-13.5,-15,-28.2) rot=(0,0,1;0rad)
  Width = 30
FEATURE [Part::Box] Box112015002017004007004038086003009003072  label="Cube250"
  AttacherType = Attacher::AttachEngine3D
  Height = 2
  Length = 2
  Placement = pos=(-13.5,-15,-15.8) rot=(0,0,1;0rad)
  Width = 30
FEATURE [Part::Chamfer] Chamfer006012087  label="sliderail-003"
  Base = -> Box112015002017004007004038086003009003072
  Edges = 1 edges r=1: [Edge2]
FEATURE [Part::Chamfer] Chamfer006012088  label="sliderail-004"
  Base = -> Box112015002017004007004038086003009003071
  Edges = 1 edges r=1: [Edge4]
FEATURE [Part::Cylinder] Cylinder054099009125  label="ball-slider-clamp-hole001"
  Angle = 360
  AttacherType = Attacher::AttachEngine3D
  Height = 100
  Placement = pos=(-40,0,-21) rot=(0,1,0;1.5708rad)
  Radius = 1.4
FEATURE [Part::Cut] Cut456130
  Base = -> Cut456129
  Tool = -> Cone029
FEATURE [Part::Cut] Cut456131
  Base = -> Cut456130
  Tool = -> Cone031
FEATURE [Part::Cut] Cut456132
  Base = -> Cut456131
  Tool = -> Cone030
FEATURE [Part::MultiFuse] Fusion051010010012015014088020060
  Shapes = -> [Cut456132,Chamfer006012088,Chamfer006012087]
FEATURE [Part::Cut] Cut456133
  Base = -> Fusion051010010012015014088020060
  Tool = -> Cylinder054099009118
FEATURE [Part::Cut] Cut456134
  Base = -> Cut456133
  Tool = -> Cylinder054099009119
FEATURE [Part::Cut] Cut456135  label="slider-ball-mount-old"
  Base = -> Cut456134
  Tool = -> Cylinder054099009125
FEATURE [Part::Cylinder] Cylinder054099009126  label="Cylinder054099009215"
  Angle = 360
  AttacherType = Attacher::AttachEngine3D
  Height = 170
  Radius = 10
FEATURE [Part::Box] Box112015002017004007004038086003009003073  label="Cube251"
  AttacherType = Attacher::AttachEngine3D
  Height = 200
  Length = 10
  Placement = pos=(5,-12,-1) rot=(0,0,1;0rad)
  Width = 24
FEATURE [Part::Feature] Box112015002017004007004038086003009003074
  Placement = pos=(7.8923,10.3301,-1) rot=(0,0,1;2.0944rad)
  shape: bbox 25.78 x 20.66 x 200 mm, 6 faces (baked)
FEATURE [Part::Feature] Box112015002017004007004038086003009003075
  Placement = pos=(-12.8923,1.66987,-1) rot=(0,0,1;4.18879rad)
  shape: bbox 25.78 x 20.66 x 200 mm, 6 faces (baked)
FEATURE [Part::Box] Box112015002017004007004038086003009003076  label="Cube252"
  AttacherType = Attacher::AttachEngine3D
  Height = 200
  Length = 10
  Placement = pos=(-17,-12,-1) rot=(0,0,1;0rad)
  Width = 24
FEATURE [Part::Feature] Box112015002017004007004038086003009003077
  Placement = pos=(18.8923,-8.72243,-1) rot=(0,0,1;2.0944rad)
  shape: bbox 25.78 x 20.66 x 200 mm, 6 faces (baked)
FEATURE [Part::Feature] Box112015002017004007004038086003009003078
  Placement = pos=(-1.8923,20.7224,-1) rot=(0,0,1;4.18879rad)
  shape: bbox 25.78 x 20.66 x 200 mm, 6 faces (baked)
FEATURE [Part::Cut] Cut456136
  Base = -> Cylinder054099009126
  Tool = -> Box112015002017004007004038086003009003073
FEATURE [Part::Cut] Cut456137
  Base = -> Cut456136
  Tool = -> Box112015002017004007004038086003009003078
FEATURE [Part::Cut] Cut456138
  Base = -> Cut456137
  Tool = -> Box112015002017004007004038086003009003077
FEATURE [Part::Cut] Cut456139
  Base = -> Cut456138
  Tool = -> Box112015002017004007004038086003009003076
FEATURE [Part::Cut] Cut456140
  Base = -> Cut456139
  Tool = -> Box112015002017004007004038086003009003075
FEATURE [Part::Cut] Cut456141
  Base = -> Cut456140
  Placement = pos=(0,0,-150) rot=(0,0,1;0rad)
  Tool = -> Box112015002017004007004038086003009003074
FEATURE [Part::Box] Box112015002017004007004038086003009003079  label="Cube253"
  AttacherType = Attacher::AttachEngine3D
  Height = 114
  Length = 19
  Placement = pos=(-10,0,-20) rot=(0,0,1;0rad)
  Width = 10
FEATURE [Part::Box] Box112015002017004007004038086003009003080  label="Cube254"
  AttacherType = Attacher::AttachEngine3D
  Height = 10
  Length = 3.2
  Placement = pos=(-1.6,-12,5) rot=(0,0,1;0rad)
  Width = 20
FEATURE [Part::Box] Box112015002017004007004038086003009003081  label="Cube255"
  AttacherType = Attacher::AttachEngine3D
  Height = 16
  Length = 9
  Placement = pos=(-4,-7,2) rot=(0,0,1;0rad)
  Width = 6
FEATURE [Part::Fillet] Fillet062
  Base = -> Box112015002017004007004038086003009003080
  Edges = 1 edges r=1.5: [Edge2]
FEATURE [Part::Fillet] Fillet063
  Base = -> Fillet062
  Edges = 1 edges r=1.5: [Edge15]
FEATURE [Part::Fillet] Fillet064
  Base = -> Fillet063
  Edges = 1 edges r=1.5: [Edge16]
FEATURE [Part::Fillet] Fillet065
  Base = -> Fillet064
  Edges = 1 edges r=1.5: [Edge16]
FEATURE [Part::Fillet] Fillet066
  Base = -> Box112015002017004007004038086003009003081
  Edges = 1 edges r=2: [Edge4]
FEATURE [Part::Fillet] Fillet067
  Base = -> Fillet066
  Edges = 1 edges r=2: [Edge3]
FEATURE [Part::Cylinder] Cylinder054099009127  label="Cylinder054099009216"
  Angle = 360
  AttacherType = Attacher::AttachEngine3D
  Height = 15
  Placement = pos=(0,1,-10) rot=(1,0,0;1.5708rad)
  Radius = 1.2
FEATURE [Part::Cylinder] Cylinder054099009128  label="Cylinder054099009217"
  Angle = 360
  AttacherType = Attacher::AttachEngine3D
  Height = 38
  Placement = pos=(3,1.8,-19) rot=(0,0,1;0rad)
  Radius = 2
FEATURE [Part::Cylinder] Cylinder054099009129  label="Cylinder054099009218"
  Angle = 360
  AttacherType = Attacher::AttachEngine3D
  Height = 38
  Placement = pos=(-4,1.8,-19) rot=(0,0,1;0rad)
  Radius = 2
FEATURE [Part::Cone] Cone032  label="Cone021"
  Angle = 360
  AttacherType = Attacher::AttachEngine3D
  Height = 6
  Placement = pos=(-2,0,0) rot=(0,-1,0;1.5708rad)
  Radius1 = 0
  Radius2 = 2
FEATURE [Part::Cylinder] Cylinder054099009130  label="Cylinder054099009219"
  Angle = 360
  AttacherType = Attacher::AttachEngine3D
  Height = 7
  Placement = pos=(-4,1.8,0) rot=(0,1,0;1.5708rad)
  Radius = 2
FEATURE [Part::MultiFuse] Fusion051010010012015014088020061  label="glue-chans-screw-hole"
  Shapes = -> [Fillet065,Cylinder054099009127,Cylinder054099009128,Cylinder054099009129,Cone032,Cylinder054099009130]
FEATURE [Part::Cut] Cut456142
  Base = -> Cut456141
  Tool = -> Box112015002017004007004038086003009003079
FEATURE [Part::MultiFuse] Fusion051010010012015014088020062  label="arm-blank-a"
  Shapes = -> [Cut456142,Fillet067]
FEATURE [Part::Cut] Cut456143  label="arm-blank"
  Base = -> Fusion051010010012015014088020062
  Tool = -> Fusion051010010012015014088020061
FEATURE [Part::Box] Box112015002017004007004038086003009003082  label="Cube256"
  AttacherType = Attacher::AttachEngine3D
  Height = 97
  Length = 30
  Placement = pos=(-17,-14,-157) rot=(0,0,1;0rad)
  Width = 30
FEATURE [Part::Box] Box112015002017004007004038086003009003083  label="Cube257"
  AttacherType = Attacher::AttachEngine3D
  Height = 22
  Length = 10
  Width = 4
FEATURE [Part::Cylinder] Cylinder054099009131  label="Cylinder054099009220"
  Angle = 360
  AttacherType = Attacher::AttachEngine3D
  Height = 14
  Placement = pos=(0,6.25,-75) rot=(1,0,0;1.5708rad)
  Radius = 2.25
FEATURE [Part::Fillet] Fillet068
  Base = -> Box112015002017004007004038086003009003083
  Edges = 1 edges r=4.9: [Edge4]
FEATURE [Part::Fillet] Fillet069
  Base = -> Fillet068
  Edges = 1 edges r=4.9: [Edge15]
  Placement = pos=(-5,1.25,-80) rot=(0,0,1;0rad)
FEATURE [Part::Cylinder] Cylinder054099009132  label="Cylinder054099009221"
  Angle = 360
  AttacherType = Attacher::AttachEngine3D
  Height = 10
  Placement = pos=(0,0.25,-67) rot=(1,0,0;1.5708rad)
  Radius = 1.7
FEATURE [Part::Cut] Cut456144
  Base = -> Cut456143
  Tool = -> Box112015002017004007004038086003009003082
FEATURE [Part::Box] Box112015002017004007004038086003009003084  label="Cube258"
  AttacherType = Attacher::AttachEngine3D
  Height = 19
  Length = 10
  Width = 4
FEATURE [Part::Fillet] Fillet070
  Base = -> Box112015002017004007004038086003009003084
  Edges = 1 edges r=4.9: [Edge4]
FEATURE [Part::Fillet] Fillet071
  Base = -> Fillet070
  Edges = 1 edges r=4.9: [Edge15]
  Placement = pos=(-5,1.25,-80) rot=(0,0,1;0rad)
FEATURE [Part::Mirroring] Part__Mirroring005065  label="Fillet071 (Mirror #53)"
  Base = (0,0,0)
  Normal = (0,1,0)
  Source = -> Fillet071
FEATURE [Part::Cylinder] Cylinder054099009133  label="Cylinder054099009222"
  Angle = 360
  AttacherType = Attacher::AttachEngine3D
  Height = 10
  Placement = pos=(-5,0.75,-63) rot=(0.57735,0.57735,0.57735;2.0944rad)
  Radius = 2
FEATURE [Part::MultiFuse] Fusion051010010012015014088020063
  Shapes = -> [Fillet069,Cylinder054099009133]
FEATURE [Part::Fillet] Fillet072
  Base = -> Fusion051010010012015014088020063
  Edges = 1 edges r=2: [Edge22]
FEATURE [Part::Fillet] Fillet073
  Base = -> Fillet072
  Edges = 1 edges r=2: [Edge25]
FEATURE [Part::Cylinder] Cylinder054099009134  label="Cylinder054099009223"
  Angle = 360
  AttacherType = Attacher::AttachEngine3D
  Height = 10
  Placement = pos=(0,10.25,-67) rot=(1,0,0;1.5708rad)
  Radius = 1.4
FEATURE [Part::Cylinder] Cylinder054099009135  label="Cylinder054099009224"
  Angle = 360
  AttacherType = Attacher::AttachEngine3D
  Height = 14
  Placement = pos=(0,6.25,-75) rot=(1,0,0;1.5708rad)
  Radius = 2.5
FEATURE [Part::Cut] Cut456145
  Base = -> Fillet073
  Tool = -> Cylinder054099009135
FEATURE [Part::Cut] Cut456146
  Base = -> Cut456145
  Tool = -> Cylinder054099009134
FEATURE [Part::Cut] Cut456147
  Base = -> Part__Mirroring005065
  Tool = -> Cylinder054099009132
FEATURE [Part::Cut] Cut456148
  Base = -> Cut456147
  Tool = -> Cylinder054099009131
FEATURE [Part::Chamfer] Chamfer006012089  label="angled-half-arm-ball-clamp"
  Base = -> Cut456148
  Edges = 1 edges r=2: [Edge23]
  Placement = pos=(-30,50,0) rot=(0,0,1;0rad)
FEATURE [Part::MultiFuse] Fusion051010010012015014088020064  label="6153.2-angled-half-arm"
  Placement = pos=(-30,50,0) rot=(0,0,1;0rad)
  Shapes = -> [Cut456144,Cut456146]
FEATURE [App::DocumentObjectGroup] Group008  label="6152 Angle Arms"
  Group = -> [Chamfer006012089,Fusion051010010012015014088020064]
FEATURE [Part::Feature] Part__Feature165  label="hot-end-from-step"
  Placement = pos=(0,0,-130) rot=(0,0,1;1.5708rad)
  shape: bbox 57.85 x 65.4 x 25.8 mm, 468 faces (baked)
FEATURE [Part::Cylinder] Cylinder054099009136  label="Cylinder054099009225"
  Angle = 360
  AttacherType = Attacher::AttachEngine3D
  Height = 54
  Placement = pos=(0,0,-149) rot=(0,0,-1;0.523599rad)
  Radius = 8.8
FEATURE [Part::Cylinder] Cylinder054099009137  label="Cylinder054099009226"
  Angle = 360
  AttacherType = Attacher::AttachEngine3D
  Height = 54
  Placement = pos=(-20,11.5,-131) rot=(0,0,-1;0.523599rad)
  Radius = 1.7
FEATURE [Part::Feature] Cylinder054099009137001
  Placement = pos=(0,-23,-131) rot=(0,0,1;1.5708rad)
  shape: bbox 3.4 x 3.4 x 24 mm, 3 faces (baked)
FEATURE [Part::Feature] Cylinder054099009137002
  Placement = pos=(20,11.5,-131) rot=(0,0,1;3.66519rad)
  shape: bbox 3.4 x 3.4 x 24 mm, 3 faces (baked)
FEATURE [Part::Cylinder] Cylinder054099009137003
  Angle = 360
  AttacherType = Attacher::AttachEngine3D
  Height = 24
  Placement = pos=(-2.9,-11.7,-131) rot=(0,0,-1;0.523599rad)
  Radius = 1.7
FEATURE [Part::Cylinder] Cylinder054099009137004
  Angle = 360
  AttacherType = Attacher::AttachEngine3D
  Height = 24
  Placement = pos=(11.55,3.3,-131) rot=(0,0,-1;0.523599rad)
  Radius = 1.7
FEATURE [Part::Box] Box112015002017004007004038086003009003085  label="Cube259"
  AttacherType = Attacher::AttachEngine3D
  Height = 13
  Length = 18.5
  Placement = pos=(8.5,4,-127) rot=(0,0,1;0rad)
  Width = 12.5
FEATURE [Part::Box] Box112015002017004007004038086003009003087  label="Cube261"
  AttacherType = Attacher::AttachEngine3D
  Height = 14
  Length = 63
  Placement = pos=(-34.7,2.7,-116) rot=(0,0,1;0rad)
  Width = 15
FEATURE [Part::Cylinder] Cylinder054099009137005
  Angle = 360
  AttacherType = Attacher::AttachEngine3D
  Height = 20
  Placement = pos=(-19.2,8,-108.7) rot=(1,0,0;1.5708rad)
  Radius = 1.4
FEATURE [Part::Cylinder] Cylinder054099009137006
  Angle = 360
  AttacherType = Attacher::AttachEngine3D
  Height = 20
  Placement = pos=(-19.2,26,-108.7) rot=(1,0,0;1.5708rad)
  Radius = 1.7
FEATURE [Part::Cylinder] Cylinder054099009137007
  Angle = 360
  AttacherType = Attacher::AttachEngine3D
  Height = 8
  Placement = pos=(0,0,1) rot=(0,0,1;0rad)
  Radius = 5
FEATURE [Part::Box] Box112015002017004007004038086003009003088  label="Cube262"
  AttacherType = Attacher::AttachEngine3D
  Height = 10
  Length = 10
  Placement = pos=(-5,2.85,0) rot=(0,0,1;0rad)
  Width = 10
FEATURE [Part::Feature] Box112015002017004007004038086003009003088001
  Placement = pos=(-4.96817,-2.90513,0) rot=(0,0,1;1.0472rad)
  shape: bbox 13.66 x 13.66 x 10 mm, 6 faces (baked)
FEATURE [Part::Feature] Box112015002017004007004038086003009003088002
  Placement = pos=(0.0318276,-5.75513,0) rot=(0,0,1;2.0944rad)
  shape: bbox 13.66 x 13.66 x 10 mm, 6 faces (baked)
FEATURE [Part::Feature] Box112015002017004007004038086003009003088003
  Placement = pos=(5,-2.85,0) rot=(0,0,1;3.14159rad)
  shape: bbox 10 x 10 x 10 mm, 6 faces (baked)
FEATURE [Part::Feature] Box112015002017004007004038086003009003088004
  Placement = pos=(4.96817,2.90513,0) rot=(0,0,1;4.18879rad)
  shape: bbox 13.66 x 13.66 x 10 mm, 6 faces (baked)
FEATURE [Part::Feature] Box112015002017004007004038086003009003088005
  Placement = pos=(-0.0318276,5.75513,0) rot=(0,0,-1;1.0472rad)
  shape: bbox 13.66 x 13.66 x 10 mm, 6 faces (baked)
FEATURE [Part::Cut] Cut456149
  Base = -> Cylinder054099009137007
  Tool = -> Box112015002017004007004038086003009003088
FEATURE [Part::Cut] Cut456150
  Base = -> Cut456149
  Tool = -> Box112015002017004007004038086003009003088005
FEATURE [Part::Cut] Cut456151
  Base = -> Cut456150
  Tool = -> Box112015002017004007004038086003009003088004
FEATURE [Part::Cut] Cut456152
  Base = -> Cut456151
  Tool = -> Box112015002017004007004038086003009003088003
FEATURE [Part::Cut] Cut456153
  Base = -> Cut456152
  Tool = -> Box112015002017004007004038086003009003088002
FEATURE [Part::Cut] Cut456154
  Base = -> Cut456153
  Placement = pos=(-2.9,-11.7,-136) rot=(0,0,-1;0.523599rad)
  Tool = -> Box112015002017004007004038086003009003088001
FEATURE [Part::Cut] Cut456155
  Base = -> Cut456153
  Placement = pos=(11.55,3.3,-136) rot=(0,0,-1;0.785398rad)
  Tool = -> Box112015002017004007004038086003009003088001
FEATURE [Sketcher::SketchObject] Sketch
  MapMode = 5
  sketch-geometry (28):
    g0: LineSegment StartX=11.005 StartY=16.347 StartZ=0 EndX=7.4963 EndY=16.347 EndZ=0
    g1: LineSegment StartX=7.4963 StartY=16.347 StartZ=0 EndX=4.64255 EndY=15.5049 EndZ=0
    g2: LineSegment StartX=4.64255 StartY=15.5049 StartZ=0 EndX=2.5841 EndY=14.2418 EndZ=0
    g3: LineSegment StartX=2.5841 StartY=14.2418 StartZ=0 EndX=1.18061 EndY=12.8383 EndZ=0
    g4: LineSegment StartX=1.18061 StartY=12.8383 StartZ=0 EndX=-3.96551 EndY=7.9261 EndZ=0
    g5: LineSegment StartX=-3.96551 StartY=7.9261 StartZ=0 EndX=-10.7023 EndY=2.59285 EndZ=0
    g6: LineSegment StartX=-10.7023 StartY=2.59285 StartZ=0 EndX=-19.2635 EndY=-2.45971 EndZ=0
    g7: LineSegment StartX=-19.2635 StartY=-2.45971 StartZ=0 EndX=-11.825 EndY=-15.5589 EndZ=0
    g8: LineSegment StartX=-11.825 StartY=-15.5589 StartZ=0 EndX=-8.69059 EndY=-13.7344 EndZ=0
    g9: LineSegment StartX=-8.69059 StartY=-13.7344 StartZ=0 EndX=-7.14675 EndY=-12.4245 EndZ=0
    g10: LineSegment StartX=-7.14675 StartY=-12.4245 StartZ=0 EndX=-6.16431 EndY=-11.2081 EndZ=0
    g11: LineSegment StartX=-6.16431 StartY=-11.2081 StartZ=0 EndX=-5.32222 EndY=-9.52393 EndZ=0
    g12: LineSegment StartX=-5.32222 StartY=-9.52393 StartZ=0 EndX=-4.24621 EndY=-8.72862 EndZ=0
    g13: LineSegment StartX=-4.24621 StartY=-8.72862 StartZ=0 EndX=-2.93629 EndY=-8.44792 EndZ=0
    g14: LineSegment StartX=-2.93629 StartY=-8.44792 StartZ=0 EndX=-1.8135 EndY=-8.58827 EndZ=0
    g15: LineSegment StartX=-1.8135 StartY=-8.58827 StartZ=0 EndX=-0.26966 EndY=-8.91575 EndZ=0
    g16: LineSegment StartX=-0.26966 StartY=-8.91575 StartZ=0 EndX=2.25662 EndY=-9.99176 EndZ=0
    g17: LineSegment StartX=2.25662 StartY=-9.99176 StartZ=0 EndX=3.23906 EndY=-10.5064 EndZ=0
    g18: LineSegment StartX=3.23906 StartY=-10.5064 StartZ=0 EndX=11.66 EndY=-15.5121 EndZ=0
    g19: LineSegment StartX=11.66 StartY=-15.5121 StartZ=0 EndX=19.3324 EndY=-2.36614 EndZ=0
    g20: LineSegment StartX=19.3324 StartY=-2.36614 StartZ=0 EndX=14.9816 EndY=0 EndZ=0
    g21: LineSegment StartX=14.9816 StartY=0 StartZ=0 EndX=13.5313 EndY=0 EndZ=0
    g22: LineSegment StartX=13.5313 StartY=0 StartZ=0 EndX=10.9115 EndY=0 EndZ=0
    g23: LineSegment StartX=10.9115 StartY=0 StartZ=0 EndX=8.80622 EndY=1.23614 EndZ=0
    g24: LineSegment StartX=8.80622 StartY=1.23614 StartZ=0 EndX=8.29161 EndY=2.87354 EndZ=0
    g25: LineSegment StartX=8.29161 StartY=2.87354 StartZ=0 EndX=8.3384 EndY=3.8092 EndZ=0
    g26: LineSegment StartX=8.3384 StartY=3.8092 StartZ=0 EndX=11.66 EndY=3.8092 EndZ=0
    g27: LineSegment StartX=11.66 StartY=3.8092 StartZ=0 EndX=11.005 EndY=16.347 EndZ=0
  constraints (33):
    c: Horizontal(g0)
    c: Coincident(g0,g1)
    c: Coincident(g1,g2)
    c: Coincident(g2,g3)
    c: Coincident(g3,g4)
    c: Coincident(g4,g5)
    c: Coincident(g5,g6)
    c: Coincident(g6,g7)
    c: Coincident(g7,g8)
    c: Coincident(g8,g9)
    c: Coincident(g9,g10)
    c: Coincident(g10,g11)
    c: Coincident(g11,g12)
    c: Coincident(g12,g13)
    c: Coincident(g13,g14)
    c: Coincident(g14,g15)
    c: Coincident(g15,g16)
    c: Coincident(g16,g17)
    c: Coincident(g17,g18)
    c: Coincident(g18,g19)
    c: Coincident(g19,g20)
    c: PointOnObject(g20,g-1)
    c: Coincident(g20,g21)
    c: PointOnObject(g21,g-1)
    c: Coincident(g21,g22)
    c: PointOnObject(g22,g-1)
    c: Coincident(g22,g23)
    c: Coincident(g23,g24)
    c: Coincident(g24,g25)
    c: Coincident(g25,g26)
    c: Horizontal(g26)
    c: Coincident(g26,g27)
    c: Coincident(g27,g0)
FEATURE [Part::Extrusion] Extrude
  Base = -> Sketch
  Dir = (0,0,20)
  DirMode = 0
  FaceMakerClass = Part::FaceMakerExtrusion
  LengthFwd = 0
  LengthRev = 0
  Placement = pos=(0,0,-131) rot=(0,0,1;0rad)
  Solid = true
  Symmetric = false
FEATURE [Part::Box] Box112015002017004007004038086003009003088006  label="Cube263"
  AttacherType = Attacher::AttachEngine3D
  Height = 33
  Length = 18.5
  Placement = pos=(8.5,3,-138) rot=(0,0,1;0rad)
  Width = 20.5
FEATURE [Part::Cut] Cut456156
  Base = -> Extrude
  Placement = pos=(0,0,-8) rot=(0,0,1;0rad)
  Tool = -> Box112015002017004007004038086003009003088006
FEATURE [Part::Fillet] Fillet074
  Base = -> Cut456156
  Edges = 26 edges r=2: [Edge3,Edge33,Edge34,Edge35,Edge36,Edge37,Edge38,Edge39,Edge40,Edge41,Edge42,Edge43,Edge44,Edge45,Edge46,Edge47,Edge48,Edge49,Edge50,Edge51,Edge52,Edge53,Edge54,Edge55,Edge56,Edge57]
FEATURE [Part::Cylinder] Cylinder054099009137008  label="Cylinder054099009137093"
  Angle = 360
  AttacherType = Attacher::AttachEngine3D
  Height = 14
  Placement = pos=(0,0,-130) rot=(0,0,-1;0.523599rad)
  Radius = 35
FEATURE [Part::Box] Box112015002017004007004038086003009003088007  label="Cube264"
  AttacherType = Attacher::AttachEngine3D
  Height = 4
  Length = 29.5
  Placement = pos=(0,0,-117) rot=(0,0,1;0rad)
  Width = 19
FEATURE [Part::Box] Box112015002017004007004038086003009003088008  label="Cube265"
  AttacherType = Attacher::AttachEngine3D
  Height = 13
  Length = 20
  Placement = pos=(-26,-5,-117) rot=(0,0,1;0rad)
  Width = 26
FEATURE [Part::MultiFuse] Fusion051010010012015014088020065
  Shapes = -> [Cylinder054099009137008,Box112015002017004007004038086003009003088007,Box112015002017004007004038086003009003088008]
FEATURE [Part::Cut] Cut456157
  Base = -> Fusion051010010012015014088020065
  Tool = -> Box112015002017004007004038086003009003087
FEATURE [Part::MultiFuse] Fusion051010010012015014088020066
  Shapes = -> [Fillet074,Box112015002017004007004038086003009003085]
FEATURE [Part::Cut] Cut456158
  Base = -> Cut456157
  Tool = -> Fusion051010010012015014088020066
FEATURE [Part::MultiFuse] Fusion051010010012015014088020067
  Shapes = -> [Cylinder054099009137,Cylinder054099009137001,Cylinder054099009137002,Cylinder054099009137003,Cylinder054099009137004,Cut456154,Cut456155]
FEATURE [Part::Cut] Cut456159
  Base = -> Cut456158
  Tool = -> Fusion051010010012015014088020067
FEATURE [Part::MultiFuse] Fusion051010010012015014088020068
  Shapes = -> [Cylinder054099009137005,Cylinder054099009137006]
FEATURE [Part::Cut] Cut456160
  Base = -> Cut456159
  Tool = -> Fusion051010010012015014088020068
FEATURE [Part::Cut] Cut456161
  Base = -> Cut456160
  Tool = -> Cylinder054099009136
FEATURE [Part::Chamfer] Chamfer006012090
  Base = -> Cut456161
  Edges = 1 edges r=9: [Edge3]
FEATURE [Part::Chamfer] Chamfer006012091
  Base = -> Chamfer006012090
  Edges = 1 edges r=9: [Edge321]
FEATURE [Part::Fillet] Fillet075
  Base = -> Chamfer006012091
  Edges = 1 edges r=4: [Edge18]
FEATURE [Part::Fillet] Fillet076
  Base = -> Fillet075
  Edges = 1 edges r=4: [Edge227]
  Placement = pos=(0,0,0) rot=(0,0,-1;0.523599rad)
FEATURE [Part::Cylinder] Cylinder054099009137009  label="ball-slider-clamp-hole002"
  Angle = 360
  AttacherType = Attacher::AttachEngine3D
  Height = 30
  Placement = pos=(-47,0,-123) rot=(0,1,0;1.5708rad)
  Radius = 1.4
FEATURE [Part::Box] Box112015002017004007004038086003009003088009  label="Cube266"
  AttacherType = Attacher::AttachEngine3D
  Height = 2
  Length = 2
  Placement = pos=(-24,-15,-130) rot=(0,0,1;0rad)
  Width = 30
FEATURE [Part::Box] Box112015002017004007004038086003009003088010  label="Cube267"
  AttacherType = Attacher::AttachEngine3D
  Height = 2
  Length = 2
  Placement = pos=(-24,-15,-118) rot=(0,0,1;0rad)
  Width = 30
FEATURE [Part::Cylinder] Cylinder054099009137010  label="Cylinder054099009137094"
  Angle = 360
  AttacherType = Attacher::AttachEngine3D
  Height = 40
  Placement = pos=(-21,20,-21) rot=(1,0,0;1.5708rad)
  Radius = 1.7
FEATURE [Part::Box] Box112015002017004007004038086003009003088011  label="Cube268"
  AttacherType = Attacher::AttachEngine3D
  Height = 10
  Length = 14
  Placement = pos=(-25.5,-11,-26) rot=(0,0,1;0rad)
  Width = 20
FEATURE [Part::Box] Box112015002017004007004038086003009003088012  label="Cube269"
  AttacherType = Attacher::AttachEngine3D
  Height = 13
  Length = 16
  Placement = pos=(-33,-15,-28) rot=(0,0,1;0rad)
  Width = 20
FEATURE [Part::Cut] Cut456162
  Base = -> Box112015002017004007004038086003009003088011
  Tool = -> Box112015002017004007004038086003009003088012
FEATURE [Part::Box] Box112015002017004007004038086003009003088013  label="Cube270"
  AttacherType = Attacher::AttachEngine3D
  Height = 13
  Length = 16
  Placement = pos=(-25,-15,-22.7) rot=(0,0,1;0rad)
  Width = 20
FEATURE [Part::Cut] Cut456163
  Base = -> Cut456162
  Tool = -> Box112015002017004007004038086003009003088013
FEATURE [Part::Box] Box112015002017004007004038086003009003088014  label="Cube271"
  AttacherType = Attacher::AttachEngine3D
  Height = 10
  Length = 10
  Placement = pos=(-17.2,-14,-19.5) rot=(0,0,1;0rad)
  Width = 32
FEATURE [Part::Cut] Cut456164
  Base = -> Cut456163
  Tool = -> Box112015002017004007004038086003009003088014
FEATURE [Part::Cut] Cut456165
  Base = -> Cut456164
  Tool = -> Cylinder054099009137010
FEATURE [Part::Fillet] Fillet077
  Base = -> Cut456165
  Edges = 1 edges r=1.7: [Edge37]
FEATURE [Part::Chamfer] Chamfer006012094  label="ball-slider-003"
  Base = -> Fillet077
  Edges = 2 edges r=2: [Edge9,Edge10]
  Placement = pos=(-123,14.5,-172) rot=(0,0,-1;1.5708rad)
FEATURE [Part::Cylinder] Cylinder054099009137011  label="Cylinder054099009137095"
  Angle = 360
  AttacherType = Attacher::AttachEngine3D
  Height = 40
  Placement = pos=(-21,20,-21) rot=(1,0,0;1.5708rad)
  Radius = 1.7
FEATURE [Part::Box] Box112015002017004007004038086003009003088015  label="Cube272"
  AttacherType = Attacher::AttachEngine3D
  Height = 10
  Length = 14
  Placement = pos=(-25.5,-11,-26) rot=(0,0,1;0rad)
  Width = 20
FEATURE [Part::Box] Box112015002017004007004038086003009003088016  label="Cube273"
  AttacherType = Attacher::AttachEngine3D
  Height = 13
  Length = 16
  Placement = pos=(-33,-15,-28) rot=(0,0,1;0rad)
  Width = 20
FEATURE [Part::Cut] Cut456166
  Base = -> Box112015002017004007004038086003009003088015
  Tool = -> Box112015002017004007004038086003009003088016
FEATURE [Part::Box] Box112015002017004007004038086003009003088017  label="Cube274"
  AttacherType = Attacher::AttachEngine3D
  Height = 13
  Length = 16
  Placement = pos=(-25,-15,-22.7) rot=(0,0,1;0rad)
  Width = 20
FEATURE [Part::Cut] Cut456167
  Base = -> Cut456166
  Tool = -> Box112015002017004007004038086003009003088017
FEATURE [Part::Box] Box112015002017004007004038086003009003088018  label="Cube275"
  AttacherType = Attacher::AttachEngine3D
  Height = 10
  Length = 10
  Placement = pos=(-17.2,-14,-19.5) rot=(0,0,1;0rad)
  Width = 32
FEATURE [Part::Cut] Cut456168
  Base = -> Cut456167
  Tool = -> Box112015002017004007004038086003009003088018
FEATURE [Part::Cut] Cut456169
  Base = -> Cut456168
  Tool = -> Cylinder054099009137011
FEATURE [Part::Fillet] Fillet078
  Base = -> Cut456169
  Edges = 1 edges r=1.7: [Edge37]
FEATURE [Part::Chamfer] Chamfer006012095  label="ball-slider-004"
  Base = -> Fillet078
  Edges = 2 edges r=2: [Edge9,Edge10]
  Placement = pos=(-123,14.5,-214) rot=(0.707107,-0.707107,0;3.14159rad)
FEATURE [Part::Box] Box112015002017004007004038086003009003088019  label="Cube276"
  AttacherType = Attacher::AttachEngine3D
  Height = 50
  Length = 80
  Placement = pos=(-102,-40,-140) rot=(0,0,1;0rad)
  Width = 80
FEATURE [Part::Feature] Box112015002017004007004038086003009003088019001
  Placement = pos=(85.641,-68.3346,-140) rot=(0,0,1;2.0944rad)
  shape: bbox 109.3 x 109.3 x 50 mm, 6 faces (baked)
FEATURE [Part::Feature] Box112015002017004007004038086003009003088019002
  Placement = pos=(16.359,108.335,-140) rot=(0,0,1;4.18879rad)
  shape: bbox 109.3 x 109.3 x 50 mm, 6 faces (baked)
FEATURE [Part::Cut] Cut456170
  Base = -> Fillet076
  Tool = -> Box112015002017004007004038086003009003088019
FEATURE [Part::Cut] Cut456171
  Base = -> Cut456170
  Tool = -> Box112015002017004007004038086003009003088019002
FEATURE [Part::Cut] Cut456172  label="new-blank-1"
  Base = -> Cut456171
  Tool = -> Box112015002017004007004038086003009003088019001
FEATURE [Part::Cylinder] Cylinder054099009137013  label="Cylinder054099009137096"
  Angle = 360
  AttacherType = Attacher::AttachEngine3D
  Height = 17
  Placement = pos=(-60,-22,-315) rot=(0,0,1;0rad)
  Radius = 1.7
FEATURE [Part::Cylinder] Cylinder054099009137014  label="Cylinder054099009137097"
  Angle = 360
  AttacherType = Attacher::AttachEngine3D
  Height = 17
  Placement = pos=(-56,-22,-315) rot=(0,0,1;0rad)
  Radius = 1.7
FEATURE [Part::Box] Box112015002017004007004038086003009003088019003  label="Cube277"
  AttacherType = Attacher::AttachEngine3D
  Height = 10
  Length = 4
  Placement = pos=(-60,-23.7,-310) rot=(0,0,1;0rad)
  Width = 3.4
FEATURE [Part::MultiFuse] Fusion051010010012015014088020069  label="pcb-brac-screw-slot-b002"
  Placement = pos=(-96,-320,-275) rot=(1,0,0;1.5708rad)
  Shapes = -> [Box112015002017004007004038086003009003088019003,Cylinder054099009137014,Cylinder054099009137013]
FEATURE [Part::Box] Box112015002017004007004038086003009003088019004  label="Cube278"
  AttacherType = Attacher::AttachEngine3D
  Height = 28
  Length = 15
  Placement = pos=(-156,-36,-325) rot=(0,0,1;0rad)
  Width = 15
FEATURE [Part::Box] Box112015002017004007004038086003009003088019005  label="Cube279"
  AttacherType = Attacher::AttachEngine3D
  Height = 20
  Length = 15
  Placement = pos=(-160,-30,-320) rot=(0,0,1;0rad)
  Width = 15
FEATURE [Part::MultiFuse] Fusion051010010012015014088020070
  Shapes = -> [Box112015002017004007004038086003009003088019004,Box112015002017004007004038086003009003088019005]
FEATURE [Part::Chamfer] Chamfer006012096
  Base = -> Fusion051010010012015014088020070
  Edges = 1 edges r=3: [Edge16]
FEATURE [Part::Cut] Cut456173
  Base = -> Chamfer006012058
  Tool = -> Chamfer006012096
FEATURE [Part::Chamfer] Chamfer006012097
  Base = -> Cut456173
  Edges = 1 edges r=0.6: [Edge52]
FEATURE [Part::Box] Box112015002017004007004038086003009003088019006  label="Cube280"
  AttacherType = Attacher::AttachEngine3D
  Height = 15
  Length = 26
  Placement = pos=(-173,-18,-307) rot=(0,0,1;0rad)
  Width = 6
FEATURE [Part::Box] Box112015002017004007004038086003009003088019007  label="Cube281"
  AttacherType = Attacher::AttachEngine3D
  Height = 15
  Length = 26
  Placement = pos=(-160,-20,-317) rot=(0,0,1;0rad)
  Width = 9
FEATURE [Part::Cut] Cut456174
  Base = -> Box112015002017004007004038086003009003088019006
  Tool = -> Box112015002017004007004038086003009003088019007
FEATURE [Part::Box] Box112015002017004007004038086003009003088019008  label="Cube282"
  AttacherType = Attacher::AttachEngine3D
  Height = 5
  Length = 13
  Placement = pos=(-173,-20,-307) rot=(0,0,1;0rad)
  Width = 6
FEATURE [Part::Box] Box112015002017004007004038086003009003088019009  label="Cube283"
  AttacherType = Attacher::AttachEngine3D
  Height = 7
  Length = 14
  Placement = pos=(-173.1,-20.1,-308) rot=(0,0,1;0rad)
  Width = 6
FEATURE [Part::MultiFuse] Fusion051010010012015014088020071
  Shapes = -> [Cut456174,Box112015002017004007004038086003009003088019008]
FEATURE [Part::Cut] Cut456175  label="pcb-bracket-filament-1-a"
  Base = -> Chamfer006012097
  Tool = -> Box112015002017004007004038086003009003088019009
FEATURE [Part::Cut] Cut456176
  Base = -> Fusion051010010012015014088020071
  Tool = -> Fusion051010010012015014088020069
FEATURE [Part::Chamfer] Chamfer006012098  label="pcb-bracket-filament-2-a"
  Base = -> Cut456176
  Edges = 5 edges r=2.5: [Edge43,Edge45,Edge46,Edge49,Edge50]
FEATURE [Part::Cylinder] Cylinder054099009137015  label="Cylinder054099009137098"
  Angle = 360
  AttacherType = Attacher::AttachEngine3D
  Height = 20
  Placement = pos=(-170,-10,-304.5) rot=(1,0,0;1.5708rad)
  Radius = 1
FEATURE [Part::Cylinder] Cylinder054099009137016  label="Cylinder054099009137058"
  Angle = 360
  AttacherType = Attacher::AttachEngine3D
  Height = 20
  Placement = pos=(-163,-10,-304.5) rot=(1,0,0;1.5708rad)
  Radius = 1
FEATURE [Part::Cylinder] Cylinder054099009137017  label="Cylinder054099009137059"
  Angle = 360
  AttacherType = Attacher::AttachEngine3D
  Height = 20
  Placement = pos=(-170,-10,-304.5) rot=(1,0,0;1.5708rad)
  Radius = 1.4
FEATURE [Part::Cylinder] Cylinder054099009137018  label="Cylinder054099009137099"
  Angle = 360
  AttacherType = Attacher::AttachEngine3D
  Height = 20
  Placement = pos=(-163,-10,-304.5) rot=(1,0,0;1.5708rad)
  Radius = 1.4
FEATURE [Part::Cut] Cut456177
  Base = -> Cut456175
  Tool = -> Cylinder054099009137015
FEATURE [Part::Cut] Cut456178  label="pcb-bracket-filament-1"
  Base = -> Cut456177
  Placement = pos=(50,0,0) rot=(0,0,1;0rad)
  Tool = -> Cylinder054099009137016
FEATURE [Part::Cut] Cut456179
  Base = -> Chamfer006012098
  Tool = -> Cylinder054099009137017
FEATURE [Part::Cut] Cut456180  label="pcb-bracket-filament-2"
  Base = -> Cut456179
  Placement = pos=(50,0,0) rot=(0,0,1;0rad)
  Tool = -> Cylinder054099009137018
FEATURE [Part::Box] Box112015002017004007004038086003009003088019010  label="Cube284"
  AttacherType = Attacher::AttachEngine3D
  Height = 10.4
  Length = 10
  Placement = pos=(-30,-15,-128.2) rot=(0,0,1;0rad)
  Width = 30
FEATURE [Part::Cylinder] Cylinder054099009137020  label="Cylinder054099009137100"
  Angle = 360
  AttacherType = Attacher::AttachEngine3D
  Height = 10
  Placement = pos=(0,0,0.2) rot=(0,0,1;0rad)
  Radius = 30
FEATURE [Part::Feature] Face019
  shape: bbox 56.54 x 56.62 x 2e-07 mm, 1 faces, 0 solids (baked)
FEATURE [Part::Feature] Face020
  shape: bbox 18.01 x 18.01 x 2e-07 mm, 1 faces, 0 solids (baked)
FEATURE [Part::Helix] Helix002
  Angle = 0
  AttacherType = Attacher::AttachEngine3D
  Height = 3
  LocalCoord = 0
  Pitch = 110
  Radius = 30
  Style = 1
FEATURE [Part::Sweep] Sweep024
  Frenet = true
  Placement = pos=(0,0,0) rot=(0,0,1;0.10472rad)
  Sections = -> [Face019]
  Solid = true
  Spine = -> Helix002 [Edge1]
  Transition = 1
FEATURE [Part::Helix] Helix
  Angle = 0
  AttacherType = Attacher::AttachEngine3D
  Height = 3
  LocalCoord = 0
  Pitch = 29.73
  Radius = 10
  Style = 1
FEATURE [Part::Sweep] Sweep025
  Frenet = true
  Placement = pos=(18,0,0) rot=(0,0,1;0rad)
  Sections = -> [Face020]
  Solid = true
  Spine = -> Helix
  Transition = 1
FEATURE [Part::Mirroring] Part__Mirroring005066  label="Sweep025 (Mirror #54)"
  Base = (0,0,3)
  Normal = (0,0,1)
  Source = -> Sweep025
FEATURE [Part::Feature] Face021
  shape: bbox 18.01 x 18.01 x 2e-07 mm, 1 faces, 0 solids (baked)
FEATURE [Part::Helix] Helix003
  Angle = 0
  AttacherType = Attacher::AttachEngine3D
  Height = 3
  LocalCoord = 0
  Pitch = 29.73
  Radius = 10
  Style = 1
FEATURE [Part::Sweep] Sweep026
  Frenet = true
  Placement = pos=(18,0,0) rot=(0,0,1;0rad)
  Sections = -> [Face021]
  Solid = true
  Spine = -> Helix003
  Transition = 1
FEATURE [Part::Feature] Face022
  shape: bbox 56.54 x 56.62 x 2e-07 mm, 1 faces, 0 solids (baked)
FEATURE [Part::Helix] Helix004
  Angle = 0
  AttacherType = Attacher::AttachEngine3D
  Height = 3
  LocalCoord = 0
  Pitch = 110
  Radius = 30
  Style = 1
FEATURE [Part::Sweep] Sweep027
  Frenet = true
  Placement = pos=(0,0,0) rot=(0,0,1;0.10472rad)
  Sections = -> [Face022]
  Solid = true
  Spine = -> Helix004 [Edge1]
  Transition = 1
FEATURE [Part::Mirroring] Part__Mirroring005067  label="Sweep027 (Mirror #55)"
  Base = (0,0,3)
  Normal = (0,0,1)
  Source = -> Sweep027
FEATURE [App::DocumentObjectGroup] Group024  label="Herringbone"
  Group = -> [Helix002,Helix,Part__Mirroring005066,Helix003,Sweep026,Helix004,Part__Mirroring005067,Sweep024]
FEATURE [Part::Feature] Face023
  shape: bbox 18.01 x 18.01 x 2e-07 mm, 1 faces, 0 solids (baked)
FEATURE [Part::Feature] Face024
  shape: bbox 56.54 x 56.62 x 2e-07 mm, 1 faces, 0 solids (baked)
FEATURE [Part::Extrusion] Extrude001
  Base = -> Face024
  Dir = (0,0,6)
  DirMode = 0
  FaceMakerClass = Part::FaceMakerExtrusion
  LengthFwd = 0
  LengthRev = 0
  Solid = true
  Symmetric = false
FEATURE [Part::Cut] Cut456181
  Base = -> Cylinder054099009137020
  Placement = pos=(0,0,0) rot=(0,0,1;0.10472rad)
  Tool = -> Extrude001
FEATURE [Part::Extrusion] Extrude002
  Base = -> Face023
  Dir = (0,0,5.8)
  DirMode = 0
  FaceMakerClass = Part::FaceMakerExtrusion
  LengthFwd = 0
  LengthRev = 0
  Placement = pos=(-10.5103,-14.5512,0) rot=(-0.45399,0.891007,0;3.14159rad)
  Solid = true
  Symmetric = false
FEATURE [Part::Cylinder] Cylinder054099009137021  label="Cylinder054099009137101"
  Angle = 360
  AttacherType = Attacher::AttachEngine3D
  Height = 18
  Placement = pos=(0,0,-11) rot=(0,0,1;0rad)
  Radius = 6
FEATURE [Part::MultiFuse] Fusion051010010012015014088020072
  Placement = pos=(0.0698401,0.0110616,0) rot=(-0.45399,0.891007,0;3.14159rad)
  Shapes = -> [Cut456181,Cylinder054099009137021]
FEATURE [Part::Chamfer] Chamfer006012099
  Base = -> Fusion051010010012015014088020072
  Edges = 1 edges r=1: [Edge701]
FEATURE [Part::Chamfer] Chamfer006012100
  Base = -> Chamfer006012099
  Edges = 1 edges r=1: [Edge704]
FEATURE [Part::Cylinder] Cylinder054099009137023  label="Cylinder054099009137063"
  Angle = 360
  AttacherType = Attacher::AttachEngine3D
  Height = 100
  Placement = pos=(0,0,-70) rot=(0,0,1;0rad)
  Radius = 1.7
FEATURE [Part::Cylinder] Cylinder054099009137024  label="Cylinder054099009137064"
  Angle = 360
  AttacherType = Attacher::AttachEngine3D
  Height = 20
  Placement = pos=(0,0,-12.5) rot=(0,0,1;0rad)
  Radius = 5
FEATURE [Part::Cut] Cut456182
  Base = -> Chamfer006012100
  Tool = -> Cylinder054099009137023
FEATURE [Part::Box] Box112015002017004007004038086003009003088019011  label="Cube285"
  AttacherType = Attacher::AttachEngine3D
  Height = 25
  Length = 10
  Placement = pos=(2.75,-10,-14) rot=(0,0,1;0rad)
  Width = 20
FEATURE [Part::Feature] Box112015002017004007004038086003009003088019011001
  Placement = pos=(10.0353,-2.61843,-14) rot=(0,0,1;1.0472rad)
  shape: bbox 22.32 x 18.66 x 25 mm, 6 faces (baked)
FEATURE [Part::Feature] Box112015002017004007004038086003009003088019011002
  Placement = pos=(7.28525,7.38157,-14) rot=(0,0,1;2.0944rad)
  shape: bbox 22.32 x 18.66 x 25 mm, 6 faces (baked)
FEATURE [Part::Feature] Box112015002017004007004038086003009003088019011003
  Placement = pos=(-2.75,10,-14) rot=(0,0,1;3.14159rad)
  shape: bbox 10 x 20 x 25 mm, 6 faces (baked)
FEATURE [Part::Feature] Box112015002017004007004038086003009003088019011004
  Placement = pos=(-10.0353,2.61843,-14) rot=(0,0,1;4.18879rad)
  shape: bbox 22.32 x 18.66 x 25 mm, 6 faces (baked)
FEATURE [Part::Feature] Box112015002017004007004038086003009003088019011005
  Placement = pos=(-7.28525,-7.38157,-14) rot=(0,0,-1;1.0472rad)
  shape: bbox 22.32 x 18.66 x 25 mm, 6 faces (baked)
FEATURE [Part::MultiFuse] Fusion051010010012015014088020073
  Shapes = -> [Box112015002017004007004038086003009003088019011,Box112015002017004007004038086003009003088019011001,Box112015002017004007004038086003009003088019011003,Box112015002017004007004038086003009003088019011002,Box112015002017004007004038086003009003088019011004,Box112015002017004007004038086003009003088019011005]
FEATURE [Part::Cut] Cut456183
  Base = -> Cylinder054099009137024
  Placement = pos=(0,0,0) rot=(0,0,-1;0.401426rad)
  Tool = -> Fusion051010010012015014088020073
FEATURE [Part::Cut] Cut456184
  Base = -> Cut456182
  Tool = -> Cut456183
FEATURE [Part::Chamfer] Chamfer006012101  label="large-driven-gear"
  Base = -> Cut456184
  Edges = 6 edges r=0.5: [Edge715,Edge717,Edge720,Edge721,Edge724,Edge725]
FEATURE [Part::Cylinder] Cylinder054099009137025  label="motor-shaft-cylinder004"
  Angle = 360
  AttacherType = Attacher::AttachEngine3D
  Height = 28
  Placement = pos=(-8,0,1) rot=(0,0,1;0rad)
  Radius = 2.7
FEATURE [Part::Box] Box112015002017004007004038086003009003088019011006  label="Cube286"
  AttacherType = Attacher::AttachEngine3D
  Height = 10
  Length = 10
  Placement = pos=(-6.4,-5,22.5) rot=(0,0,1;0rad)
  Width = 10
FEATURE [Part::Box] Box112015002017004007004038086003009003088019011007  label="Cube287"
  AttacherType = Attacher::AttachEngine3D
  Height = 10
  Length = 10
  Placement = pos=(-19.6,-5,22.5) rot=(0,0,1;0rad)
  Width = 10
FEATURE [Part::Cut] Cut456185
  Base = -> Cylinder054099009137025
  Tool = -> Box112015002017004007004038086003009003088019011007
FEATURE [Part::Cut] Cut456186  label="motor-shaft005"
  Base = -> Cut456185
  Placement = pos=(-2.59,-14.58,-28.6) rot=(0,0,1;0rad)
  Tool = -> Box112015002017004007004038086003009003088019011006
FEATURE [Part::Cut] Cut456187  label="small-drive-gear"
  Base = -> Extrude002
  Tool = -> Cut456186
FEATURE [Part::Chamfer] Chamfer006012102  label="6172 Extruder Body001"
  Base = -> Chamfer006012072
  Edges = 1 edges r=1: [Edge6]
  Placement = pos=(-24.8089,7.25448,52) rot=(1,0,0;3.14159rad)
FEATURE [Part::Feature] Part__Feature166  label="1306001"
  Placement = pos=(-24.9298,0.0761051,25.9765) rot=(0.707107,0.707107,0;3.14159rad)
  shape: bbox 70.89 x 54.16 x 21.5 mm, 245 faces (baked)
FEATURE [Part::Box] Box112015002017004007004038086003009003088019011013  label="Cube293"
  AttacherType = Attacher::AttachEngine3D
  Height = 21.5
  Length = 43
  Placement = pos=(-48,-21,4.5) rot=(0,0,1;0rad)
  Width = 42
FEATURE [Part::MultiFuse] Fusion051010010012015014088020074
  Shapes = -> [Part__Feature166,Box112015002017004007004038086003009003088019011013]
FEATURE [Part::Box] Box112015002017004007004038086003009003088019011014  label="Cube294"
  AttacherType = Attacher::AttachEngine3D
  Height = 21.5
  Length = 47
  Placement = pos=(-50,-23,-10) rot=(0,0,1;0rad)
  Width = 45
FEATURE [Part::Cut] Cut456188
  Base = -> Fusion051010010012015014088020074
  Tool = -> Box112015002017004007004038086003009003088019011014
FEATURE [Part::Box] Box112015002017004007004038086003009003088019011015  label="Cube295"
  AttacherType = Attacher::AttachEngine3D
  Height = 21.5
  Length = 32
  Placement = pos=(-63,-24,6.5) rot=(0,0,1;0rad)
  Width = 47
FEATURE [Part::Cut] Cut456189
  Base = -> Cut456188
  Tool = -> Box112015002017004007004038086003009003088019011015
FEATURE [Part::Box] Box112015002017004007004038086003009003088019011016  label="Cube296"
  AttacherType = Attacher::AttachEngine3D
  Height = 10
  Length = 8.5
  Placement = pos=(-16,2.5,4.8) rot=(0,0,-1;0.488692rad)
  Width = 10
FEATURE [Part::Cylinder] Cylinder054099009137031  label="swing-centre"
  Angle = 360
  AttacherType = Attacher::AttachEngine3D
  Height = 31.2
  Placement = pos=(-9.75,4.65,-0.2) rot=(0,0,1;0rad)
  Radius = 37.3
FEATURE [Part::Cylinder] Cylinder054099009137032  label="swing-centre001"
  Angle = 360
  AttacherType = Attacher::AttachEngine3D
  Height = 50
  Placement = pos=(-9.75,4.65,-5.2) rot=(0,0,1;0rad)
  Radius = 2.2
FEATURE [Part::Cylinder] Cylinder054099009137033  label="swing-centre002"
  Angle = 360
  AttacherType = Attacher::AttachEngine3D
  Height = 43.2
  Placement = pos=(-9.75,4.65,-6.2) rot=(0,0,1;0rad)
  Radius = 32.8
FEATURE [Part::Cut] Cut456190  label="screw-slot-1"
  Base = -> Cylinder054099009137031
  Tool = -> Cylinder054099009137033
FEATURE [Part::Cylinder] Cylinder054099009137034  label="swing-centre003"
  Angle = 360
  AttacherType = Attacher::AttachEngine3D
  Height = 37.2
  Placement = pos=(-9.75,4.65,-3.2) rot=(0,0,1;0rad)
  Radius = 3.3
FEATURE [Part::Cylinder] Cylinder054099009137035  label="swing-centre004"
  Angle = 360
  AttacherType = Attacher::AttachEngine3D
  Height = 21.2
  Placement = pos=(-9.75,4.65,3) rot=(0,0,1;0rad)
  Radius = 31.8
FEATURE [Part::Cut] Cut456191  label="motor-slot-1"
  Base = -> Cylinder054099009137035
  Tool = -> Cylinder054099009137034
FEATURE [Part::Box] Box112015002017004007004038086003009003088019011017  label="slot-end-1"
  AttacherType = Attacher::AttachEngine3D
  Height = 40
  Length = 60
  Placement = pos=(-9.75,4.65,-2) rot=(0,0,1;4.01426rad)
  Width = 60
FEATURE [Part::Box] Box112015002017004007004038086003009003088019011018  label="slot-end-002"
  AttacherType = Attacher::AttachEngine3D
  Height = 40
  Length = 60
  Placement = pos=(-9.75,4.65,-2) rot=(0,0,1;4.04916rad)
  Width = 60
FEATURE [Part::Box] Box112015002017004007004038086003009003088019011019  label="slot-end-003"
  AttacherType = Attacher::AttachEngine3D
  Height = 48
  Length = 60
  Placement = pos=(-9.75,4.65,-4) rot=(0,0,-1;1.5708rad)
  Width = 60
FEATURE [Part::Cut] Cut456192
  Base = -> Box112015002017004007004038086003009003088019011017
  Tool = -> Box112015002017004007004038086003009003088019011019
FEATURE [Part::MultiCommon] Common023
  Shapes = -> [Cut456190,Cut456192]
FEATURE [Part::MultiFuse] Fusion051010010012015014088020075  label="extruder-drive-blank"
  Shapes = -> [Cut456189,Box112015002017004007004038086003009003088019011016]
FEATURE [Part::Box] Box112015002017004007004038086003009003088019011020  label="slot-end-004"
  AttacherType = Attacher::AttachEngine3D
  Height = 40
  Length = 60
  Placement = pos=(-9.75,4.65,-2) rot=(0,0,1;2.86234rad)
  Width = 60
FEATURE [Part::Fillet] Fillet079
  Base = -> Common023
  Edges = 2 edges r=2: [Edge2,Edge8]
FEATURE [Part::Fillet] Fillet080  label="extruder-screw-slot"
  Base = -> Fillet079
  Edges = 2 edges r=2: [Edge3,Edge12]
FEATURE [Part::MultiCommon] Common024
  Shapes = -> [Box112015002017004007004038086003009003088019011020,Box112015002017004007004038086003009003088019011018]
FEATURE [Part::MultiCommon] Common025
  Shapes = -> [Cut456191,Common024]
FEATURE [Part::Cylinder] Cylinder054099009137036  label="motor-hole"
  Angle = 360
  AttacherType = Attacher::AttachEngine3D
  Height = 21.2
  Placement = pos=(-14.8811,-12.1331,3) rot=(0,0,-1;0.296706rad)
  Radius = 14.25
FEATURE [Part::Cylinder] Cylinder054099009137037  label="motor-hole001"
  Angle = 360
  AttacherType = Attacher::AttachEngine3D
  Height = 21.2
  Placement = pos=(-20.5549,-9.17959,3) rot=(0,0,-1;0.663225rad)
  Radius = 14.25
FEATURE [Part::MultiFuse] Fusion051010010012015014088020076  label="motor-slot"
  Shapes = -> [Common025,Cylinder054099009137036,Cylinder054099009137037]
FEATURE [Part::Box] Box112015002017004007004038086003009003088019011021  label="Cube297"
  AttacherType = Attacher::AttachEngine3D
  Height = 21.2
  Length = 28
  Placement = pos=(-35,-36,4.8) rot=(0,0,1;0rad)
  Width = 19
FEATURE [Part::MultiFuse] Fusion051010010012015014088020077
  Shapes = -> [Fusion051010010012015014088020075,Box112015002017004007004038086003009003088019011021]
FEATURE [Part::Cut] Cut456193
  Base = -> Fusion051010010012015014088020077
  Tool = -> Fusion051010010012015014088020076
FEATURE [Part::Cut] Cut456194
  Base = -> Cut456193
  Tool = -> Fillet080
FEATURE [Part::Cut] Cut456195
  Base = -> Cut456194
  Tool = -> Cylinder054099009137032
FEATURE [Part::Fillet] Fillet081
  Base = -> Cut456195
  Edges = 1 edges r=7: [Edge64]
FEATURE [Part::Fillet] Fillet082
  Base = -> Fillet081
  Edges = 1 edges r=4: [Edge192]
FEATURE [Part::Cylinder] Cylinder054099009137038  label="swing-centre005"
  Angle = 360
  AttacherType = Attacher::AttachEngine3D
  Height = 31.2
  Placement = pos=(-9.75,4.65,-0.2) rot=(0,0,1;0rad)
  Radius = 40
FEATURE [Part::MultiCommon] Common026
  Shapes = -> [Fillet082,Cylinder054099009137038]
FEATURE [Part::Fillet] Fillet083
  Base = -> Common026
  Edges = 1 edges r=3: [Edge20]
FEATURE [Part::Fillet] Fillet084
  Base = -> Fillet083
  Edges = 1 edges r=3: [Edge21]
FEATURE [Part::Fillet] Fillet085
  Base = -> Fillet084
  Edges = 1 edges r=3: [Edge251]
FEATURE [Part::Fillet] Fillet086
  Base = -> Fillet085
  Edges = 1 edges r=3: [Edge26]
FEATURE [Part::Chamfer] Chamfer006012103
  Base = -> Fillet086
  Edges = 9 edges r=0.3: [Edge59,Edge150,Edge155,Edge158,Edge181,Edge288,Edge289,Edge290,Edge291]
FEATURE [Part::Chamfer] Chamfer006012104
  Base = -> Chamfer006012103
  Edges = 8 edges r=0.3: [Edge147,Edge148,Edge149,Edge150,Edge151,Edge152,Edge153,Edge154]
FEATURE [Part::Chamfer] Chamfer006012105  label="extruder-drive-block"
  Base = -> Chamfer006012104
  Edges = 1 edges r=0.3: [Edge61]
FEATURE [App::DocumentObjectGroup] Group012  label="6169 extruder-drive"
  Group = -> [Part__Feature001,Part__Feature162,Part__Feature163,Part__Feature004,Part__Feature164,Part__Feature006,Part__Feature007,Part__Feature008,Part__Feature010,Part__Feature011,Part__Feature012,Part__Feature013,Part__Feature014,Part__Feature015,Part__Feature016,Part__Feature020,Part__Feature021,Part__Feature026,Part__Mirroring005056,Fillet046,Chamfer006012101,Cut456187,Chamfer006012105]
FEATURE [Part::Cylinder] Cylinder054099009137039  label="z-axis"
  Angle = 360
  AttacherType = Attacher::AttachEngine3D
  Height = 500
  Placement = pos=(0,0,-344) rot=(0,0,1;0rad)
  Radius = 0.5
FEATURE [Part::Box] Box112015002017004007004038086003009003088019011022  label="Cube298"
  AttacherType = Attacher::AttachEngine3D
  Height = 30
  Length = 5
  Placement = pos=(-11.5,-30,-30) rot=(0,0,1;0rad)
  Width = 60
FEATURE [Part::Cylinder] Cylinder054099009137040  label="mounting-hole-019"
  Angle = 360
  AttacherType = Attacher::AttachEngine3D
  Height = 100
  Placement = pos=(-40,0,-7) rot=(0,1,0;1.5708rad)
  Radius = 1.7
FEATURE [Part::Cylinder] Cylinder054099009137041  label="mounting-hole-020"
  Angle = 360
  AttacherType = Attacher::AttachEngine3D
  Height = 100
  Placement = pos=(-40,-27,-19) rot=(0,1,0;1.5708rad)
  Radius = 1.7
FEATURE [Part::Cylinder] Cylinder054099009137042  label="mounting-hole-021"
  Angle = 360
  AttacherType = Attacher::AttachEngine3D
  Height = 100
  Placement = pos=(-40,27,-19) rot=(0,1,0;1.5708rad)
  Radius = 1.7
FEATURE [Part::Cone] Cone033  label="csink-012"
  Angle = 360
  AttacherType = Attacher::AttachEngine3D
  Height = 2.5
  Placement = pos=(-9,-27,-19) rot=(0,-1,0;1.5708rad)
  Radius1 = 1.7
  Radius2 = 3
FEATURE [Part::Cone] Cone034  label="csink-013"
  Angle = 360
  AttacherType = Attacher::AttachEngine3D
  Height = 2.5
  Placement = pos=(-9,0,-7) rot=(0,-1,0;1.5708rad)
  Radius1 = 1.7
  Radius2 = 3
FEATURE [Part::Cone] Cone035  label="csink-014"
  Angle = 360
  AttacherType = Attacher::AttachEngine3D
  Height = 2.5
  Placement = pos=(-9,27,-19) rot=(0,-1,0;1.5708rad)
  Radius1 = 1.7
  Radius2 = 3
FEATURE [Part::Box] Box112015002017004007004038086003009003088019011023  label="Cube299"
  AttacherType = Attacher::AttachEngine3D
  Height = 2
  Length = 2
  Placement = pos=(-13.5,-15,-28.2) rot=(0,0,1;0rad)
  Width = 30
FEATURE [Part::Box] Box112015002017004007004038086003009003088019011024  label="Cube300"
  AttacherType = Attacher::AttachEngine3D
  Height = 2
  Length = 2
  Placement = pos=(-13.5,-15,-15.8) rot=(0,0,1;0rad)
  Width = 30
FEATURE [Part::Cylinder] Cylinder054099009137043  label="wire-clamp-screw-hole-007"
  Angle = 360
  AttacherType = Attacher::AttachEngine3D
  Height = 30
  Placement = pos=(-23.5,-5,-12) rot=(0,1,0;1.5708rad)
  Radius = 2.5
FEATURE [Part::Cylinder] Cylinder054099009137044  label="wire-clamp-screw-hole-008"
  Angle = 360
  AttacherType = Attacher::AttachEngine3D
  Height = 30
  Placement = pos=(-23.5,-5,-4) rot=(0,1,0;1.5708rad)
  Radius = 2.5
FEATURE [Part::Cylinder] Cylinder054099009137045  label="ball-slider-clamp-hole003"
  Angle = 360
  AttacherType = Attacher::AttachEngine3D
  Height = 100
  Placement = pos=(-40,0,-21) rot=(0,1,0;1.5708rad)
  Radius = 1.4
FEATURE [Part::MultiFuse] Fusion051010010012015014088020078
  Shapes = -> [Box112015002017004007004038086003009003088019011024,Box112015002017004007004038086003009003088019011023,Box112015002017004007004038086003009003088019011022]
FEATURE [Part::Chamfer] Chamfer006012106
  Base = -> Fusion051010010012015014088020078
  Edges = 2 edges r=1.7: [Edge24,Edge36]
FEATURE [Part::MultiFuse] Fusion051010010012015014088020079
  Shapes = -> [Cylinder054099009137045,Cylinder054099009137040,Cylinder054099009137041,Cone033,Cone035,Cylinder054099009137043,Cylinder054099009137044,Cylinder054099009137042,Cone034]
FEATURE [Part::Cut] Cut456196  label="slider-ball-mount"
  Base = -> Chamfer006012106
  Tool = -> Fusion051010010012015014088020079
FEATURE [App::DocumentObjectGroup] Group015  label="6151 Slider"
  Group = -> [Cut355,Cylinder054037,Cylinder054038,Cut456196]
FEATURE [App::DocumentObjectGroup] Group014  label="6150 Axis"
  Group = -> [Group015,Cut417,Cut433,Cut455,Group005]
FEATURE [App::DocumentObjectGroup] Group013  label="6149 Slider Ball Holder"
  Group = -> [Group014]
FEATURE [App::DocumentObjectGroup] Group006  label="6148 Motor Drive"
  Group = -> [Group013,Group016]
FEATURE [Part::Box] Box112015002017004007004038086003009003088019011027  label="Cube303"
  AttacherType = Attacher::AttachEngine3D
  Height = 10
  Length = 4
  Placement = pos=(-24,-32.3,-130) rot=(0,0,1;0rad)
  Width = 4
FEATURE [Part::Box] Box112015002017004007004038086003009003088019011028  label="Cube304"
  AttacherType = Attacher::AttachEngine3D
  Height = 10
  Length = 20
  Placement = pos=(-40,-37,-130) rot=(0,0,1;0rad)
  Width = 6
FEATURE [Part::MultiFuse] Fusion051010010012015014088020084
  Shapes = -> [Box112015002017004007004038086003009003088019011027,Box112015002017004007004038086003009003088019011028]
FEATURE [Part::Chamfer] Chamfer006012110  label="snap-tab-c"
  Base = -> Fusion051010010012015014088020084
  Edges = 1 edges r=4: [Edge27]
FEATURE [Part::Chamfer] Chamfer006012111  label="snap-tab-c001"
  Base = -> Fusion051010010012015014088020084
  Edges = 1 edges r=4: [Edge27]
FEATURE [Part::Mirroring] Part__Mirroring005069  label="snap-tab-c (Mirror #57)"
  Base = (0,0,0)
  Normal = (0,1,0)
  Source = -> Chamfer006012110
FEATURE [Part::MultiFuse] Fusion051010010012015014088020085  label="hot-end-snap-tabs"
  Shapes = -> [Chamfer006012111,Part__Mirroring005069]
FEATURE [Part::Chamfer] Chamfer006012112
  Base = -> Box112015002017004007004038086003009003088010
  Edges = 1 edges r=1.7: [Edge4]
FEATURE [Part::Chamfer] Chamfer006012113
  Base = -> Box112015002017004007004038086003009003088009
  Edges = 1 edges r=1.7: [Edge2]
FEATURE [Part::MultiFuse] Fusion051010010012015014088020086  label="hot-end-ball-mounts-0"
  Placement = pos=(0,0,0) rot=(0,0,1;2.0944rad)
  Shapes = -> [Chamfer006012113,Chamfer006012112,Fusion051010010012015014088020085]
FEATURE [Part::MultiFuse] Fusion051010010012015014088020087  label="hot-end-ball-mounts001"
  Placement = pos=(0,0,0) rot=(0,0,1;4.18879rad)
  Shapes = -> [Chamfer006012113,Chamfer006012112,Fusion051010010012015014088020085]
FEATURE [Part::MultiFuse] Fusion051010010012015014088020088  label="hot-end-ball-mounts002"
  Shapes = -> [Chamfer006012113,Chamfer006012112,Fusion051010010012015014088020085]
FEATURE [Part::MultiFuse] Fusion051010010012015014088020089  label="hot-end-ball-mounts"
  Shapes = -> [Fusion051010010012015014088020086,Fusion051010010012015014088020088,Fusion051010010012015014088020087]
FEATURE [Part::Cylinder] Cylinder054099009137046  label="ball-slider-clamp-hole004"
  Angle = 360
  AttacherType = Attacher::AttachEngine3D
  Height = 30
  Placement = pos=(23.5,-40.7032,-123) rot=(-0.654654,0.377964,0.654654;2.41886rad)
  Radius = 1.4
FEATURE [Part::Cylinder] Cylinder054099009137047  label="ball-slider-clamp-hole005"
  Angle = 360
  AttacherType = Attacher::AttachEngine3D
  Height = 30
  Placement = pos=(23.5,40.7032,-123) rot=(-0.654654,-0.377964,0.654654;3.86433rad)
  Radius = 1.4
FEATURE [Part::MultiFuse] Fusion051010010012015014088020090  label="hot-end-ball-mount-clamp-holes"
  Shapes = -> [Cylinder054099009137009,Cylinder054099009137046,Cylinder054099009137047]
FEATURE [Part::Cylinder] Cylinder054099009137048  label="cable-tie-hole"
  Angle = 360
  AttacherType = Attacher::AttachEngine3D
  Height = 500
  Placement = pos=(-19,25,-344) rot=(0,0,1;0rad)
  Radius = 1.5
FEATURE [Part::MultiFuse] Fusion051010010012015014088020091  label="hot-end-final-holes"
  Shapes = -> [Cylinder054099009137048,Fusion051010010012015014088020090]
FEATURE [Part::MultiFuse] Fusion051010010012015014088020092
  Shapes = -> [Cut456172,Fusion051010010012015014088020089]
FEATURE [Part::Cut] Cut456197  label="hot-endx"
  Base = -> Fusion051010010012015014088020092
  Placement = pos=(0,0,0) rot=(0,0,-1;1.0472rad)
  Tool = -> Fusion051010010012015014088020091
FEATURE [Part::Mirroring] Part__Mirroring005070  label="6130 base arm L001"
  Base = (0,0,0)
  Normal = (0,1,0)
  Placement = pos=(-184.5,-106.521,0) rot=(0,0,1;4.18879rad)
  Source = -> Cut456062
FEATURE [Part::Mirroring] Part__Mirroring005071  label="6130 base arm L002"
  Base = (0,0,0)
  Normal = (0,1,0)
  Source = -> Cut456062
FEATURE [App::DocumentObjectGroup] Group018  label="6129 Bottom Link"
  Group = -> [Part__Mirroring005043,Cut450,Cut406,Cut456070,Part__Mirroring005070,Part__Mirroring005071]
FEATURE [App::DocumentObjectGroup] Group017  label="6137 Main Body"
  Group = -> [Group006,Group018,Group019]
FEATURE [Part::Cylinder] Cylinder054099009137049  label="machine-center"
  Angle = 360
  AttacherType = Attacher::AttachEngine3D
  Height = 500
  Placement = pos=(-123,0,-344) rot=(0,0,1;0rad)
  Radius = 0.5
FEATURE [Part::Cylinder] Cylinder054099009137052  label="Cylinder054099009137102"
  Angle = 360
  AttacherType = Attacher::AttachEngine3D
  Height = 17
  Placement = pos=(-60,-22,-315) rot=(0,0,1;0rad)
  Radius = 1.7
FEATURE [Part::Cylinder] Cylinder054099009137053  label="Cylinder054099009137103"
  Angle = 360
  AttacherType = Attacher::AttachEngine3D
  Height = 17
  Placement = pos=(-56,-22,-315) rot=(0,0,1;0rad)
  Radius = 1.7
FEATURE [Part::Box] Box112015002017004007004038086003009003088019011029  label="Cube305"
  AttacherType = Attacher::AttachEngine3D
  Height = 10
  Length = 4
  Placement = pos=(-60,-23.7,-310) rot=(0,0,1;0rad)
  Width = 3.4
FEATURE [Part::Cylinder] Cylinder054099009137054  label="Cylinder054099009137104"
  Angle = 360
  AttacherType = Attacher::AttachEngine3D
  Height = 17
  Placement = pos=(-31,-22,-315) rot=(0,0,1;0rad)
  Radius = 1.7
FEATURE [Part::Cylinder] Cylinder054099009137055  label="Cylinder054099009137105"
  Angle = 360
  AttacherType = Attacher::AttachEngine3D
  Height = 17
  Placement = pos=(-35,-22,-315) rot=(0,0,1;0rad)
  Radius = 1.7
FEATURE [Part::Box] Box112015002017004007004038086003009003088019011030  label="Cube306"
  AttacherType = Attacher::AttachEngine3D
  Height = 10
  Length = 4
  Placement = pos=(-35,-23.7,-310) rot=(0,0,1;0rad)
  Width = 3.4
FEATURE [Part::Box] Box112015002017004007004038086003009003088019011031  label="Cube307"
  AttacherType = Attacher::AttachEngine3D
  Height = 5
  Length = 60
  Placement = pos=(-65,-43,-307) rot=(0,0,1;0rad)
  Width = 25
FEATURE [Part::Cylinder] Cylinder054099009137056  label="Cylinder054099009137106"
  Angle = 360
  AttacherType = Attacher::AttachEngine3D
  Height = 10
  Placement = pos=(-118,-29.5,-314) rot=(1,0,0;1.5708rad)
  Radius = 6
FEATURE [Part::Cylinder] Cylinder054099009137057  label="Cylinder054099009137107"
  Angle = 360
  AttacherType = Attacher::AttachEngine3D
  Height = 10
  Placement = pos=(-118,-33,-314) rot=(1,0,0;1.5708rad)
  Radius = 4.2
FEATURE [Part::Box] Box112015002017004007004038086003009003088019011032  label="Cube308"
  AttacherType = Attacher::AttachEngine3D
  Height = 18
  Length = 22
  Placement = pos=(-126,-41.5,-322) rot=(0,0,1;0rad)
  Width = 5
FEATURE [Part::Cylinder] Cylinder054099009137060  label="Cylinder054099009137108"
  Angle = 360
  AttacherType = Attacher::AttachEngine3D
  Height = 10
  Placement = pos=(-133,-29,-311) rot=(1,0,0;1.5708rad)
  Radius = 1.1
FEATURE [Part::Cylinder] Cylinder054099009137061  label="Cylinder054099009137109"
  Angle = 360
  AttacherType = Attacher::AttachEngine3D
  Height = 10
  Placement = pos=(-133,-25,-311) rot=(1,0,0;1.5708rad)
  Radius = 2.1
FEATURE [Part::Cone] Cone036  label="Cone022"
  Angle = 360
  AttacherType = Attacher::AttachEngine3D
  Height = 10
  Placement = pos=(-133,-37,-311) rot=(1,0,0;1.5708rad)
  Radius1 = 1.1
  Radius2 = 3
FEATURE [Part::Box] Box112015002017004007004038086003009003088019011037  label="Cube313"
  AttacherType = Attacher::AttachEngine3D
  Height = 13
  Length = 15
  Placement = pos=(-141,-41.5,-316) rot=(0,0,1;0rad)
  Width = 11
FEATURE [Part::Cylinder] Cylinder054099009137062  label="pneumatic-fitting"
  Angle = 360
  AttacherType = Attacher::AttachEngine3D
  Height = 30
  Placement = pos=(-123,0,-192) rot=(0,0,1;0rad)
  Radius = 6
FEATURE [Part::Cylinder] Cylinder054099009137067  label="pcb-m4-hole003"
  Angle = 360
  AttacherType = Attacher::AttachEngine3D
  Height = 17
  Placement = pos=(-10,-39,-323) rot=(0,0,1;0rad)
  Radius = 1.8
FEATURE [Part::Cylinder] Cylinder054099009137068  label="pcb-post003"
  Angle = 360
  AttacherType = Attacher::AttachEngine3D
  Height = 17
  Placement = pos=(-10,-39,-322) rot=(0,0,1;0rad)
  Radius = 4
FEATURE [Part::Box] Box112015002017004007004038086003009003088019011041  label="Cube317"
  AttacherType = Attacher::AttachEngine3D
  Height = 24
  Length = 6
  Placement = pos=(-18.7,-45.5,-326) rot=(0,0,1;0rad)
  Width = 14
FEATURE [Part::Cut] Cut456202
  Base = -> Cylinder054099009137068
  Tool = -> Box112015002017004007004038086003009003088019011041
FEATURE [Part::Cut] Cut456203
  Base = -> Cut456202
  Tool = -> Cylinder054099009137067
FEATURE [Part::Fillet] Fillet090  label="duet-post-002"
  Base = -> Cut456203
  Edges = 2 edges r=3: [Edge3,Edge6]
FEATURE [Part::Chamfer] Chamfer006012114  label="duet-post"
  Base = -> Fillet090
  Edges = 1 edges r=0.7: [Edge9]
FEATURE [Part::Chamfer] Chamfer006012115  label="duet-post001"
  Base = -> Fillet090
  Edges = 1 edges r=0.7: [Edge9]
  Placement = pos=(-63,-49,0) rot=(0,0,-1;1.5708rad)
FEATURE [Part::MultiFuse] Fusion051010010012015014088020093
  Shapes = -> [Box112015002017004007004038086003009003088019011031,Chamfer006012114]
FEATURE [Part::MultiFuse] Fusion051010010012015014088020094
  Shapes = -> [Cylinder054099009137052,Cylinder054099009137053,Box112015002017004007004038086003009003088019011029,Cylinder054099009137054,Cylinder054099009137055,Box112015002017004007004038086003009003088019011030]
FEATURE [Part::Cut] Cut456204
  Base = -> Fusion051010010012015014088020093
  Tool = -> Fusion051010010012015014088020094
FEATURE [Part::Chamfer] Chamfer006012116
  Base = -> Cut456204
  Edges = 5 edges r=2: [Edge23,Edge24,Edge25,Edge26,Edge27]
FEATURE [Part::Chamfer] Chamfer006012117
  Base = -> Chamfer006012116
  Edges = 5 edges r=2: [Edge15,Edge16,Edge17,Edge18,Edge19]
FEATURE [Part::Fillet] Fillet091  label="duet-mount-1"
  Base = -> Chamfer006012117
  Edges = 4 edges r=4: [Edge40,Edge42,Edge43,Edge45]
  Placement = pos=(0,0,0) rot=(0,0,1;0.523599rad)
FEATURE [Part::Box] Box112015002017004007004038086003009003088019011042  label="Cube318"
  AttacherType = Attacher::AttachEngine3D
  Height = 5
  Length = 64
  Placement = pos=(-161,-43,-307) rot=(0,0,1;0rad)
  Width = 25
FEATURE [Part::Box] Box112015002017004007004038086003009003088019011043  label="Cube319"
  AttacherType = Attacher::AttachEngine3D
  Height = 11
  Length = 20
  Placement = pos=(-108,-36.3,-310) rot=(0,0,1;0rad)
  Width = 20
FEATURE [Part::Cut] Cut456205
  Base = -> Box112015002017004007004038086003009003088019011042
  Tool = -> Box112015002017004007004038086003009003088019011043
FEATURE [Part::MultiFuse] Fusion051010010012015014088020095
  Placement = pos=(-97,0,0) rot=(0,0,1;0rad)
  Shapes = -> [Cylinder054099009137052,Cylinder054099009137053,Box112015002017004007004038086003009003088019011029,Cylinder054099009137054,Cylinder054099009137055,Box112015002017004007004038086003009003088019011030]
FEATURE [Part::Cut] Cut456206
  Base = -> Cut456205
  Tool = -> Fusion051010010012015014088020095
FEATURE [Part::Chamfer] Chamfer006012118
  Base = -> Cut456206
  Edges = 10 edges r=2: [Edge27,Edge28,Edge29,Edge30,Edge31,Edge32,Edge33,Edge34,Edge35,Edge36]
FEATURE [Part::Chamfer] Chamfer006012119
  Base = -> Chamfer006012118
  Edges = 1 edges r=18: [Edge30]
FEATURE [Part::Fillet] Fillet092
  Base = -> Chamfer006012119
  Edges = 6 edges r=3: [Edge19,Edge20,Edge21,Edge23,Edge25,Edge30]
FEATURE [Part::MultiFuse] Fusion051010010012015014088020096
  Shapes = -> [Fillet092,Box112015002017004007004038086003009003088019011032,Box112015002017004007004038086003009003088019011037]
FEATURE [Part::MultiFuse] Fusion051010010012015014088020097
  Shapes = -> [Cylinder054099009137060,Cylinder054099009137061,Cone036]
FEATURE [Part::MultiFuse] Fusion051010010012015014088020098
  Shapes = -> [Cylinder054099009137056,Cylinder054099009137057]
FEATURE [Part::MultiFuse] Fusion051010010012015014088020099
  Shapes = -> [Fusion051010010012015014088020097,Fusion051010010012015014088020098]
FEATURE [Part::Cut] Cut456207
  Base = -> Fusion051010010012015014088020096
  Tool = -> Fusion051010010012015014088020099
FEATURE [Part::MultiFuse] Fusion051010010012015014088020100
  Shapes = -> [Cut456207,Chamfer006012115]
FEATURE [Part::Fillet] Fillet093
  Base = -> Fusion051010010012015014088020100
  Edges = 1 edges r=8: [Edge5]
FEATURE [Part::Fillet] Fillet094
  Base = -> Fillet093
  Edges = 1 edges r=4: [Edge41]
FEATURE [Part::Fillet] Fillet095
  Base = -> Fillet094
  Edges = 2 edges r=4: [Edge71,Edge77]
FEATURE [Part::Fillet] Fillet096  label="duet-mount-2"
  Base = -> Fillet095
  Edges = 1 edges r=1.5: [Edge110]
  Placement = pos=(0,0,0) rot=(0,0,1;0.523599rad)
FEATURE [Part::Chamfer] Chamfer006012063
  Base = -> Chamfer006012062
  Edges = 5 edges r=2: [Edge10,Edge11,Edge12,Edge13,Edge14]
  Placement = pos=(-25,0,0) rot=(0,0,1;0rad)
FEATURE [Part::Cylinder] Cylinder054099009137069  label="pcb-post004"
  Angle = 360
  AttacherType = Attacher::AttachEngine3D
  Height = 17
  Placement = pos=(29.3397,70.8179,-322) rot=(0,0,-1;0.523599rad)
  Radius = 4
FEATURE [Part::Cylinder] Cylinder054099009137070  label="pcb-m4-hole004"
  Angle = 360
  AttacherType = Attacher::AttachEngine3D
  Height = 17
  Placement = pos=(29.3397,70.8179,-323) rot=(0,0,-1;0.523599rad)
  Radius = 1.8
FEATURE [Part::Cylinder] Cylinder054099009137071  label="Cylinder054099009137110"
  Angle = 360
  AttacherType = Attacher::AttachEngine3D
  Height = 17
  Placement = pos=(-60,-22,-315) rot=(0,0,1;0rad)
  Radius = 1.7
FEATURE [Part::Cylinder] Cylinder054099009137072  label="Cylinder054099009137111"
  Angle = 360
  AttacherType = Attacher::AttachEngine3D
  Height = 17
  Placement = pos=(-56,-22,-315) rot=(0,0,1;0rad)
  Radius = 1.7
FEATURE [Part::Box] Box112015002017004007004038086003009003088019011044  label="Cube320"
  AttacherType = Attacher::AttachEngine3D
  Height = 10
  Length = 4
  Placement = pos=(-60,-23.7,-310) rot=(0,0,1;0rad)
  Width = 3.4
FEATURE [Part::Cylinder] Cylinder054099009137073  label="Cylinder054099009137112"
  Angle = 360
  AttacherType = Attacher::AttachEngine3D
  Height = 17
  Placement = pos=(-31,-22,-315) rot=(0,0,1;0rad)
  Radius = 1.7
FEATURE [Part::Cylinder] Cylinder054099009137074  label="Cylinder054099009137113"
  Angle = 360
  AttacherType = Attacher::AttachEngine3D
  Height = 17
  Placement = pos=(-35,-22,-315) rot=(0,0,1;0rad)
  Radius = 1.7
FEATURE [Part::Box] Box112015002017004007004038086003009003088019011045  label="Cube321"
  AttacherType = Attacher::AttachEngine3D
  Height = 10
  Length = 4
  Placement = pos=(-35,-23.7,-310) rot=(0,0,1;0rad)
  Width = 3.4
FEATURE [Part::Box] Box112015002017004007004038086003009003088019011046  label="Cube322"
  AttacherType = Attacher::AttachEngine3D
  Height = 5
  Length = 37
  Placement = pos=(43,52,-307) rot=(0,0,1;1.5708rad)
  Width = 25
FEATURE [Part::MultiFuse] Fusion051010010012015014088020101
  Placement = pos=(0,116,0) rot=(0,0,1;1.5708rad)
  Shapes = -> [Cylinder054099009137071,Cylinder054099009137072,Box112015002017004007004038086003009003088019011044,Cylinder054099009137073,Cylinder054099009137074,Box112015002017004007004038086003009003088019011045]
FEATURE [Part::Cut] Cut456208
  Base = -> Cylinder054099009137069
  Tool = -> Cylinder054099009137070
FEATURE [Part::Chamfer] Chamfer006012120
  Base = -> Cut456208
  Edges = 1 edges r=0.7: [Edge4]
FEATURE [Part::MultiFuse] Fusion051010010012015014088020102
  Shapes = -> [Chamfer006012120,Box112015002017004007004038086003009003088019011046]
FEATURE [Part::Cut] Cut456209
  Base = -> Fusion051010010012015014088020102
  Tool = -> Fusion051010010012015014088020101
FEATURE [Part::Chamfer] Chamfer006012121  label="duet-mount-3"
  Base = -> Cut456209
  Edges = 10 edges r=2: [Edge23,Edge24,Edge25,Edge26,Edge27,Edge29,Edge30,Edge31,Edge32,Edge33]
  Placement = pos=(0,0,0) rot=(0,0,1;1.0472rad)
FEATURE [App::DocumentObjectGroup] Group011  label="6154 Duet Mounting"
  Group = -> [Cut456051,Fillet091,Fillet096,Chamfer006012121]
FEATURE [Part::Cylinder] Cylinder054099009137075  label="heatsink"
  Angle = 360
  AttacherType = Attacher::AttachEngine3D
  Height = 54
  Placement = pos=(0,0,-19) rot=(0,0,-1;0.523599rad)
  Radius = 8.8
FEATURE [Part::Cylinder] Cylinder054099009137076  label="mdf-screw-2"
  Angle = 360
  AttacherType = Attacher::AttachEngine3D
  Height = 54
  Placement = pos=(-20,11.5,-1) rot=(0,0,-1;0.523599rad)
  Radius = 1.7
FEATURE [Part::Feature] Cylinder054099009137077  label="mdf-screw-3"
  Placement = pos=(0,-23,-1) rot=(0,0,1;1.5708rad)
  shape: bbox 3.4 x 3.4 x 24 mm, 3 faces (baked)
FEATURE [Part::Feature] Cylinder054099009137078  label="mdf-screw-1"
  Placement = pos=(20,11.5,-1) rot=(0,0,1;3.66519rad)
  shape: bbox 3.4 x 3.4 x 24 mm, 3 faces (baked)
FEATURE [Part::Cylinder] Cylinder054099009137079  label="heatsink-clamp-screw-2"
  Angle = 360
  AttacherType = Attacher::AttachEngine3D
  Height = 24
  Placement = pos=(-2.9,-11.7,-1) rot=(0,0,-1;0.523599rad)
  Radius = 1.7
FEATURE [Part::Cylinder] Cylinder054099009137080  label="heatsink-clamp-screw-1"
  Angle = 360
  AttacherType = Attacher::AttachEngine3D
  Height = 24
  Placement = pos=(11.55,3.3,-13) rot=(0,0,-1;0.523599rad)
  Radius = 1.7
FEATURE [Part::Box] Box112015002017004007004038086003009003088019011047  label="fan-flow-box"
  AttacherType = Attacher::AttachEngine3D
  Height = 13
  Length = 18.5
  Placement = pos=(8.5,9,3) rot=(0,0,1;0rad)
  Width = 12.5
FEATURE [Part::Box] Box112015002017004007004038086003009003088019011048  label="fan-body"
  AttacherType = Attacher::AttachEngine3D
  Height = 20
  Length = 63
  Placement = pos=(-34.7,7.7,9) rot=(0,0,1;0rad)
  Width = 15
FEATURE [Part::Cylinder] Cylinder054099009137081  label="fan-bolt-tap-hole"
  Angle = 360
  AttacherType = Attacher::AttachEngine3D
  Height = 20
  Placement = pos=(-19.2,13,21.3) rot=(1,0,0;1.5708rad)
  Radius = 1.4
FEATURE [Part::Cylinder] Cylinder054099009137082  label="fan-bolt-clearance-hole"
  Angle = 360
  AttacherType = Attacher::AttachEngine3D
  Height = 20
  Placement = pos=(-19.2,31,21.3) rot=(1,0,0;1.5708rad)
  Radius = 1.7
FEATURE [Part::Cylinder] Cylinder054099009137083  label="m3-nut-cylinder"
  Angle = 360
  AttacherType = Attacher::AttachEngine3D
  Height = 8
  Placement = pos=(0,0,131) rot=(0,0,1;0rad)
  Radius = 5
FEATURE [Part::Box] Box112015002017004007004038086003009003088019011049  label="m3-nut-flat-1"
  AttacherType = Attacher::AttachEngine3D
  Height = 10
  Length = 10
  Placement = pos=(-5,2.85,130) rot=(0,0,1;0rad)
  Width = 10
FEATURE [Part::Feature] Box112015002017004007004038086003009003088019011050  label="m3-nut-flat-2"
  Placement = pos=(-4.96817,-2.90513,130) rot=(0,0,1;1.0472rad)
  shape: bbox 13.66 x 13.66 x 10 mm, 6 faces (baked)
FEATURE [Part::Feature] Box112015002017004007004038086003009003088019011051  label="m3-nut-flat-3"
  Placement = pos=(0.0318276,-5.75513,130) rot=(0,0,1;2.0944rad)
  shape: bbox 13.66 x 13.66 x 10 mm, 6 faces (baked)
FEATURE [Part::Feature] Box112015002017004007004038086003009003088019011052  label="m3-nut-flat-4"
  Placement = pos=(5,-2.85,130) rot=(0,0,1;3.14159rad)
  shape: bbox 10 x 10 x 10 mm, 6 faces (baked)
FEATURE [Part::Feature] Box112015002017004007004038086003009003088019011053  label="m3-nut-flat-5"
  Placement = pos=(4.96817,2.90513,130) rot=(0,0,-1;2.0944rad)
  shape: bbox 13.66 x 13.66 x 10 mm, 6 faces (baked)
FEATURE [Part::Feature] Box112015002017004007004038086003009003088019011054  label="m3-nut-flat-6"
  Placement = pos=(-0.0318276,5.75513,130) rot=(0,0,-1;1.0472rad)
  shape: bbox 13.66 x 13.66 x 10 mm, 6 faces (baked)
FEATURE [Sketcher::SketchObject] Sketch001
  MapMode = 5
  sketch-geometry (28):
    g0: LineSegment StartX=11.005 StartY=16.347 StartZ=0 EndX=7.4963 EndY=16.347 EndZ=0
    g1: LineSegment StartX=7.4963 StartY=16.347 StartZ=0 EndX=4.64255 EndY=15.5049 EndZ=0
    g2: LineSegment StartX=4.64255 StartY=15.5049 StartZ=0 EndX=2.5841 EndY=14.2418 EndZ=0
    g3: LineSegment StartX=2.5841 StartY=14.2418 StartZ=0 EndX=1.18061 EndY=12.8383 EndZ=0
    g4: LineSegment StartX=1.18061 StartY=12.8383 StartZ=0 EndX=-3.96551 EndY=7.9261 EndZ=0
    g5: LineSegment StartX=-3.96551 StartY=7.9261 StartZ=0 EndX=-10.7023 EndY=2.59285 EndZ=0
    g6: LineSegment StartX=-10.7023 StartY=2.59285 StartZ=0 EndX=-19.2635 EndY=-2.45971 EndZ=0
    g7: LineSegment StartX=-19.2635 StartY=-2.45971 StartZ=0 EndX=-11.825 EndY=-15.5589 EndZ=0
    g8: LineSegment StartX=-11.825 StartY=-15.5589 StartZ=0 EndX=-8.69059 EndY=-13.7344 EndZ=0
    g9: LineSegment StartX=-8.69059 StartY=-13.7344 StartZ=0 EndX=-7.14675 EndY=-12.4245 EndZ=0
    g10: LineSegment StartX=-7.14675 StartY=-12.4245 StartZ=0 EndX=-6.16431 EndY=-11.2081 EndZ=0
    g11: LineSegment StartX=-6.16431 StartY=-11.2081 StartZ=0 EndX=-5.32222 EndY=-9.52393 EndZ=0
    g12: LineSegment StartX=-5.32222 StartY=-9.52393 StartZ=0 EndX=-4.24621 EndY=-8.72862 EndZ=0
    g13: LineSegment StartX=-4.24621 StartY=-8.72862 StartZ=0 EndX=-2.93629 EndY=-8.44792 EndZ=0
    g14: LineSegment StartX=-2.93629 StartY=-8.44792 StartZ=0 EndX=-1.8135 EndY=-8.58827 EndZ=0
    g15: LineSegment StartX=-1.8135 StartY=-8.58827 StartZ=0 EndX=-0.26966 EndY=-8.91575 EndZ=0
    g16: LineSegment StartX=-0.26966 StartY=-8.91575 StartZ=0 EndX=2.25662 EndY=-9.99176 EndZ=0
    g17: LineSegment StartX=2.25662 StartY=-9.99176 StartZ=0 EndX=3.23906 EndY=-10.5064 EndZ=0
    g18: LineSegment StartX=3.23906 StartY=-10.5064 StartZ=0 EndX=11.66 EndY=-15.5121 EndZ=0
    g19: LineSegment StartX=11.66 StartY=-15.5121 StartZ=0 EndX=19.3324 EndY=-2.36614 EndZ=0
    g20: LineSegment StartX=19.3324 StartY=-2.36614 StartZ=0 EndX=14.9816 EndY=0 EndZ=0
    g21: LineSegment StartX=14.9816 StartY=0 StartZ=0 EndX=13.5313 EndY=0 EndZ=0
    g22: LineSegment StartX=13.5313 StartY=0 StartZ=0 EndX=10.9115 EndY=0 EndZ=0
    g23: LineSegment StartX=10.9115 StartY=0 StartZ=0 EndX=8.80622 EndY=1.23614 EndZ=0
    g24: LineSegment StartX=8.80622 StartY=1.23614 StartZ=0 EndX=8.29161 EndY=2.87354 EndZ=0
    g25: LineSegment StartX=8.29161 StartY=2.87354 StartZ=0 EndX=8.3384 EndY=3.8092 EndZ=0
    g26: LineSegment StartX=8.3384 StartY=3.8092 StartZ=0 EndX=11.66 EndY=3.8092 EndZ=0
    g27: LineSegment StartX=11.66 StartY=3.8092 StartZ=0 EndX=11.005 EndY=16.347 EndZ=0
  constraints (33):
    c: Horizontal(g0)
    c: Coincident(g0,g1)
    c: Coincident(g1,g2)
    c: Coincident(g2,g3)
    c: Coincident(g3,g4)
    c: Coincident(g4,g5)
    c: Coincident(g5,g6)
    c: Coincident(g6,g7)
    c: Coincident(g7,g8)
    c: Coincident(g8,g9)
    c: Coincident(g9,g10)
    c: Coincident(g10,g11)
    c: Coincident(g11,g12)
    c: Coincident(g12,g13)
    c: Coincident(g13,g14)
    c: Coincident(g14,g15)
    c: Coincident(g15,g16)
    c: Coincident(g16,g17)
    c: Coincident(g17,g18)
    c: Coincident(g18,g19)
    c: Coincident(g19,g20)
    c: PointOnObject(g20,g-1)
    c: Coincident(g20,g21)
    c: PointOnObject(g21,g-1)
    c: Coincident(g21,g22)
    c: PointOnObject(g22,g-1)
    c: Coincident(g22,g23)
    c: Coincident(g23,g24)
    c: Coincident(g24,g25)
    c: Coincident(g25,g26)
    c: Horizontal(g26)
    c: Coincident(g26,g27)
    c: Coincident(g27,g0)
FEATURE [Part::Extrusion] Extrude003
  Base = -> Sketch001
  Dir = (0,0,20)
  DirMode = 0
  FaceMakerClass = Part::FaceMakerExtrusion
  LengthFwd = 0
  LengthRev = 0
  Placement = pos=(0,0,-9) rot=(0,0,1;0rad)
  Solid = true
  Symmetric = false
FEATURE [Part::Box] Box112015002017004007004038086003009003088019011055  label="duct-chop-cube-1"
  AttacherType = Attacher::AttachEngine3D
  Height = 33
  Length = 18.5
  Placement = pos=(8.5,3,-15) rot=(0,0,1;0rad)
  Width = 20.5
FEATURE [Part::Cylinder] Cylinder054099009137084  label="main-cylinder"
  Angle = 360
  AttacherType = Attacher::AttachEngine3D
  Height = 14
  Placement = pos=(0,0,0) rot=(0,0,-1;0.523599rad)
  Radius = 38
FEATURE [Part::Box] Box112015002017004007004038086003009003088019011056  label="fan-outlet-surround"
  AttacherType = Attacher::AttachEngine3D
  Height = 4
  Length = 29.5
  Placement = pos=(0,5,13) rot=(0,0,1;0rad)
  Width = 19
FEATURE [Part::Box] Box112015002017004007004038086003009003088019011057  label="fan-bracket-1"
  AttacherType = Attacher::AttachEngine3D
  Height = 13
  Length = 20
  Placement = pos=(-26,0,13) rot=(0,0,1;0rad)
  Width = 26
FEATURE [Part::Cylinder] Cylinder054099009137085  label="ball-slider-clamp-hole006"
  Angle = 360
  AttacherType = Attacher::AttachEngine3D
  Height = 30
  Placement = pos=(0,47,7) rot=(0.57735,0.57735,-0.57735;2.0944rad)
  Radius = 1.4
FEATURE [Part::Box] Box112015002017004007004038086003009003088019011058  label="Cube329"
  AttacherType = Attacher::AttachEngine3D
  Height = 2
  Length = 2
  Placement = pos=(-24,-15,-130) rot=(0,0,1;0rad)
  Width = 30
FEATURE [Part::Box] Box112015002017004007004038086003009003088019011059  label="Cube330"
  AttacherType = Attacher::AttachEngine3D
  Height = 2
  Length = 2
  Placement = pos=(-24,-15,-118) rot=(0,0,1;0rad)
  Width = 30
FEATURE [Part::Box] Box112015002017004007004038086003009003088019011060  label="big-flat-chop-1"
  AttacherType = Attacher::AttachEngine3D
  Height = 50
  Length = 80
  Placement = pos=(-40,106,-10) rot=(0,0,-1;1.5708rad)
  Width = 80
FEATURE [Part::Box] Box112015002017004007004038086003009003088019011063  label="Cube332"
  AttacherType = Attacher::AttachEngine3D
  Height = 10
  Length = 4
  Placement = pos=(-24,-32.3,-130) rot=(0,0,1;0rad)
  Width = 4
FEATURE [Part::Box] Box112015002017004007004038086003009003088019011064  label="Cube333"
  AttacherType = Attacher::AttachEngine3D
  Height = 10
  Length = 20
  Placement = pos=(-40,-37,-130) rot=(0,0,1;0rad)
  Width = 6
FEATURE [Part::MultiFuse] Fusion051010010012015014088020103
  Shapes = -> [Box112015002017004007004038086003009003088019011063,Box112015002017004007004038086003009003088019011064]
FEATURE [Part::Chamfer] Chamfer006012122  label="snap-tab-c002"
  Base = -> Fusion051010010012015014088020103
  Edges = 1 edges r=4: [Edge27]
FEATURE [Part::Chamfer] Chamfer006012123  label="snap-tab-c003"
  Base = -> Fusion051010010012015014088020103
  Edges = 1 edges r=4: [Edge27]
FEATURE [Part::Mirroring] Part__Mirroring005072  label="snap-tab-c (Mirror #57)001"
  Base = (0,0,0)
  Normal = (0,1,0)
  Source = -> Chamfer006012122
FEATURE [Part::MultiFuse] Fusion051010010012015014088020104  label="hot-end-snap-tabs001"
  Shapes = -> [Chamfer006012123,Part__Mirroring005072]
FEATURE [Part::Chamfer] Chamfer006012124
  Base = -> Box112015002017004007004038086003009003088019011059
  Edges = 1 edges r=1.7: [Edge4]
FEATURE [Part::Chamfer] Chamfer006012125
  Base = -> Box112015002017004007004038086003009003088019011058
  Edges = 1 edges r=1.7: [Edge2]
FEATURE [Part::MultiFuse] Fusion051010010012015014088020105  label="hot-end-ball-mounts-001"
  Placement = pos=(0,4,130) rot=(0,0,-1;1.5708rad)
  Shapes = -> [Chamfer006012125,Chamfer006012124,Fusion051010010012015014088020104]
FEATURE [Part::Cylinder] Cylinder054099009137086  label="cable-tie-hole001"
  Angle = 360
  AttacherType = Attacher::AttachEngine3D
  Height = 500
  Placement = pos=(-31,12,-214) rot=(0,0,1;0rad)
  Radius = 1.5
FEATURE [Part::Box] Box112015002017004007004038086003009003088019011065  label="duct-chop-cube-002"
  AttacherType = Attacher::AttachEngine3D
  Height = 33
  Length = 20.5
  Placement = pos=(4,-29,-15) rot=(0,0,-1;0.523599rad)
  Width = 36.5
FEATURE [Part::Box] Box112015002017004007004038086003009003088019011066  label="duct-chop-cube-003"
  AttacherType = Attacher::AttachEngine3D
  Height = 33
  Length = 18.5
  Placement = pos=(-27,-26,-15) rot=(0,0,1;0.523599rad)
  Width = 20.5
FEATURE [Part::Box] Box112015002017004007004038086003009003088019011067  label="duct-blank"
  AttacherType = Attacher::AttachEngine3D
  Height = 21
  Length = 37
  Placement = pos=(-3,-32,-10) rot=(0,0,1;0.523599rad)
  Width = 41
FEATURE [Part::Chamfer] Chamfer006012126
  Base = -> Box112015002017004007004038086003009003088019011067
  Edges = 1 edges r=18: [Edge1]
FEATURE [Part::Cylinder] Cylinder054099009137087  label="Cylinder054099009137114"
  Angle = 360
  AttacherType = Attacher::AttachEngine3D
  Height = 50
  Placement = pos=(-68,85,-20) rot=(0,0,1;0rad)
  Radius = 100
FEATURE [Part::Cut] Cut456210
  Base = -> Chamfer006012126
  Tool = -> Cylinder054099009137087
FEATURE [Part::Box] Box112015002017004007004038086003009003088019011068  label="duct-chop-cube-004"
  AttacherType = Attacher::AttachEngine3D
  Height = 33
  Length = 18.5
  Placement = pos=(2.5,16.5,-15) rot=(0,0,1;0rad)
  Width = 20.5
FEATURE [Part::Cut] Cut456211
  Base = -> Cut456210
  Tool = -> Box112015002017004007004038086003009003088019011068
FEATURE [Part::Fillet] Fillet097
  Base = -> Cut456211
  Edges = 1 edges r=10: [Edge10]
FEATURE [Part::Cut] Cut456212
  Base = -> Fillet097
  Tool = -> Box112015002017004007004038086003009003088019011065
FEATURE [Part::Box] Box112015002017004007004038086003009003088019011069  label="duct-chop-cube-005"
  AttacherType = Attacher::AttachEngine3D
  Height = 33
  Length = 18.5
  Placement = pos=(9.5,3,-15) rot=(0,0,-1;0.488692rad)
  Width = 20.5
FEATURE [Part::Cylinder] Cylinder054099009137088  label="heatsink-clamp-screw-003"
  Angle = 360
  AttacherType = Attacher::AttachEngine3D
  Height = 44
  Placement = pos=(11.55,3.3,-21) rot=(0,0,-1;0.523599rad)
  Radius = 3
FEATURE [Part::Cylinder] Cylinder054099009137089  label="heatsink-clamp-screw-004"
  Angle = 360
  AttacherType = Attacher::AttachEngine3D
  Height = 44
  Placement = pos=(-2.9,-11.7,-22) rot=(0,0,-1;0.523599rad)
  Radius = 3
FEATURE [Part::Cut] Cut456213
  Base = -> Cut456212
  Tool = -> Box112015002017004007004038086003009003088019011055
FEATURE [Part::Cut] Cut456214
  Base = -> Cut456213
  Tool = -> Box112015002017004007004038086003009003088019011069
FEATURE [Part::Cut] Cut456215
  Base = -> Cut456214
  Tool = -> Cylinder054099009137088
FEATURE [Part::Chamfer] Chamfer006012127
  Base = -> Cut456215
  Edges = 1 edges r=2.5: [Edge17]
FEATURE [Part::Cut] Cut456216
  Base = -> Chamfer006012127
  Tool = -> Box112015002017004007004038086003009003088019011066
FEATURE [Part::Box] Box112015002017004007004038086003009003088019011070  label="duct-chop-cube-006"
  AttacherType = Attacher::AttachEngine3D
  Height = 33
  Length = 41.5
  Placement = pos=(-16,-42,-15) rot=(0,0,-1;0.523599rad)
  Width = 36.5
FEATURE [Part::Fillet] Fillet098
  Base = -> Box112015002017004007004038086003009003088019011070
  Edges = 1 edges r=8: [Edge3]
  Placement = pos=(-5,3,0) rot=(0,0,1;0rad)
FEATURE [Part::Fillet] Fillet099
  Base = -> Box112015002017004007004038086003009003088019011070
  Edges = 1 edges r=8: [Edge3]
  Placement = pos=(5,2,0) rot=(0,0,-1;0.523599rad)
FEATURE [Part::Cut] Cut456217
  Base = -> Cut456216
  Tool = -> Fillet098
FEATURE [Part::Cut] Cut456218
  Base = -> Cut456217
  Tool = -> Fillet099
FEATURE [Part::Cut] Cut456219
  Base = -> Cut456218
  Tool = -> Cylinder054099009137089
FEATURE [Part::Chamfer] Chamfer006012128
  Base = -> Cut456219
  Edges = 1 edges r=3: [Edge23]
FEATURE [Part::Chamfer] Chamfer006012129
  Base = -> Chamfer006012128
  Edges = 1 edges r=3: [Edge22]
FEATURE [Part::Fillet] Fillet100
  Base = -> Chamfer006012129
  Edges = 1 edges r=10: [Edge37]
FEATURE [Part::Fillet] Fillet101  label="air-duct-1"
  Base = -> Fillet100
  Edges = 1 edges r=10: [Edge43]
FEATURE [Part::MultiFuse] Fusion051010010012015014088020106  label="m3-nut-flats"
  Shapes = -> [Box112015002017004007004038086003009003088019011049,Box112015002017004007004038086003009003088019011050,Box112015002017004007004038086003009003088019011051,Box112015002017004007004038086003009003088019011052,Box112015002017004007004038086003009003088019011053,Box112015002017004007004038086003009003088019011054]
FEATURE [Part::Cut] Cut456220  label="m3-nut"
  Base = -> Cylinder054099009137083
  Placement = pos=(-2.9,-11.7,-136.7) rot=(0,0,1;0rad)
  Tool = -> Fusion051010010012015014088020106
FEATURE [Part::MultiFuse] Fusion051010010012015014088020107  label="fan-support-1"
  Shapes = -> [Box112015002017004007004038086003009003088019011056,Box112015002017004007004038086003009003088019011057]
FEATURE [Part::Cut] Cut456221  label="fan-surround"
  Base = -> Fusion051010010012015014088020107
  Tool = -> Box112015002017004007004038086003009003088019011048
FEATURE [Part::MultiFuse] Fusion051010010012015014088020108  label="body+fan-1"
  Shapes = -> [Cylinder054099009137084,Cut456221]
FEATURE [Part::MultiFuse] Fusion051010010012015014088020109  label="fan-bolt"
  Shapes = -> [Cylinder054099009137081,Cylinder054099009137082]
FEATURE [Part::Cut] Cut456222  label="body+fan-2"
  Base = -> Fusion051010010012015014088020108
  Tool = -> Fusion051010010012015014088020109
FEATURE [Part::Box] Box112015002017004007004038086003009003088019011071  label="fan-flow-box001"
  AttacherType = Attacher::AttachEngine3D
  Height = 8
  Length = 19.5
  Placement = pos=(7.5,3,3) rot=(0,0,1;0rad)
  Width = 12.5
FEATURE [Part::Box] Box112015002017004007004038086003009003088019011072  label="big-flat-chop-002"
  AttacherType = Attacher::AttachEngine3D
  Height = 50
  Length = 80
  Placement = pos=(-71.7987,-87.641,-10) rot=(0,0,1;0.523599rad)
  Width = 80
FEATURE [Part::Box] Box112015002017004007004038086003009003088019011073  label="big-flat-chop-003"
  AttacherType = Attacher::AttachEngine3D
  Height = 50
  Length = 80
  Placement = pos=(111.799,-18.359,-10) rot=(0,0,1;2.61799rad)
  Width = 80
FEATURE [Part::MultiFuse] Fusion051010010012015014088020110  label="120-flats"
  Shapes = -> [Box112015002017004007004038086003009003088019011072,Box112015002017004007004038086003009003088019011073,Box112015002017004007004038086003009003088019011060]
FEATURE [Part::Cut] Cut456223  label="body-with-flats"
  Base = -> Cut456222
  Tool = -> Fusion051010010012015014088020110
FEATURE [Part::MultiFuse] Fusion051010010012015014088020111  label="fan-flow-boxes"
  Shapes = -> [Box112015002017004007004038086003009003088019011071,Box112015002017004007004038086003009003088019011047]
FEATURE [Part::MultiFuse] Fusion051010010012015014088020112
  Shapes = -> [Fusion051010010012015014088020111,Fillet101]
FEATURE [Part::Fillet] Fillet102  label="duct"
  Base = -> Fusion051010010012015014088020112
  Edges = 1 edges r=6: [Edge57]
FEATURE [Part::Cut] Cut456224  label="body-duct"
  Base = -> Cut456223
  Tool = -> Fillet102
FEATURE [Part::Cut] Cut456226  label="m3-nut001"
  Base = -> Cylinder054099009137083
  Placement = pos=(11.55,3.3,-136.7) rot=(0,0,1;0rad)
  Tool = -> Fusion051010010012015014088020106
FEATURE [Part::MultiFuse] Fusion051010010012015014088020115  label="m3-nuts"
  Shapes = -> [Cut456226,Cut456220]
FEATURE [Part::MultiFuse] Fusion051010010012015014088020116  label="all-small-holes"
  Shapes = -> [Fusion051010010012015014088020115,Cylinder054099009137086,Cylinder054099009137076,Cylinder054099009137078,Cylinder054099009137077,Cylinder054099009137079,Cylinder054099009137080]
FEATURE [Part::Cut] Cut456227  label="body-all-holes"
  Base = -> Cut456224
  Tool = -> Fusion051010010012015014088020116
FEATURE [Part::Chamfer] Chamfer006012130
  Base = -> Cut456227
  Edges = 2 edges r=8: [Edge199,Edge216]
FEATURE [Part::Fillet] Fillet103
  Base = -> Chamfer006012130
  Edges = 2 edges r=5: [Edge9,Edge117]
FEATURE [Part::Cut] Cut456228  label="final-body"
  Base = -> Fillet103
  Tool = -> Cylinder054099009137075
FEATURE [Part::MultiFuse] Fusion051010010012015014088020117  label="hot-end-ball-mounts-002"
  Placement = pos=(3.4641,-2,130) rot=(0,0,1;2.61799rad)
  Shapes = -> [Chamfer006012125,Chamfer006012124,Fusion051010010012015014088020104]
FEATURE [Part::MultiFuse] Fusion051010010012015014088020118  label="hot-end-ball-mounts-003"
  Placement = pos=(-3.4641,-2,130) rot=(0,0,1;0.523599rad)
  Shapes = -> [Chamfer006012125,Chamfer006012124,Fusion051010010012015014088020104]
FEATURE [Part::Cylinder] Cylinder054099009137090  label="ball-slider-clamp-hole007"
  Angle = 360
  AttacherType = Attacher::AttachEngine3D
  Height = 30
  Placement = pos=(-40.7032,-23.5,7) rot=(-0.250563,0.935113,0.250563;1.63783rad)
  Radius = 1.4
FEATURE [Part::Cylinder] Cylinder054099009137091  label="ball-slider-clamp-hole008"
  Angle = 360
  AttacherType = Attacher::AttachEngine3D
  Height = 30
  Placement = pos=(40.7032,-23.5,7) rot=(0.694747,-0.186157,-0.694747;3.50969rad)
  Radius = 1.4
FEATURE [Part::MultiFuse] Fusion051010010012015014088020119  label="ball-mount-clamp-holes"
  Shapes = -> [Cylinder054099009137091,Cylinder054099009137090,Cylinder054099009137085]
FEATURE [Part::MultiFuse] Fusion051010010012015014088020120  label="ball-clamp-runners"
  Shapes = -> [Fusion051010010012015014088020118,Fusion051010010012015014088020117,Fusion051010010012015014088020105]
FEATURE [Part::MultiFuse] Fusion051010010012015014088020121
  Shapes = -> [Cut456228,Fusion051010010012015014088020120]
FEATURE [Part::Cut] Cut456229  label="hot-end001x"
  Base = -> Fusion051010010012015014088020121
  Tool = -> Fusion051010010012015014088020119
FEATURE [App::DocumentObjectGroup] Group002  label="Experiments"
  Group = -> [Chamfer006012003,Cut294,Cut456037,Fillet055,Fillet057,Group024,Cut456135,Group021,Chamfer006012076,Cut456197,Cut456229,Group022]
FEATURE [Part::Cylinder] Cylinder054099009137092  label="heatsink001"
  Angle = 360
  AttacherType = Attacher::AttachEngine3D
  Height = 54
  Placement = pos=(0,0,-19) rot=(0,0,-1;0.523599rad)
  Radius = 8.8
FEATURE [Part::Cylinder] Cylinder054099009137093  label="mdf-screw-004"
  Angle = 360
  AttacherType = Attacher::AttachEngine3D
  Height = 54
  Placement = pos=(-20,11.5,-1) rot=(0,0,-1;0.523599rad)
  Radius = 1.7
FEATURE [Part::Feature] Cylinder054099009137094  label="mdf-screw-005"
  Placement = pos=(0,-23,-1) rot=(0,0,1;1.5708rad)
  shape: bbox 3.4 x 3.4 x 24 mm, 3 faces (baked)
FEATURE [Part::Feature] Cylinder054099009137095  label="mdf-screw-006"
  Placement = pos=(20,11.5,-1) rot=(0,0,1;3.66519rad)
  shape: bbox 3.4 x 3.4 x 24 mm, 3 faces (baked)
FEATURE [Part::Cylinder] Cylinder054099009137096  label="heatsink-clamp-screw-005"
  Angle = 360
  AttacherType = Attacher::AttachEngine3D
  Height = 24
  Placement = pos=(-2.9,-11.7,-1) rot=(0,0,-1;0.523599rad)
  Radius = 1.7
FEATURE [Part::Cylinder] Cylinder054099009137097  label="heatsink-clamp-screw-006"
  Angle = 360
  AttacherType = Attacher::AttachEngine3D
  Height = 24
  Placement = pos=(11.55,3.3,-13) rot=(0,0,-1;0.523599rad)
  Radius = 1.7
FEATURE [Part::Box] Box112015002017004007004038086003009003088019011074  label="fan-flow-box002"
  AttacherType = Attacher::AttachEngine3D
  Height = 13
  Length = 18.5
  Placement = pos=(8.5,9,3) rot=(0,0,1;0rad)
  Width = 12.5
FEATURE [Part::Box] Box112015002017004007004038086003009003088019011075  label="fan-body001"
  AttacherType = Attacher::AttachEngine3D
  Height = 20
  Length = 63
  Placement = pos=(-34.7,7.7,9) rot=(0,0,1;0rad)
  Width = 15
FEATURE [Part::Cylinder] Cylinder054099009137098  label="fan-bolt-tap-hole001"
  Angle = 360
  AttacherType = Attacher::AttachEngine3D
  Height = 20
  Placement = pos=(-19.2,13,21.3) rot=(1,0,0;1.5708rad)
  Radius = 1.4
FEATURE [Part::Cylinder] Cylinder054099009137099  label="fan-bolt-clearance-hole001"
  Angle = 360
  AttacherType = Attacher::AttachEngine3D
  Height = 20
  Placement = pos=(-19.2,31,21.3) rot=(1,0,0;1.5708rad)
  Radius = 1.7
FEATURE [Part::Cylinder] Cylinder054099009137100  label="m3-nut-cylinder001"
  Angle = 360
  AttacherType = Attacher::AttachEngine3D
  Height = 8
  Placement = pos=(0,0,131) rot=(0,0,1;0rad)
  Radius = 5
FEATURE [Part::Box] Box112015002017004007004038086003009003088019011076  label="m3-nut-flat-007"
  AttacherType = Attacher::AttachEngine3D
  Height = 10
  Length = 10
  Placement = pos=(-5,2.85,130) rot=(0,0,1;0rad)
  Width = 10
FEATURE [Part::Feature] Box112015002017004007004038086003009003088019011077  label="m3-nut-flat-008"
  Placement = pos=(-4.96817,-2.90513,130) rot=(0,0,1;1.0472rad)
  shape: bbox 13.66 x 13.66 x 10 mm, 6 faces (baked)
FEATURE [Part::Feature] Box112015002017004007004038086003009003088019011078  label="m3-nut-flat-009"
  Placement = pos=(0.0318276,-5.75513,130) rot=(0,0,1;2.0944rad)
  shape: bbox 13.66 x 13.66 x 10 mm, 6 faces (baked)
FEATURE [Part::Feature] Box112015002017004007004038086003009003088019011079  label="m3-nut-flat-010"
  Placement = pos=(5,-2.85,130) rot=(0,0,1;3.14159rad)
  shape: bbox 10 x 10 x 10 mm, 6 faces (baked)
FEATURE [Part::Feature] Box112015002017004007004038086003009003088019011080  label="m3-nut-flat-011"
  Placement = pos=(4.96817,2.90513,130) rot=(0,0,-1;2.0944rad)
  shape: bbox 13.66 x 13.66 x 10 mm, 6 faces (baked)
FEATURE [Part::Feature] Box112015002017004007004038086003009003088019011081  label="m3-nut-flat-012"
  Placement = pos=(-0.0318276,5.75513,130) rot=(0,0,-1;1.0472rad)
  shape: bbox 13.66 x 13.66 x 10 mm, 6 faces (baked)
FEATURE [Part::Box] Box112015002017004007004038086003009003088019011082  label="duct-chop-cube-007"
  AttacherType = Attacher::AttachEngine3D
  Height = 33
  Length = 18.5
  Placement = pos=(8.5,3,-15) rot=(0,0,1;0rad)
  Width = 20.5
FEATURE [Part::Cylinder] Cylinder054099009137101  label="main-cylinder001"
  Angle = 360
  AttacherType = Attacher::AttachEngine3D
  Height = 14
  Placement = pos=(0,0,0) rot=(0,0,-1;0.523599rad)
  Radius = 38
FEATURE [Part::Box] Box112015002017004007004038086003009003088019011083  label="fan-outlet-surround001"
  AttacherType = Attacher::AttachEngine3D
  Height = 4
  Length = 29.5
  Placement = pos=(0,5,13) rot=(0,0,1;0rad)
  Width = 19
FEATURE [Part::Box] Box112015002017004007004038086003009003088019011084  label="fan-bracket-002"
  AttacherType = Attacher::AttachEngine3D
  Height = 13
  Length = 20
  Placement = pos=(-26,0,13) rot=(0,0,1;0rad)
  Width = 26
FEATURE [Part::Cylinder] Cylinder054099009137102  label="ball-slider-clamp-hole009"
  Angle = 360
  AttacherType = Attacher::AttachEngine3D
  Height = 30
  Placement = pos=(0,47,7) rot=(0.57735,0.57735,-0.57735;2.0944rad)
  Radius = 1.4
FEATURE [Part::Box] Box112015002017004007004038086003009003088019011085  label="Cube334"
  AttacherType = Attacher::AttachEngine3D
  Height = 2
  Length = 2
  Placement = pos=(-24,-15,-130) rot=(0,0,1;0rad)
  Width = 30
FEATURE [Part::Box] Box112015002017004007004038086003009003088019011086  label="Cube335"
  AttacherType = Attacher::AttachEngine3D
  Height = 2
  Length = 2
  Placement = pos=(-24,-15,-118) rot=(0,0,1;0rad)
  Width = 30
FEATURE [Part::Box] Box112015002017004007004038086003009003088019011087  label="big-flat-chop-004"
  AttacherType = Attacher::AttachEngine3D
  Height = 50
  Length = 80
  Placement = pos=(-40,106,-10) rot=(0,0,-1;1.5708rad)
  Width = 80
FEATURE [Part::Box] Box112015002017004007004038086003009003088019011088  label="Cube336"
  AttacherType = Attacher::AttachEngine3D
  Height = 10
  Length = 4
  Placement = pos=(-24,-32.3,-130) rot=(0,0,1;0rad)
  Width = 4
FEATURE [Part::Box] Box112015002017004007004038086003009003088019011089  label="Cube337"
  AttacherType = Attacher::AttachEngine3D
  Height = 10
  Length = 20
  Placement = pos=(-40,-37,-130) rot=(0,0,1;0rad)
  Width = 6
FEATURE [Part::MultiFuse] Fusion051010010012015014088020122
  Shapes = -> [Box112015002017004007004038086003009003088019011088,Box112015002017004007004038086003009003088019011089]
FEATURE [Part::Chamfer] Chamfer006012131  label="snap-tab-c004"
  Base = -> Fusion051010010012015014088020122
  Edges = 1 edges r=4: [Edge27]
FEATURE [Part::Chamfer] Chamfer006012132  label="snap-tab-c005"
  Base = -> Fusion051010010012015014088020122
  Edges = 1 edges r=4: [Edge27]
FEATURE [Part::Mirroring] Part__Mirroring005073  label="snap-tab-c (Mirror #57)002"
  Base = (0,0,0)
  Normal = (0,1,0)
  Source = -> Chamfer006012131
FEATURE [Part::MultiFuse] Fusion051010010012015014088020123  label="hot-end-snap-tabs002"
  Shapes = -> [Chamfer006012132,Part__Mirroring005073]
FEATURE [Part::Chamfer] Chamfer006012133
  Base = -> Box112015002017004007004038086003009003088019011086
  Edges = 1 edges r=1.7: [Edge4]
  Placement = pos=(0,4,130) rot=(0,0,-1;1.5708rad)
FEATURE [Part::Chamfer] Chamfer006012134
  Base = -> Box112015002017004007004038086003009003088019011085
  Edges = 1 edges r=1.7: [Edge2]
  Placement = pos=(0,4,130) rot=(0,0,-1;1.5708rad)
FEATURE [Part::Cylinder] Cylinder054099009137103  label="cable-tie-hole002"
  Angle = 360
  AttacherType = Attacher::AttachEngine3D
  Height = 500
  Placement = pos=(-31,12,-214) rot=(0,0,1;0rad)
  Radius = 1.5
FEATURE [Part::Box] Box112015002017004007004038086003009003088019011090  label="duct-chop-cube-008"
  AttacherType = Attacher::AttachEngine3D
  Height = 33
  Length = 20.5
  Placement = pos=(4,-29,-15) rot=(0,0,-1;0.523599rad)
  Width = 36.5
FEATURE [Part::Box] Box112015002017004007004038086003009003088019011091  label="duct-chop-cube-009"
  AttacherType = Attacher::AttachEngine3D
  Height = 33
  Length = 18.5
  Placement = pos=(-27,-26,-15) rot=(0,0,1;0.523599rad)
  Width = 20.5
FEATURE [Part::Box] Box112015002017004007004038086003009003088019011092  label="duct-blank001"
  AttacherType = Attacher::AttachEngine3D
  Height = 21
  Length = 37
  Placement = pos=(-3,-32,-10) rot=(0,0,1;0.523599rad)
  Width = 41
FEATURE [Part::Chamfer] Chamfer006012135
  Base = -> Box112015002017004007004038086003009003088019011092
  Edges = 1 edges r=18: [Edge1]
FEATURE [Part::Cylinder] Cylinder054099009137104  label="Cylinder054099009137132"
  Angle = 360
  AttacherType = Attacher::AttachEngine3D
  Height = 50
  Placement = pos=(-68,85,-20) rot=(0,0,1;0rad)
  Radius = 100
FEATURE [Part::Cut] Cut456230
  Base = -> Chamfer006012135
  Tool = -> Cylinder054099009137104
FEATURE [Part::Box] Box112015002017004007004038086003009003088019011093  label="duct-chop-cube-010"
  AttacherType = Attacher::AttachEngine3D
  Height = 33
  Length = 18.5
  Placement = pos=(2.5,16.5,-15) rot=(0,0,1;0rad)
  Width = 20.5
FEATURE [Part::Cut] Cut456231
  Base = -> Cut456230
  Tool = -> Box112015002017004007004038086003009003088019011093
FEATURE [Part::Fillet] Fillet104
  Base = -> Cut456231
  Edges = 1 edges r=10: [Edge10]
FEATURE [Part::Cut] Cut456232
  Base = -> Fillet104
  Tool = -> Box112015002017004007004038086003009003088019011090
FEATURE [Part::Box] Box112015002017004007004038086003009003088019011094  label="duct-chop-cube-011"
  AttacherType = Attacher::AttachEngine3D
  Height = 33
  Length = 18.5
  Placement = pos=(9.5,3,-15) rot=(0,0,-1;0.488692rad)
  Width = 20.5
FEATURE [Part::Cylinder] Cylinder054099009137105  label="heatsink-clamp-screw-007"
  Angle = 360
  AttacherType = Attacher::AttachEngine3D
  Height = 44
  Placement = pos=(11.55,3.3,-21) rot=(0,0,-1;0.523599rad)
  Radius = 3
FEATURE [Part::Cylinder] Cylinder054099009137106  label="heatsink-clamp-screw-008"
  Angle = 360
  AttacherType = Attacher::AttachEngine3D
  Height = 44
  Placement = pos=(-2.9,-11.7,-22) rot=(0,0,-1;0.523599rad)
  Radius = 3
FEATURE [Part::Cut] Cut456233
  Base = -> Cut456232
  Tool = -> Box112015002017004007004038086003009003088019011082
FEATURE [Part::Cut] Cut456234
  Base = -> Cut456233
  Tool = -> Box112015002017004007004038086003009003088019011094
FEATURE [Part::Cut] Cut456235
  Base = -> Cut456234
  Tool = -> Cylinder054099009137105
FEATURE [Part::Chamfer] Chamfer006012136
  Base = -> Cut456235
  Edges = 1 edges r=2.5: [Edge17]
FEATURE [Part::Cut] Cut456236
  Base = -> Chamfer006012136
  Tool = -> Box112015002017004007004038086003009003088019011091
FEATURE [Part::Box] Box112015002017004007004038086003009003088019011095  label="duct-chop-cube-012"
  AttacherType = Attacher::AttachEngine3D
  Height = 33
  Length = 41.5
  Placement = pos=(-16,-42,-15) rot=(0,0,-1;0.523599rad)
  Width = 36.5
FEATURE [Part::Fillet] Fillet105
  Base = -> Box112015002017004007004038086003009003088019011095
  Edges = 1 edges r=8: [Edge3]
  Placement = pos=(-5,3,0) rot=(0,0,1;0rad)
FEATURE [Part::Fillet] Fillet106
  Base = -> Box112015002017004007004038086003009003088019011095
  Edges = 1 edges r=8: [Edge3]
  Placement = pos=(5,2,0) rot=(0,0,-1;0.523599rad)
FEATURE [Part::Cut] Cut456237
  Base = -> Cut456236
  Tool = -> Fillet105
FEATURE [Part::Cut] Cut456238
  Base = -> Cut456237
  Tool = -> Fillet106
FEATURE [Part::Cut] Cut456239
  Base = -> Cut456238
  Tool = -> Cylinder054099009137106
FEATURE [Part::Chamfer] Chamfer006012137
  Base = -> Cut456239
  Edges = 1 edges r=3: [Edge23]
FEATURE [Part::Chamfer] Chamfer006012138
  Base = -> Chamfer006012137
  Edges = 1 edges r=3: [Edge22]
FEATURE [Part::Fillet] Fillet107
  Base = -> Chamfer006012138
  Edges = 1 edges r=10: [Edge37]
FEATURE [Part::Fillet] Fillet108  label="air-duct-002"
  Base = -> Fillet107
  Edges = 1 edges r=10: [Edge43]
FEATURE [Part::MultiFuse] Fusion051010010012015014088020124  label="m3-nut-flats001"
  Shapes = -> [Box112015002017004007004038086003009003088019011076,Box112015002017004007004038086003009003088019011077,Box112015002017004007004038086003009003088019011078,Box112015002017004007004038086003009003088019011079,Box112015002017004007004038086003009003088019011080,Box112015002017004007004038086003009003088019011081]
FEATURE [Part::Cut] Cut456240  label="m3-nut002"
  Base = -> Cylinder054099009137100
  Placement = pos=(-2.9,-11.7,-136.7) rot=(0,0,1;0rad)
  Tool = -> Fusion051010010012015014088020124
FEATURE [Part::MultiFuse] Fusion051010010012015014088020125  label="fan-support-002"
  Shapes = -> [Box112015002017004007004038086003009003088019011083,Box112015002017004007004038086003009003088019011084]
FEATURE [Part::Cut] Cut456241  label="fan-surround001"
  Base = -> Fusion051010010012015014088020125
  Tool = -> Box112015002017004007004038086003009003088019011075
FEATURE [Part::MultiFuse] Fusion051010010012015014088020126  label="body+fan-003"
  Shapes = -> [Cylinder054099009137101,Cut456241]
FEATURE [Part::MultiFuse] Fusion051010010012015014088020127  label="fan-bolt001"
  Shapes = -> [Cylinder054099009137098,Cylinder054099009137099]
FEATURE [Part::Cut] Cut456242  label="body+fan-004"
  Base = -> Fusion051010010012015014088020126
  Tool = -> Fusion051010010012015014088020127
FEATURE [Part::Box] Box112015002017004007004038086003009003088019011096  label="fan-flow-box003"
  AttacherType = Attacher::AttachEngine3D
  Height = 8
  Length = 19.5
  Placement = pos=(7.5,3,3) rot=(0,0,1;0rad)
  Width = 12.5
FEATURE [Part::Box] Box112015002017004007004038086003009003088019011097  label="big-flat-chop-005"
  AttacherType = Attacher::AttachEngine3D
  Height = 50
  Length = 80
  Placement = pos=(-71.7987,-87.641,-10) rot=(0,0,1;0.523599rad)
  Width = 80
FEATURE [Part::Box] Box112015002017004007004038086003009003088019011098  label="big-flat-chop-006"
  AttacherType = Attacher::AttachEngine3D
  Height = 50
  Length = 80
  Placement = pos=(111.799,-18.359,-10) rot=(0,0,1;2.61799rad)
  Width = 80
FEATURE [Part::MultiFuse] Fusion051010010012015014088020128  label="120-flats001"
  Shapes = -> [Box112015002017004007004038086003009003088019011097,Box112015002017004007004038086003009003088019011098,Box112015002017004007004038086003009003088019011087]
FEATURE [Part::Cut] Cut456243  label="body-with-flats001"
  Base = -> Cut456242
  Tool = -> Fusion051010010012015014088020128
FEATURE [Part::MultiFuse] Fusion051010010012015014088020129  label="fan-flow-boxes001"
  Shapes = -> [Box112015002017004007004038086003009003088019011096,Box112015002017004007004038086003009003088019011074]
FEATURE [Part::MultiFuse] Fusion051010010012015014088020130
  Shapes = -> [Fusion051010010012015014088020129,Fillet108]
FEATURE [Part::Fillet] Fillet109  label="duct001"
  Base = -> Fusion051010010012015014088020130
  Edges = 1 edges r=6: [Edge57]
FEATURE [Part::Cut] Cut456244  label="body-duct001"
  Base = -> Cut456243
  Tool = -> Fillet109
FEATURE [Part::Cut] Cut456245  label="m3-nut003"
  Base = -> Cylinder054099009137100
  Placement = pos=(11.55,3.3,-136.7) rot=(0,0,1;0rad)
  Tool = -> Fusion051010010012015014088020124
FEATURE [Part::MultiFuse] Fusion051010010012015014088020131  label="m3-nuts001"
  Shapes = -> [Cut456245,Cut456240]
FEATURE [Part::MultiFuse] Fusion051010010012015014088020132  label="all-small-holes001"
  Shapes = -> [Fusion051010010012015014088020131,Cylinder054099009137103,Cylinder054099009137093,Cylinder054099009137095,Cylinder054099009137094,Cylinder054099009137096,Cylinder054099009137097]
FEATURE [Part::Cut] Cut456246  label="body-all-holes001"
  Base = -> Cut456244
  Tool = -> Fusion051010010012015014088020132
FEATURE [Part::Chamfer] Chamfer006012139
  Base = -> Cut456246
  Edges = 2 edges r=8: [Edge199,Edge216]
FEATURE [Part::Fillet] Fillet110
  Base = -> Chamfer006012139
  Edges = 2 edges r=5: [Edge9,Edge117]
FEATURE [Part::Cut] Cut456247  label="final-body001"
  Base = -> Fillet110
  Tool = -> Cylinder054099009137092
FEATURE [Part::MultiFuse] Fusion051010010012015014088020133  label="hot-end-ball-mounts-004"
  Placement = pos=(-3.4641,-2,130) rot=(0,0,1;0.523599rad)
  Shapes = -> [Chamfer006012134,Chamfer006012133,Fusion051010010012015014088020123]
FEATURE [App::DocumentObjectGroup] Group  label="Construction"
  Group = -> [Cylinder054033,Cylinder054028,Box112015002017004007004038040,Shape,Circle,Shape001,Circle001,Circle002,Shape002,Shape003,Shape004,Shape005,Shape006,Shape007,Face004,Shape008,Shape009,Shape010,Shape011,Circle004,Shape012,Cut359,Circle006,Shape022,Shape023,Shape024,Shape025,Shape026,Shape027,Shape028,Shape032,Shape033,Shape034,Shape035,Shape036,Face013,Face014,Face011,Face012,+17 more]
FEATURE [Part::Cylinder] Cylinder054099009137107  label="ball-slider-clamp-hole010"
  Angle = 360
  AttacherType = Attacher::AttachEngine3D
  Height = 30
  Placement = pos=(-40.7032,-23.5,7) rot=(-0.250563,0.935113,0.250563;1.63783rad)
  Radius = 1.4
FEATURE [Part::Cylinder] Cylinder054099009137108  label="ball-slider-clamp-hole011"
  Angle = 360
  AttacherType = Attacher::AttachEngine3D
  Height = 30
  Placement = pos=(40.7032,-23.5,7) rot=(0.694747,-0.186157,-0.694747;3.50969rad)
  Radius = 1.4
FEATURE [Part::MultiFuse] Fusion051010010012015014088020134  label="ball-mount-clamp-holes001"
  Shapes = -> [Cylinder054099009137108,Cylinder054099009137107,Cylinder054099009137102]
FEATURE [Part::Box] Box112015002017004007004038086003009003088019011099  label="Cube338"
  AttacherType = Attacher::AttachEngine3D
  Height = 2
  Length = 2
  Placement = pos=(-24,-15,-130) rot=(0,0,1;0rad)
  Width = 30
FEATURE [Part::Box] Box112015002017004007004038086003009003088019011100  label="Cube339"
  AttacherType = Attacher::AttachEngine3D
  Height = 2
  Length = 2
  Placement = pos=(-24,-15,-118) rot=(0,0,1;0rad)
  Width = 30
FEATURE [Part::Chamfer] Chamfer006012140
  Base = -> Box112015002017004007004038086003009003088019011100
  Edges = 1 edges r=1.7: [Edge4]
  Placement = pos=(0,4,130) rot=(0,0,-1;1.5708rad)
FEATURE [Part::Chamfer] Chamfer006012141
  Base = -> Box112015002017004007004038086003009003088019011099
  Edges = 1 edges r=1.7: [Edge2]
  Placement = pos=(0,4,130) rot=(0,0,-1;1.5708rad)
FEATURE [Part::MultiFuse] Fusion051010010012015014088020135  label="ball-mount-slide-rails"
  Placement = pos=(0,0,0) rot=(0,0,1;2.0944rad)
  Shapes = -> [Chamfer006012140,Chamfer006012141]
FEATURE [Part::MultiFuse] Fusion051010010012015014088020136  label="ball-mount-slide-rails001"
  Placement = pos=(0,0,0) rot=(0,0,1;4.18879rad)
  Shapes = -> [Chamfer006012140,Chamfer006012141]
FEATURE [Part::MultiFuse] Fusion051010010012015014088020137  label="ball-mount-slide-rails002"
  Shapes = -> [Chamfer006012140,Chamfer006012141]
FEATURE [Part::MultiFuse] Fusion051010010012015014088020138  label="all-ball-slide-rails"
  Shapes = -> [Fusion051010010012015014088020135,Fusion051010010012015014088020136,Fusion051010010012015014088020137]
FEATURE [Part::MultiFuse] Fusion051010010012015014088020139  label="body-with-rails"
  Shapes = -> [Cut456247,Fusion051010010012015014088020138]
FEATURE [Part::Cut] Cut456248  label="hot-end"
  Base = -> Fusion051010010012015014088020139
  Placement = pos=(-123,0,-200) rot=(0,0,1;0rad)
  Tool = -> Fusion051010010012015014088020134
FEATURE [App::DocumentObjectGroup] Group023  label="6174.1-Hot-End"
  Group = -> [Chamfer006012094,Chamfer006012095,Cut456248,Cylinder054099009137062]
FEATURE [App::DocumentObjectGroup] Group025  label="Legacy"
  Group = -> [Cut435]
FEATURE [Part::Box] Box112015002017004007004038086003009003088019011101  label="Cube340"
  AttacherType = Attacher::AttachEngine3D
  Height = 20
  Length = 39
  Placement = pos=(-36,-25,-264) rot=(0,0,1;0rad)
  Width = 50
FEATURE [Part::Box] Box112015002017004007004038086003009003088019011102  label="Cube341"
  AttacherType = Attacher::AttachEngine3D
  Height = 26
  Length = 39
  Placement = pos=(-8,-10,-267) rot=(0,0,1;0rad)
  Width = 20
FEATURE [Part::Cut] Cut456249
  Base = -> Box112015002017004007004038086003009003088019011101
  Tool = -> Box112015002017004007004038086003009003088019011102
FEATURE [Part::Box] Box112015002017004007004038086003009003088019011103  label="Cube342"
  AttacherType = Attacher::AttachEngine3D
  Height = 20
  Length = 39
  Placement = pos=(-11,-26,-278) rot=(0,0,1;0rad)
  Width = 53
FEATURE [Part::Cut] Cut456250
  Base = -> Cut456249
  Tool = -> Box112015002017004007004038086003009003088019011103
FEATURE [Part::Cylinder] Cylinder054099009137109  label="top-mount-007"
  Angle = 360
  AttacherType = Attacher::AttachEngine3D
  Height = 47
  Placement = pos=(-1,20,-267) rot=(0,0,1;0rad)
  Radius = 1.7
FEATURE [Part::Cylinder] Cylinder054099009137110  label="top-mount-008"
  Angle = 360
  AttacherType = Attacher::AttachEngine3D
  Height = 47
  Placement = pos=(-1,20,-267) rot=(0,0,1;0rad)
  Radius = 1.7
FEATURE [Part::Mirroring] Part__Mirroring005074  label="top-mount-006 (Mirror #22)001"
  Base = (0,0,0)
  Normal = (0,1,0)
  Source = -> Cylinder054099009137110
FEATURE [Part::Cut] Cut456251
  Base = -> Cut456250
  Tool = -> Cylinder054099009137109
FEATURE [Part::Cut] Cut456252
  Base = -> Cut456251
  Tool = -> Part__Mirroring005074
FEATURE [Part::Box] Box112015002017004007004038086003009003088019011104  label="Cube343"
  AttacherType = Attacher::AttachEngine3D
  Height = 26
  Length = 39
  Placement = pos=(-15,-10,-258) rot=(0,0,1;0rad)
  Width = 20
FEATURE [Part::Box] Box112015002017004007004038086003009003088019011105  label="Cube344"
  AttacherType = Attacher::AttachEngine3D
  Height = 32
  Length = 39
  Placement = pos=(-58,-35,-267) rot=(0,0,1;0rad)
  Width = 70
FEATURE [Part::Cut] Cut456253
  Base = -> Cut456252
  Tool = -> Box112015002017004007004038086003009003088019011104
FEATURE [Part::Cut] Cut456254
  Base = -> Cut456253
  Tool = -> Box112015002017004007004038086003009003088019011105
FEATURE [Part::Box] Box112015002017004007004038086003009003088019011106  label="Cube345"
  AttacherType = Attacher::AttachEngine3D
  Height = 26
  Length = 63
  Placement = pos=(-38,17,-268) rot=(0,0,1;0.20944rad)
  Width = 20
FEATURE [Part::Box] Box112015002017004007004038086003009003088019011107  label="Cube346"
  AttacherType = Attacher::AttachEngine3D
  Height = 26
  Length = 63
  Placement = pos=(-38,17,-268) rot=(0,0,1;0.20944rad)
  Width = 20
FEATURE [Part::Mirroring] Part__Mirroring005075  label="Cube166 (Mirror #23)001"
  Base = (0,0,0)
  Normal = (0,1,0)
  Source = -> Box112015002017004007004038086003009003088019011107
FEATURE [Part::Cut] Cut456255
  Base = -> Cut456254
  Tool = -> Box112015002017004007004038086003009003088019011106
FEATURE [Part::Cut] Cut456256
  Base = -> Cut456255
  Tool = -> Part__Mirroring005075
FEATURE [Part::Cylinder] Cylinder054099009137111  label="Cylinder054099009121"
  Angle = 360
  AttacherType = Attacher::AttachEngine3D
  Height = 21
  Placement = pos=(-23,4.1,-247) rot=(0,1,0;1.5708rad)
  Radius = 1.7
FEATURE [Part::Cylinder] Cylinder054099009137112  label="Cylinder054099009137133"
  Angle = 360
  AttacherType = Attacher::AttachEngine3D
  Height = 21
  Placement = pos=(-23,4.1,-248) rot=(0,1,0;1.5708rad)
  Radius = 1.7
FEATURE [Part::Mirroring] Part__Mirroring005076  label="Cylinder054099009026 (Mirror #25)001"
  Base = (0,0,0)
  Normal = (0,1,0)
  Placement = pos=(0,0,1) rot=(0,0,1;0rad)
  Source = -> Cylinder054099009137112
FEATURE [Part::Cut] Cut456257
  Base = -> Cut456256
  Tool = -> Cylinder054099009137111
FEATURE [Part::Cut] Cut456258  label="bed-mount-002"
  Base = -> Cut456257
  Tool = -> Part__Mirroring005076
FEATURE [Part::Feature] Face025
  shape: bbox 2.373 x 2e-07 x 2.456 mm, 1 faces, 0 solids (baked)
FEATURE [Part::Feature] Shape037
  shape: bbox 66.17 x 81 x 49.85 mm, 0 faces, 0 solids (baked)
FEATURE [Part::Sweep] Sweep028
  Frenet = false
  Sections = -> [Face025]
  Solid = true
  Spine = -> Shape037 [Edge1]
  Transition = 1
FEATURE [Part::Feature] Face026
  shape: bbox 2.373 x 2e-07 x 2.456 mm, 1 faces, 0 solids (baked)
FEATURE [Part::Feature] Shape038
  shape: bbox 66.17 x 81 x 49.85 mm, 0 faces, 0 solids (baked)
FEATURE [Part::Sweep] Sweep029
  Frenet = false
  Sections = -> [Face026]
  Solid = true
  Spine = -> Shape038 [Edge1]
  Transition = 1
FEATURE [Part::Mirroring] Part__Mirroring005077  label="Sweep023 (Mirror #27)001"
  Base = (0,0,0)
  Normal = (0,1,0)
  Source = -> Sweep029
FEATURE [Part::Cut] Cut456259
  Base = -> Cut456258
  Tool = -> Sweep028
FEATURE [Part::Cut] Cut456260  label="6159 bed mount-a"
  Base = -> Cut456259
  Tool = -> Part__Mirroring005077
FEATURE [Part::Cylinder] Cylinder054099009137113  label="Cylinder054099009137134"
  Angle = 360
  AttacherType = Attacher::AttachEngine3D
  Height = 6
  Placement = pos=(-3,0,-267) rot=(0,0,1;0rad)
  Radius = 5.7
FEATURE [Part::Cylinder] Cylinder054099009137114  label="Cylinder054099009137135"
  Angle = 360
  AttacherType = Attacher::AttachEngine3D
  Height = 4
  Placement = pos=(-3,0,-263) rot=(0,0,1;0rad)
  Radius = 8
FEATURE [Part::Box] Box112015002017004007004038086003009003088019011108  label="Cube347"
  AttacherType = Attacher::AttachEngine3D
  Height = 10
  Length = 10
  Placement = pos=(-20,-10,-266) rot=(0,0,1;0rad)
  Width = 20
FEATURE [Part::Box] Box112015002017004007004038086003009003088019011109  label="Cube348"
  AttacherType = Attacher::AttachEngine3D
  Height = 10
  Length = 10
  Placement = pos=(-17,-10,-271) rot=(0,0,1;0rad)
  Width = 20
FEATURE [Part::Cylinder] Cylinder054099009137115  label="Cylinder054099009137136"
  Angle = 360
  AttacherType = Attacher::AttachEngine3D
  Height = 10
  Placement = pos=(0,0,-267) rot=(0,0,1;0rad)
  Radius = 1.4
FEATURE [Part::Cone] Cone037  label="Cone023"
  Angle = 360
  AttacherType = Attacher::AttachEngine3D
  Height = 4.5
  Placement = pos=(-3,0,-265.5) rot=(0,0,1;0rad)
  Radius1 = 2
  Radius2 = 6.5
FEATURE [Part::MultiFuse] Fusion051010010012015014088020140
  Shapes = -> [Box112015002017004007004038086003009003088019011109,Box112015002017004007004038086003009003088019011108]
FEATURE [Part::Cut] Cut456261
  Base = -> Cylinder054099009137114
  Tool = -> Fusion051010010012015014088020140
FEATURE [Part::Cut] Cut456262
  Base = -> Cut456261
  Tool = -> Cylinder054099009137115
FEATURE [Part::MultiFuse] Fusion051010010012015014088020141
  Shapes = -> [Cylinder054099009137113,Cone037]
FEATURE [Part::Cut] Cut456099  label="bed-spring-retainer"
  Base = -> Cut456262
  Placement = pos=(-25,0,1) rot=(0,0,1;0rad)
  Tool = -> Fusion051010010012015014088020141
FEATURE [Part::Box] Box112015002017004007004038086003009003088019011110  label="Cube349"
  AttacherType = Attacher::AttachEngine3D
  Height = 3
  Length = 4
  Placement = pos=(-19,-10,-245) rot=(0,0,1;0rad)
  Width = 20
FEATURE [Part::Chamfer] Chamfer006012142
  Base = -> Box112015002017004007004038086003009003088019011110
  Edges = 2 edges r=2.5: [Edge10,Edge12]
FEATURE [Part::MultiFuse] Fusion051010010012015014088020142  label="6159.1 bed mount"
  Shapes = -> [Cut456260,Chamfer006012142]
FEATURE [App::DocumentObjectGroup] Group010  label="6158 Heated Bed"
  Group = -> [Group020,Cylinder054099009029,Cut456099,Fusion051010010012015014088020142]
FEATURE [Part::Box] Box112015002017004007004038086003009003088019011111  label="Cube350"
  AttacherType = Attacher::AttachEngine3D
  Height = 42
  Length = 32
  Placement = pos=(-11,-30,-1) rot=(0,0,1;0rad)
  Width = 60
FEATURE [Part::Cylinder] Cylinder054099009137116  label="boss002"
  Angle = 360
  AttacherType = Attacher::AttachEngine3D
  Height = 3
  Placement = pos=(-11,0,17.5) rot=(0,1,0;1.5708rad)
  Radius = 12
FEATURE [Part::Cut] Cut456263
  Base = -> Box112015002017004007004038086003009003088019011111
  Tool = -> Cylinder054099009137116
FEATURE [Part::Cylinder] Cylinder054099009137117  label="M3-009"
  Angle = 360
  AttacherType = Attacher::AttachEngine3D
  Height = 50
  Placement = pos=(-12,13,30.5) rot=(0,1,0;1.5708rad)
  Radius = 1.7
FEATURE [Part::Cylinder] Cylinder054099009137118  label="M3-010"
  Angle = 360
  AttacherType = Attacher::AttachEngine3D
  Height = 50
  Placement = pos=(-12,-13,4.5) rot=(0,1,0;1.5708rad)
  Radius = 1.7
FEATURE [Part::Cylinder] Cylinder054099009137119  label="M3-011"
  Angle = 360
  AttacherType = Attacher::AttachEngine3D
  Height = 50
  Placement = pos=(-12,13,4.5) rot=(0,1,0;1.5708rad)
  Radius = 1.7
FEATURE [Part::Cylinder] Cylinder054099009137120  label="M3-012"
  Angle = 360
  AttacherType = Attacher::AttachEngine3D
  Height = 50
  Placement = pos=(-12,-13,30.5) rot=(0,1,0;1.5708rad)
  Radius = 1.7
FEATURE [Part::Cut] Cut456264
  Base = -> Cut456263
  Tool = -> Cylinder054099009137117
FEATURE [Part::Cut] Cut456265
  Base = -> Cut456264
  Tool = -> Cylinder054099009137120
FEATURE [Part::Cut] Cut456266
  Base = -> Cut456265
  Tool = -> Cylinder054099009137119
FEATURE [Part::Cut] Cut456267
  Base = -> Cut456266
  Tool = -> Cylinder054099009137118
FEATURE [Part::Cylinder] Cylinder054099009137121  label="drive002"
  Angle = 360
  AttacherType = Attacher::AttachEngine3D
  Height = 40
  Placement = pos=(-9,0,17.5) rot=(0,1,0;1.5708rad)
  Radius = 8
FEATURE [Part::Cut] Cut456268
  Base = -> Cut456267
  Tool = -> Cylinder054099009137121
FEATURE [Part::Box] Box112015002017004007004038086003009003088019011112  label="Cube351"
  AttacherType = Attacher::AttachEngine3D
  Height = 50
  Length = 18
  Placement = pos=(-8,-10,9) rot=(0,0,1;0rad)
  Width = 20
FEATURE [Part::Cut] Cut456269
  Base = -> Cut456268
  Tool = -> Box112015002017004007004038086003009003088019011112
FEATURE [Part::Cylinder] Cylinder054099009137122  label="grub-005"
  Angle = 360
  AttacherType = Attacher::AttachEngine3D
  Height = 30
  Placement = pos=(-28,26,32) rot=(1,0,0;1.5708rad)
  Radius = 1.7
FEATURE [Part::Box] Box112015002017004007004038086003009003088019011113  label="Cube352"
  AttacherType = Attacher::AttachEngine3D
  Height = 33
  Length = 5.3
  Placement = pos=(-30.65,6,29) rot=(0,0,1;0rad)
  Width = 2.5
FEATURE [Part::Fuse] Fusion051010010012015014088020143  label="nut-trap002"
  Base = -> Cylinder054099009137122
  Placement = pos=(43,5,5) rot=(0,0,1;0rad)
  Tool = -> Box112015002017004007004038086003009003088019011113
FEATURE [Part::Box] Box112015002017004007004038086003009003088019011114  label="Cube353"
  AttacherType = Attacher::AttachEngine3D
  Height = 50
  Length = 15
  Placement = pos=(10,19.25,13) rot=(0,0,1;0rad)
  Width = 1.5
FEATURE [Part::Fuse] Fusion051010010012015014088020144  label="rod-clamp002"
  Base = -> Fusion051010010012015014088020143
  Tool = -> Box112015002017004007004038086003009003088019011114
FEATURE [Part::Cylinder] Cylinder054099009137123  label="steel-007"
  Angle = 360
  AttacherType = Attacher::AttachEngine3D
  Height = 395
  Placement = pos=(9,20,-300) rot=(0,0,1;0rad)
  Radius = 3.95
FEATURE [Part::Fuse] Fusion051010010012015014088020145  label="rod-and-clamp004"
  Base = -> Fusion051010010012015014088020144
  Tool = -> Cylinder054099009137123
FEATURE [Part::Fuse] Fusion051010010012015014088020146  label="rod-and-clamp005"
  Base = -> Fusion051010010012015014088020144
  Tool = -> Cylinder054099009137123
FEATURE [Part::Mirroring] Part__Mirroring005078  label="rod-and-clamp (Mirror #7)002"
  Base = (0,0,0)
  Normal = (0,1,0)
  Source = -> Fusion051010010012015014088020145
FEATURE [Part::Cut] Cut456271
  Base = -> Cut456269
  Tool = -> Fusion051010010012015014088020146
FEATURE [Part::Cut] Cut456270  label="base-block-b001"
  Base = -> Cut456271
  Placement = pos=(0,0,-299) rot=(0,0,1;0rad)
  Tool = -> Part__Mirroring005078
FEATURE [Part::Box] Box112015002017004007004038086003009003088019011115  label="crimp-hole-003"
  AttacherType = Attacher::AttachEngine3D
  Height = 2
  Length = 29
  Placement = pos=(-28,-27,-278.5) rot=(0,0,1;0rad)
  Width = 2
FEATURE [Part::Box] Box112015002017004007004038086003009003088019011116  label="crimp-hole-004"
  AttacherType = Attacher::AttachEngine3D
  Height = 2
  Length = 29
  Placement = pos=(-27.8,-27,-283.58) rot=(0,0,1;0rad)
  Width = 2
FEATURE [Part::Feature] Face027
  Placement = pos=(0,0,20) rot=(0,0,1;0rad)
  shape: bbox 2e-07 x 2.603 x 2.778 mm, 1 faces, 0 solids (baked)
FEATURE [Part::Feature] Shape039
  shape: bbox 24.53 x 3.067 x 36 mm, 0 faces, 0 solids (baked)
FEATURE [Part::Feature] Face028
  shape: bbox 2e-07 x 7.388 x 7.38 mm, 1 faces, 0 solids (baked)
FEATURE [Part::Sweep] Sweep030
  Frenet = false
  Sections = -> [Face028]
  Solid = true
  Spine = -> Shape039 [Edge1]
  Transition = 1
FEATURE [Part::Sweep] Sweep031
  Frenet = false
  Sections = -> [Face028]
  Solid = true
  Spine = -> Shape039 [Edge1]
  Transition = 1
FEATURE [Part::Mirroring] Part__Mirroring005079  label="Sweep002 (Mirror #5)001"
  Base = (0,0,0)
  Normal = (0,1,0)
  Source = -> Sweep030
FEATURE [Part::Cut] Cut456272
  Base = -> Cut456270
  Tool = -> Sweep031
FEATURE [Part::Cut] Cut456273
  Base = -> Cut456272
  Tool = -> Part__Mirroring005079
FEATURE [Part::Feature] Shape040
  shape: bbox 8.807 x 6.01 x 17.13 mm, 0 faces, 0 solids (baked)
FEATURE [Part::Sweep] Sweep032
  Frenet = false
  Sections = -> [Face027]
  Solid = true
  Spine = -> Shape040 [Edge1]
  Transition = 1
FEATURE [Part::Fuse] Fusion051010010012015014088020147  label="wire-hole-003"
  Base = -> Box112015002017004007004038086003009003088019011115
  Tool = -> Sweep032
FEATURE [Part::Feature] Shape041
  shape: bbox 9.107 x 52.63 x 38.07 mm, 0 faces, 0 solids (baked)
FEATURE [Part::Feature] Face029
  Placement = pos=(0,0,14.92) rot=(0,0,1;0rad)
  shape: bbox 2e-07 x 2.603 x 2.778 mm, 1 faces, 0 solids (baked)
FEATURE [Part::Sweep] Sweep033
  Frenet = false
  Sections = -> [Face029]
  Solid = true
  Spine = -> Shape041 [Edge1]
  Transition = 1
FEATURE [Part::Fuse] Fusion051010010012015014088020148  label="wire-hole-004"
  Base = -> Box112015002017004007004038086003009003088019011116
  Tool = -> Sweep033
FEATURE [Part::Cut] Cut456274
  Base = -> Cut456273
  Tool = -> Fusion051010010012015014088020147
FEATURE [Part::Cut] Cut456275  label="bottom-block-007"
  Base = -> Cut456274
  Tool = -> Fusion051010010012015014088020148
FEATURE [Part::Cylinder] Cylinder054099009137124  label="steel-008"
  Angle = 360
  AttacherType = Attacher::AttachEngine3D
  Height = 16
  Placement = pos=(9,-20,-260) rot=(0,0,1;0rad)
  Radius = 2
FEATURE [Part::Chamfer] Chamfer006012143
  Base = -> Cylinder054099009137124
  Edges = 1 edges r=1: [Edge3]
FEATURE [Part::Chamfer] Chamfer006012144
  Base = -> Chamfer006012143
  Edges = 1 edges r=1: [Edge3]
  Placement = pos=(0.3,-2.2,-15) rot=(0,0,1;0rad)
FEATURE [Part::Chamfer] Chamfer006012145
  Base = -> Chamfer006012143
  Edges = 1 edges r=1: [Edge3]
  Placement = pos=(0.3,-2.2,-15) rot=(0,0,1;0rad)
FEATURE [Part::Mirroring] Part__Mirroring005080  label="Chamfer006012034 (Mirror #6)001"
  Base = (0,0,0)
  Normal = (0,1,0)
  Source = -> Chamfer006012144
FEATURE [Part::Cut] Cut456276
  Base = -> Cut456275
  Tool = -> Chamfer006012145
FEATURE [Part::Cut] Cut456277  label="bottom-block-008"
  Base = -> Cut456276
  Tool = -> Part__Mirroring005080
FEATURE [Part::Box] Box112015002017004007004038086003009003088019011117  label="Cube354"
  AttacherType = Attacher::AttachEngine3D
  Height = 10
  Length = 8
  Placement = pos=(5,13.5,-285) rot=(0,0,1;0rad)
  Width = 4
FEATURE [Part::Chamfer] Chamfer006012146
  Base = -> Box112015002017004007004038086003009003088019011117
  Edges = 1 edges r=3: [Edge11]
FEATURE [Part::Chamfer] Chamfer006012147
  Base = -> Box112015002017004007004038086003009003088019011117
  Edges = 1 edges r=3: [Edge11]
FEATURE [Part::Mirroring] Part__Mirroring005081  label="Chamfer006012038 (Mirror #8)001"
  Base = (0,0,0)
  Normal = (0,1,0)
  Source = -> Chamfer006012146
FEATURE [Part::Fuse] Fusion051010010012015014088020149
  Base = -> Cut456277
  Tool = -> Chamfer006012147
FEATURE [Part::Fuse] Fusion051010010012015014088020150  label="bottom-block-009"
  Base = -> Part__Mirroring005081
  Tool = -> Fusion051010010012015014088020149
FEATURE [Part::Cylinder] Cylinder054099009137125  label="Cylinder054099009137137"
  Angle = 360
  AttacherType = Attacher::AttachEngine3D
  Height = 50
  Placement = pos=(-6,-16,-286) rot=(1,0,0;1.5708rad)
  Radius = 1.3
FEATURE [Part::Cylinder] Cylinder054099009137126  label="Cylinder054099009137138"
  Angle = 360
  AttacherType = Attacher::AttachEngine3D
  Height = 50
  Placement = pos=(-6,-16,-296.5) rot=(1,0,0;1.5708rad)
  Radius = 1.3
FEATURE [Part::Cylinder] Cylinder054099009137127  label="Cylinder054099009137139"
  Angle = 360
  AttacherType = Attacher::AttachEngine3D
  Height = 50
  Placement = pos=(-6,-16,-286) rot=(1,0,0;1.5708rad)
  Radius = 1.3
FEATURE [Part::Cylinder] Cylinder054099009137128  label="Cylinder054099009137140"
  Angle = 360
  AttacherType = Attacher::AttachEngine3D
  Height = 50
  Placement = pos=(-6,-16,-296.5) rot=(1,0,0;1.5708rad)
  Radius = 1.3
FEATURE [Part::Mirroring] Part__Mirroring005082  label="Cylinder054101 (Mirror #15)001"
  Base = (0,0,0)
  Normal = (0,1,0)
  Source = -> Cylinder054099009137127
FEATURE [Part::Mirroring] Part__Mirroring005083  label="Cylinder054102 (Mirror #16)001"
  Base = (0,0,0)
  Normal = (0,1,0)
  Source = -> Cylinder054099009137128
FEATURE [Part::Cut] Cut456278
  Base = -> Fusion051010010012015014088020150
  Tool = -> Cylinder054099009137125
FEATURE [Part::Cut] Cut456279
  Base = -> Cut456278
  Tool = -> Cylinder054099009137126
FEATURE [Part::Cut] Cut456280
  Base = -> Cut456279
  Tool = -> Part__Mirroring005082
FEATURE [Part::Cut] Cut456281
  Base = -> Cut456280
  Tool = -> Part__Mirroring005083
FEATURE [Part::Cylinder] Cylinder054099009137129  label="Cylinder054099009137141"
  Angle = 360
  AttacherType = Attacher::AttachEngine3D
  Height = 10
  Placement = pos=(11,0,-301) rot=(0,0,1;0rad)
  Radius = 1.3
FEATURE [Part::Cut] Cut456282
  Base = -> Cut456281
  Tool = -> Cylinder054099009137129
FEATURE [Part::Cylinder] Cylinder054099009137130  label="foot-mount003"
  Angle = 360
  AttacherType = Attacher::AttachEngine3D
  Height = 16
  Placement = pos=(-1,20,-267) rot=(0,0,1;0rad)
  Radius = 1.3
FEATURE [Part::Cylinder] Cylinder054099009137131  label="top-mount-009"
  Angle = 360
  AttacherType = Attacher::AttachEngine3D
  Height = 16
  Placement = pos=(-1,20,-272) rot=(0,0,1;0rad)
  Radius = 1.3
FEATURE [Part::Mirroring] Part__Mirroring005084  label="top-mount-010"
  Base = (0,0,0)
  Normal = (0,1,0)
  Placement = pos=(0,0,-5) rot=(0,0,1;0rad)
  Source = -> Cylinder054099009137130
FEATURE [Part::Cut] Cut456283
  Base = -> Cut456282
  Tool = -> Cylinder054099009137131
FEATURE [Part::Cut] Cut456284
  Base = -> Cut456283
  Tool = -> Part__Mirroring005084
FEATURE [Part::Chamfer] Chamfer006012148
  Base = -> Cut456284
  Edges = 1 edges r=1: [Edge4]
FEATURE [Part::Chamfer] Chamfer006012149  label="bottom-block-010"
  Base = -> Chamfer006012148
  Edges = 1 edges r=1: [Edge3]
FEATURE [Part::Chamfer] Chamfer006012150
  Base = -> Chamfer006012149
  Edges = 1 edges r=1: [Edge1]
FEATURE [Part::Feature] Face030
  shape: bbox 2.373 x 2e-07 x 2.456 mm, 1 faces, 0 solids (baked)
FEATURE [Part::Feature] Shape042
  shape: bbox 66.17 x 81 x 49.85 mm, 0 faces, 0 solids (baked)
FEATURE [Part::Sweep] Sweep034
  Frenet = false
  Sections = -> [Face030]
  Solid = true
  Spine = -> Shape042 [Edge1]
  Transition = 1
FEATURE [Part::Cut] Cut456285
  Base = -> Chamfer006012150
  Tool = -> Sweep034
FEATURE [Part::Feature] Face031
  shape: bbox 2.373 x 2e-07 x 2.456 mm, 1 faces, 0 solids (baked)
FEATURE [Part::Feature] Shape043
  shape: bbox 66.17 x 81 x 49.85 mm, 0 faces, 0 solids (baked)
FEATURE [Part::Sweep] Sweep035
  Frenet = false
  Sections = -> [Face031]
  Solid = true
  Spine = -> Shape043 [Edge1]
  Transition = 1
FEATURE [Part::Mirroring] Part__Mirroring005085  label="Sweep022 (Mirror #26)001"
  Base = (0,0,0)
  Normal = (0,1,0)
  Source = -> Sweep035
FEATURE [Part::Cut] Cut456286  label="6138 bottom-block001"
  Base = -> Cut456285
  Placement = pos=(0,0,0) rot=(0,0,-1;0.523599rad)
  Tool = -> Part__Mirroring005085
FEATURE [Part::Mirroring] Part__Mirroring005086  label="6138 bottom-block001 (Mirror #71)"
  Base = (0,0,0)
  Normal = (1,0,0)
  Placement = pos=(-184.463,-106.5,0) rot=(0,0,1;0.523599rad)
  Source = -> Cut456286
FEATURE [Part::Cylinder] Cylinder054099009137132  label="Cylinder054099009137142"
  Angle = 360
  AttacherType = Attacher::AttachEngine3D
  Height = 500
  Placement = pos=(-168.494,-142.752,-295.789) rot=(-0.137328,0.608033,0.781945;0.754092rad)
  Radius = 3.2
FEATURE [Part::Box] Box112015002017004007004038086003009003088019011118  label="Cube355"
  AttacherType = Attacher::AttachEngine3D
  Height = 15
  Length = 17
  Placement = pos=(4,-48,105) rot=(0,0,1;0rad)
  Width = 18
FEATURE [Part::Box] Box112015002017004007004038086003009003088019011119  label="Cube356"
  AttacherType = Attacher::AttachEngine3D
  Height = 15
  Length = 26
  Placement = pos=(-153.4,-148.7,-273) rot=(0,0,1;1.0472rad)
  Width = 18
FEATURE [Part::Cylinder] Cylinder054099009137133  label="Cylinder054099009137143"
  Angle = 360
  AttacherType = Attacher::AttachEngine3D
  Height = 10
  Placement = pos=(-155,-135,-263.79) rot=(-0.137328,0.608033,0.781945;0.754092rad)
  Radius = 6
FEATURE [Part::Cylinder] Cylinder054099009137134  label="Cylinder054099009137144"
  Angle = 360
  AttacherType = Attacher::AttachEngine3D
  Height = 10
  Placement = pos=(-160,-138,-275.79) rot=(-0.137328,0.608033,0.781945;0.754092rad)
  Radius = 6
FEATURE [Part::MultiFuse] Fusion051010010012015014088020151
  Shapes = -> [Box112015002017004007004038086003009003088019011119,Cylinder054099009137133,Cylinder054099009137134]
FEATURE [Part::Cylinder] Cylinder054099009137137  label="Cylinder054099009137147"
  Angle = 360
  AttacherType = Attacher::AttachEngine3D
  Height = 500
  Placement = pos=(-168.494,-142.752,-295.789) rot=(-0.137328,0.608033,0.781945;0.754092rad)
  Radius = 3.2
FEATURE [Part::Cylinder] Cylinder054099009137138  label="Cylinder054099009137148"
  Angle = 360
  AttacherType = Attacher::AttachEngine3D
  Height = 30
  Placement = pos=(-170.4,-132,-262) rot=(0.774597,0.447214,0.447214;1.82349rad)
  Radius = 1.7
FEATURE [Part::Chamfer] Chamfer006012151
  Base = -> Fusion051010010012015014088020151
  Edges = 1 edges r=4: [Edge13]
FEATURE [Part::Cut] Cut456287
  Base = -> Chamfer006012151
  Tool = -> Cylinder054099009137138
FEATURE [Part::Cut] Cut456288  label="base-brace-block"
  Base = -> Cut456287
  Tool = -> Cylinder054099009137132
FEATURE [Part::Cylinder] Cylinder054099009137139  label="brace"
  Angle = 360
  AttacherType = Attacher::AttachEngine3D
  Height = 500
  Placement = pos=(-168.494,-142.752,-295.789) rot=(-0.137328,0.608033,0.781945;0.754092rad)
  Radius = 3.2
FEATURE [Part::Cylinder] Cylinder054099009137140  label="Cylinder054099009137149"
  Angle = 360
  AttacherType = Attacher::AttachEngine3D
  Height = 24
  Placement = pos=(3.5,-43.7,101.79) rot=(-0.137328,0.608033,0.781945;0.754092rad)
  Radius = 6
FEATURE [Part::MultiFuse] Fusion051010010012015014088020152
  Shapes = -> [Box112015002017004007004038086003009003088019011118,Cylinder054099009137140]
FEATURE [Part::Cylinder] Cylinder054099009137141  label="Cylinder054099009137150"
  Angle = 360
  AttacherType = Attacher::AttachEngine3D
  Height = 30
  Placement = pos=(15,-27,116) rot=(1,0,0;1.5708rad)
  Radius = 1.7
FEATURE [Part::Cut] Cut456289
  Base = -> Fusion051010010012015014088020152
  Tool = -> Cylinder054099009137141
FEATURE [Part::Cut] Cut456290  label="top-brace-block"
  Base = -> Cut456289
  Tool = -> Cylinder054099009137137
